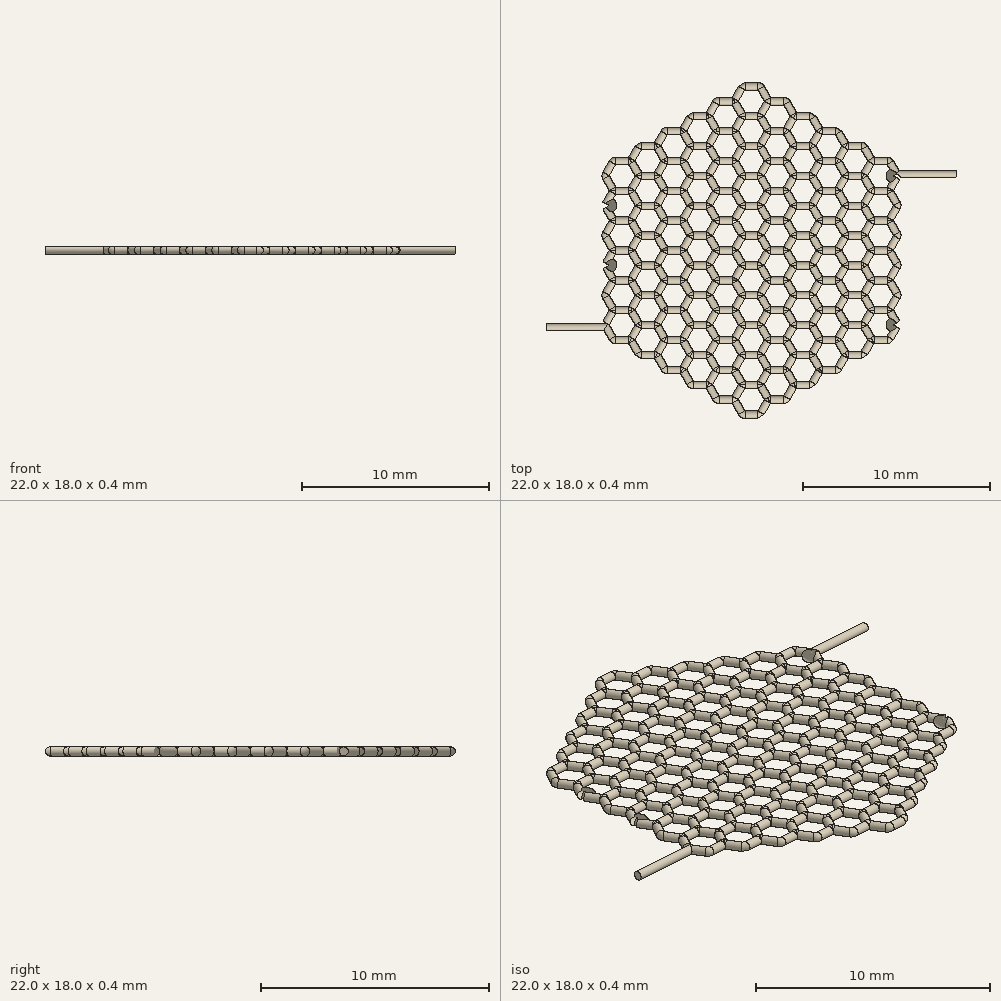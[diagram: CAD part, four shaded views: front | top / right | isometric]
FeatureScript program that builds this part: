
annotation { "Feature Type Name" : "Feature", "Feature Type Description" : "" }
export const myFeature = defineFeature(function(context is Context, id is Id, definition is map)
    precondition{}
    {
        {
            var Q0;
            Q0=qCreatedBy(makeId("Top.planeOp"),FACE);
            cPlane(context, id + "F0", {"entities" : qUnion([Q0]), "cplaneType" : CPlaneType.OFFSET, "offset" : 0.2 * mm, "width" : 150 * mm, "height" : 150 * mm});
        }
        {
            var Q0;
            Q0=qCreatedBy(id+"F0.planeOp",FACE);
            var sketch = newSketch(context, id + "F1", { "sketchPlane" : qUnion([Q0])});
            skLineSegment(sketch, "E0", {"start": v(-0.35, -0.8) * mm, "end": v(0.35, -0.8) * mm});
            skLineSegment(sketch, "E1", {"start": v(0.52, -0.7) * mm, "end": v(0.87, -0.1) * mm});
            skLineSegment(sketch, "E2", {"start": v(0.87, 0.1) * mm, "end": v(0.52, 0.7) * mm});
            skLineSegment(sketch, "E3", {"start": v(0.35, 0.8) * mm, "end": v(-0.35, 0.8) * mm});
            skLineSegment(sketch, "E4", {"start": v(-0.52, 0.7) * mm, "end": v(-0.87, 0.1) * mm});
            skLineSegment(sketch, "E5", {"start": v(-0.87, -0.1) * mm, "end": v(-0.52, -0.7) * mm});
            skArc(sketch, "E6.filletArc", {"start": v(-0.35, 0.8) * mm, "mid": v(-0.45, 0.77) * mm, "end": v(-0.52, 0.7) * mm});
            skArc(sketch, "E7.filletArc", {"start": v(-0.87, 0.1) * mm, "mid": v(-0.9, 0) * mm, "end": v(-0.87, -0.1) * mm});
            skArc(sketch, "E8.filletArc", {"start": v(-0.52, -0.7) * mm, "mid": v(-0.45, -0.77) * mm, "end": v(-0.35, -0.8) * mm});
            skArc(sketch, "E9.filletArc", {"start": v(0.35, -0.8) * mm, "mid": v(0.45, -0.77) * mm, "end": v(0.52, -0.7) * mm});
            skArc(sketch, "E10.filletArc", {"start": v(0.87, -0.1) * mm, "mid": v(0.9, 0) * mm, "end": v(0.87, 0.1) * mm});
            skArc(sketch, "E11.filletArc", {"start": v(0.52, 0.7) * mm, "mid": v(0.45, 0.77) * mm, "end": v(0.35, 0.8) * mm});
            skLineSegment(sketch, "E12", {"start": v(-1.73, 0) * mm, "end": v(-1.04, 0) * mm});
            skLineSegment(sketch, "E13", {"start": v(-0.87, 0.1) * mm, "end": v(-0.52, 0.7) * mm});
            skLineSegment(sketch, "E14", {"start": v(-0.52, 0.9) * mm, "end": v(-0.87, 1.5) * mm});
            skLineSegment(sketch, "E15", {"start": v(-1.04, 1.6) * mm, "end": v(-1.73, 1.6) * mm});
            skLineSegment(sketch, "E16", {"start": v(-1.9, 1.5) * mm, "end": v(-2.25, 0.9) * mm});
            skLineSegment(sketch, "E17", {"start": v(-2.25, 0.7) * mm, "end": v(-1.9, 0.1) * mm});
            skArc(sketch, "E18.filletArc", {"start": v(-1.73, 1.6) * mm, "mid": v(-1.83, 1.57) * mm, "end": v(-1.9, 1.5) * mm});
            skArc(sketch, "E19.filletArc", {"start": v(-2.25, 0.9) * mm, "mid": v(-2.28, 0.8) * mm, "end": v(-2.25, 0.7) * mm});
            skArc(sketch, "E20.filletArc", {"start": v(-1.9, 0.1) * mm, "mid": v(-1.83, 0.03) * mm, "end": v(-1.73, 0) * mm});
            skArc(sketch, "E21.filletArc", {"start": v(-1.04, 0) * mm, "mid": v(-0.94, 0.03) * mm, "end": v(-0.87, 0.1) * mm});
            skArc(sketch, "E22.filletArc", {"start": v(-0.52, 0.7) * mm, "mid": v(-0.5, 0.8) * mm, "end": v(-0.52, 0.9) * mm});
            skArc(sketch, "E23.filletArc", {"start": v(-0.87, 1.5) * mm, "mid": v(-0.94, 1.57) * mm, "end": v(-1.04, 1.6) * mm});
            skLineSegment(sketch, "E24", {"start": v(-1.73, -1.6) * mm, "end": v(-1.04, -1.6) * mm});
            skLineSegment(sketch, "E25", {"start": v(-0.87, -1.5) * mm, "end": v(-0.52, -0.9) * mm});
            skLineSegment(sketch, "E26", {"start": v(-0.52, -0.7) * mm, "end": v(-0.87, -0.1) * mm});
            skLineSegment(sketch, "E27", {"start": v(-1.04, 0) * mm, "end": v(-1.73, 0) * mm});
            skLineSegment(sketch, "E28", {"start": v(-1.9, -0.1) * mm, "end": v(-2.25, -0.7) * mm});
            skLineSegment(sketch, "E29", {"start": v(-2.25, -0.9) * mm, "end": v(-1.9, -1.5) * mm});
            skArc(sketch, "E30.filletArc", {"start": v(-1.73, 0) * mm, "mid": v(-1.83, -0.03) * mm, "end": v(-1.9, -0.1) * mm});
            skArc(sketch, "E31.filletArc", {"start": v(-2.25, -0.7) * mm, "mid": v(-2.28, -0.8) * mm, "end": v(-2.25, -0.9) * mm});
            skArc(sketch, "E32.filletArc", {"start": v(-1.9, -1.5) * mm, "mid": v(-1.83, -1.57) * mm, "end": v(-1.73, -1.6) * mm});
            skArc(sketch, "E33.filletArc", {"start": v(-1.04, -1.6) * mm, "mid": v(-0.94, -1.57) * mm, "end": v(-0.87, -1.5) * mm});
            skArc(sketch, "E34.filletArc", {"start": v(-0.52, -0.9) * mm, "mid": v(-0.5, -0.8) * mm, "end": v(-0.52, -0.7) * mm});
            skArc(sketch, "E35.filletArc", {"start": v(-0.87, -0.1) * mm, "mid": v(-0.94, -0.03) * mm, "end": v(-1.04, 0) * mm});
            skLineSegment(sketch, "E36", {"start": v(-0.35, -2.4) * mm, "end": v(0.35, -2.4) * mm});
            skLineSegment(sketch, "E37", {"start": v(0.52, -2.3) * mm, "end": v(0.87, -1.7) * mm});
            skLineSegment(sketch, "E38", {"start": v(0.87, -1.5) * mm, "end": v(0.52, -0.9) * mm});
            skLineSegment(sketch, "E39", {"start": v(0.35, -0.8) * mm, "end": v(-0.35, -0.8) * mm});
            skLineSegment(sketch, "E40", {"start": v(-0.52, -0.9) * mm, "end": v(-0.87, -1.5) * mm});
            skLineSegment(sketch, "E41", {"start": v(-0.87, -1.7) * mm, "end": v(-0.52, -2.3) * mm});
            skArc(sketch, "E42.filletArc", {"start": v(-0.35, -0.8) * mm, "mid": v(-0.45, -0.83) * mm, "end": v(-0.52, -0.9) * mm});
            skArc(sketch, "E43.filletArc", {"start": v(-0.87, -1.5) * mm, "mid": v(-0.9, -1.6) * mm, "end": v(-0.87, -1.7) * mm});
            skArc(sketch, "E44.filletArc", {"start": v(-0.52, -2.3) * mm, "mid": v(-0.45, -2.37) * mm, "end": v(-0.35, -2.4) * mm});
            skArc(sketch, "E45.filletArc", {"start": v(0.35, -2.4) * mm, "mid": v(0.45, -2.37) * mm, "end": v(0.52, -2.3) * mm});
            skArc(sketch, "E46.filletArc", {"start": v(0.87, -1.7) * mm, "mid": v(0.9, -1.6) * mm, "end": v(0.87, -1.5) * mm});
            skArc(sketch, "E47.filletArc", {"start": v(0.52, -0.9) * mm, "mid": v(0.45, -0.83) * mm, "end": v(0.35, -0.8) * mm});
            skLineSegment(sketch, "E48", {"start": v(1.04, -1.6) * mm, "end": v(1.73, -1.6) * mm});
            skLineSegment(sketch, "E49", {"start": v(1.9, -1.5) * mm, "end": v(2.25, -0.9) * mm});
            skLineSegment(sketch, "E50", {"start": v(2.25, -0.7) * mm, "end": v(1.9, -0.1) * mm});
            skLineSegment(sketch, "E51", {"start": v(1.73, 0) * mm, "end": v(1.04, 0) * mm});
            skLineSegment(sketch, "E52", {"start": v(0.87, -0.1) * mm, "end": v(0.52, -0.7) * mm});
            skLineSegment(sketch, "E53", {"start": v(0.52, -0.9) * mm, "end": v(0.87, -1.5) * mm});
            skArc(sketch, "E54.filletArc", {"start": v(1.04, 0) * mm, "mid": v(0.94, -0.03) * mm, "end": v(0.87, -0.1) * mm});
            skArc(sketch, "E55.filletArc", {"start": v(0.52, -0.7) * mm, "mid": v(0.5, -0.8) * mm, "end": v(0.52, -0.9) * mm});
            skArc(sketch, "E56.filletArc", {"start": v(0.87, -1.5) * mm, "mid": v(0.94, -1.57) * mm, "end": v(1.04, -1.6) * mm});
            skArc(sketch, "E57.filletArc", {"start": v(1.73, -1.6) * mm, "mid": v(1.83, -1.57) * mm, "end": v(1.9, -1.5) * mm});
            skArc(sketch, "E58.filletArc", {"start": v(2.25, -0.9) * mm, "mid": v(2.28, -0.8) * mm, "end": v(2.25, -0.7) * mm});
            skArc(sketch, "E59.filletArc", {"start": v(1.9, -0.1) * mm, "mid": v(1.83, -0.03) * mm, "end": v(1.73, 0) * mm});
            skLineSegment(sketch, "E60", {"start": v(1.04, 0) * mm, "end": v(1.73, 0) * mm});
            skLineSegment(sketch, "E61", {"start": v(1.9, 0.1) * mm, "end": v(2.25, 0.7) * mm});
            skLineSegment(sketch, "E62", {"start": v(2.25, 0.9) * mm, "end": v(1.9, 1.5) * mm});
            skLineSegment(sketch, "E63", {"start": v(1.73, 1.6) * mm, "end": v(1.04, 1.6) * mm});
            skLineSegment(sketch, "E64", {"start": v(0.87, 1.5) * mm, "end": v(0.52, 0.9) * mm});
            skLineSegment(sketch, "E65", {"start": v(0.52, 0.7) * mm, "end": v(0.87, 0.1) * mm});
            skArc(sketch, "E66.filletArc", {"start": v(1.04, 1.6) * mm, "mid": v(0.94, 1.57) * mm, "end": v(0.87, 1.5) * mm});
            skArc(sketch, "E67.filletArc", {"start": v(0.52, 0.9) * mm, "mid": v(0.5, 0.8) * mm, "end": v(0.52, 0.7) * mm});
            skArc(sketch, "E68.filletArc", {"start": v(0.87, 0.1) * mm, "mid": v(0.94, 0.03) * mm, "end": v(1.04, 0) * mm});
            skArc(sketch, "E69.filletArc", {"start": v(1.73, 0) * mm, "mid": v(1.83, 0.03) * mm, "end": v(1.9, 0.1) * mm});
            skArc(sketch, "E70.filletArc", {"start": v(2.25, 0.7) * mm, "mid": v(2.28, 0.8) * mm, "end": v(2.25, 0.9) * mm});
            skArc(sketch, "E71.filletArc", {"start": v(1.9, 1.5) * mm, "mid": v(1.83, 1.57) * mm, "end": v(1.73, 1.6) * mm});
            skLineSegment(sketch, "E72", {"start": v(-0.35, 0.8) * mm, "end": v(0.35, 0.8) * mm});
            skLineSegment(sketch, "E73", {"start": v(0.52, 0.9) * mm, "end": v(0.87, 1.5) * mm});
            skLineSegment(sketch, "E74", {"start": v(0.87, 1.7) * mm, "end": v(0.52, 2.3) * mm});
            skLineSegment(sketch, "E75", {"start": v(0.35, 2.4) * mm, "end": v(-0.35, 2.4) * mm});
            skLineSegment(sketch, "E76", {"start": v(-0.52, 2.3) * mm, "end": v(-0.87, 1.7) * mm});
            skLineSegment(sketch, "E77", {"start": v(-0.87, 1.5) * mm, "end": v(-0.52, 0.9) * mm});
            skArc(sketch, "E78.filletArc", {"start": v(-0.35, 2.4) * mm, "mid": v(-0.45, 2.37) * mm, "end": v(-0.52, 2.3) * mm});
            skArc(sketch, "E79.filletArc", {"start": v(-0.87, 1.7) * mm, "mid": v(-0.9, 1.6) * mm, "end": v(-0.87, 1.5) * mm});
            skArc(sketch, "E80.filletArc", {"start": v(-0.52, 0.9) * mm, "mid": v(-0.45, 0.83) * mm, "end": v(-0.35, 0.8) * mm});
            skArc(sketch, "E81.filletArc", {"start": v(0.35, 0.8) * mm, "mid": v(0.45, 0.83) * mm, "end": v(0.52, 0.9) * mm});
            skArc(sketch, "E82.filletArc", {"start": v(0.87, 1.5) * mm, "mid": v(0.9, 1.6) * mm, "end": v(0.87, 1.7) * mm});
            skArc(sketch, "E83.filletArc", {"start": v(0.52, 2.3) * mm, "mid": v(0.45, 2.37) * mm, "end": v(0.35, 2.4) * mm});
            skLineSegment(sketch, "E84", {"start": v(-3.12, -0.8) * mm, "end": v(-2.42, -0.8) * mm});
            skLineSegment(sketch, "E85", {"start": v(-2.25, -0.7) * mm, "end": v(-1.9, -0.1) * mm});
            skLineSegment(sketch, "E86", {"start": v(-1.9, 0.1) * mm, "end": v(-2.25, 0.7) * mm});
            skLineSegment(sketch, "E87", {"start": v(-2.42, 0.8) * mm, "end": v(-3.12, 0.8) * mm});
            skLineSegment(sketch, "E88", {"start": v(-3.3, 0.7) * mm, "end": v(-3.64, 0.1) * mm});
            skLineSegment(sketch, "E89", {"start": v(-3.64, -0.1) * mm, "end": v(-3.3, -0.7) * mm});
            skArc(sketch, "E90.filletArc", {"start": v(-3.12, 0.8) * mm, "mid": v(-3.22, 0.77) * mm, "end": v(-3.3, 0.7) * mm});
            skArc(sketch, "E91.filletArc", {"start": v(-3.64, 0.1) * mm, "mid": v(-3.66, 0) * mm, "end": v(-3.64, -0.1) * mm});
            skArc(sketch, "E92.filletArc", {"start": v(-3.3, -0.7) * mm, "mid": v(-3.22, -0.77) * mm, "end": v(-3.12, -0.8) * mm});
            skArc(sketch, "E93.filletArc", {"start": v(-2.42, -0.8) * mm, "mid": v(-2.32, -0.77) * mm, "end": v(-2.25, -0.7) * mm});
            skArc(sketch, "E94.filletArc", {"start": v(-1.9, -0.1) * mm, "mid": v(-1.88, 0) * mm, "end": v(-1.9, 0.1) * mm});
            skArc(sketch, "E95.filletArc", {"start": v(-2.25, 0.7) * mm, "mid": v(-2.32, 0.77) * mm, "end": v(-2.42, 0.8) * mm});
            skLineSegment(sketch, "E96", {"start": v(-3.12, -2.4) * mm, "end": v(-2.42, -2.4) * mm});
            skLineSegment(sketch, "E97", {"start": v(-2.25, -2.3) * mm, "end": v(-1.9, -1.7) * mm});
            skLineSegment(sketch, "E98", {"start": v(-1.9, -1.5) * mm, "end": v(-2.25, -0.9) * mm});
            skLineSegment(sketch, "E99", {"start": v(-2.42, -0.8) * mm, "end": v(-3.12, -0.8) * mm});
            skLineSegment(sketch, "E100", {"start": v(-3.3, -0.9) * mm, "end": v(-3.64, -1.5) * mm});
            skLineSegment(sketch, "E101", {"start": v(-3.64, -1.7) * mm, "end": v(-3.3, -2.3) * mm});
            skArc(sketch, "E102.filletArc", {"start": v(-3.12, -0.8) * mm, "mid": v(-3.22, -0.83) * mm, "end": v(-3.3, -0.9) * mm});
            skArc(sketch, "E103.filletArc", {"start": v(-3.64, -1.5) * mm, "mid": v(-3.66, -1.6) * mm, "end": v(-3.64, -1.7) * mm});
            skArc(sketch, "E104.filletArc", {"start": v(-3.3, -2.3) * mm, "mid": v(-3.22, -2.37) * mm, "end": v(-3.12, -2.4) * mm});
            skArc(sketch, "E105.filletArc", {"start": v(-2.42, -2.4) * mm, "mid": v(-2.32, -2.37) * mm, "end": v(-2.25, -2.3) * mm});
            skArc(sketch, "E106.filletArc", {"start": v(-1.9, -1.7) * mm, "mid": v(-1.88, -1.6) * mm, "end": v(-1.9, -1.5) * mm});
            skArc(sketch, "E107.filletArc", {"start": v(-2.25, -0.9) * mm, "mid": v(-2.32, -0.83) * mm, "end": v(-2.42, -0.8) * mm});
            skLineSegment(sketch, "E108", {"start": v(-0.35, -4) * mm, "end": v(0.35, -4) * mm});
            skLineSegment(sketch, "E109", {"start": v(0.52, -3.9) * mm, "end": v(0.87, -3.3) * mm});
            skLineSegment(sketch, "E110", {"start": v(0.87, -3.1) * mm, "end": v(0.52, -2.5) * mm});
            skLineSegment(sketch, "E111", {"start": v(0.35, -2.4) * mm, "end": v(-0.35, -2.4) * mm});
            skLineSegment(sketch, "E112", {"start": v(-0.52, -2.5) * mm, "end": v(-0.87, -3.1) * mm});
            skLineSegment(sketch, "E113", {"start": v(-0.87, -3.3) * mm, "end": v(-0.52, -3.9) * mm});
            skArc(sketch, "E114.filletArc", {"start": v(-0.35, -2.4) * mm, "mid": v(-0.45, -2.43) * mm, "end": v(-0.52, -2.5) * mm});
            skArc(sketch, "E115.filletArc", {"start": v(-0.87, -3.1) * mm, "mid": v(-0.9, -3.2) * mm, "end": v(-0.87, -3.3) * mm});
            skArc(sketch, "E116.filletArc", {"start": v(-0.52, -3.9) * mm, "mid": v(-0.45, -3.97) * mm, "end": v(-0.35, -4) * mm});
            skArc(sketch, "E117.filletArc", {"start": v(0.35, -4) * mm, "mid": v(0.45, -3.97) * mm, "end": v(0.52, -3.9) * mm});
            skArc(sketch, "E118.filletArc", {"start": v(0.87, -3.3) * mm, "mid": v(0.9, -3.2) * mm, "end": v(0.87, -3.1) * mm});
            skArc(sketch, "E119.filletArc", {"start": v(0.52, -2.5) * mm, "mid": v(0.45, -2.43) * mm, "end": v(0.35, -2.4) * mm});
            skLineSegment(sketch, "E120", {"start": v(-1.73, -3.2) * mm, "end": v(-1.04, -3.2) * mm});
            skLineSegment(sketch, "E121", {"start": v(-0.87, -3.1) * mm, "end": v(-0.52, -2.5) * mm});
            skLineSegment(sketch, "E122", {"start": v(-0.52, -2.3) * mm, "end": v(-0.87, -1.7) * mm});
            skLineSegment(sketch, "E123", {"start": v(-1.04, -1.6) * mm, "end": v(-1.73, -1.6) * mm});
            skLineSegment(sketch, "E124", {"start": v(-1.9, -1.7) * mm, "end": v(-2.25, -2.3) * mm});
            skLineSegment(sketch, "E125", {"start": v(-2.25, -2.5) * mm, "end": v(-1.9, -3.1) * mm});
            skArc(sketch, "E126.filletArc", {"start": v(-1.73, -1.6) * mm, "mid": v(-1.83, -1.63) * mm, "end": v(-1.9, -1.7) * mm});
            skArc(sketch, "E127.filletArc", {"start": v(-2.25, -2.3) * mm, "mid": v(-2.28, -2.4) * mm, "end": v(-2.25, -2.5) * mm});
            skArc(sketch, "E128.filletArc", {"start": v(-1.9, -3.1) * mm, "mid": v(-1.83, -3.17) * mm, "end": v(-1.73, -3.2) * mm});
            skArc(sketch, "E129.filletArc", {"start": v(-1.04, -3.2) * mm, "mid": v(-0.94, -3.17) * mm, "end": v(-0.87, -3.1) * mm});
            skArc(sketch, "E130.filletArc", {"start": v(-0.52, -2.5) * mm, "mid": v(-0.5, -2.4) * mm, "end": v(-0.52, -2.3) * mm});
            skArc(sketch, "E131.filletArc", {"start": v(-0.87, -1.7) * mm, "mid": v(-0.94, -1.63) * mm, "end": v(-1.04, -1.6) * mm});
            skLineSegment(sketch, "E132", {"start": v(2.42, -0.8) * mm, "end": v(3.12, -0.8) * mm});
            skLineSegment(sketch, "E133", {"start": v(3.3, -0.7) * mm, "end": v(3.64, -0.1) * mm});
            skLineSegment(sketch, "E134", {"start": v(3.64, 0.1) * mm, "end": v(3.3, 0.7) * mm});
            skLineSegment(sketch, "E135", {"start": v(3.12, 0.8) * mm, "end": v(2.42, 0.8) * mm});
            skLineSegment(sketch, "E136", {"start": v(2.25, 0.7) * mm, "end": v(1.9, 0.1) * mm});
            skLineSegment(sketch, "E137", {"start": v(1.9, -0.1) * mm, "end": v(2.25, -0.7) * mm});
            skArc(sketch, "E138.filletArc", {"start": v(2.42, 0.8) * mm, "mid": v(2.32, 0.77) * mm, "end": v(2.25, 0.7) * mm});
            skArc(sketch, "E139.filletArc", {"start": v(1.9, 0.1) * mm, "mid": v(1.88, 0) * mm, "end": v(1.9, -0.1) * mm});
            skArc(sketch, "E140.filletArc", {"start": v(2.25, -0.7) * mm, "mid": v(2.32, -0.77) * mm, "end": v(2.42, -0.8) * mm});
            skArc(sketch, "E141.filletArc", {"start": v(3.12, -0.8) * mm, "mid": v(3.22, -0.77) * mm, "end": v(3.3, -0.7) * mm});
            skArc(sketch, "E142.filletArc", {"start": v(3.64, -0.1) * mm, "mid": v(3.66, 0) * mm, "end": v(3.64, 0.1) * mm});
            skArc(sketch, "E143.filletArc", {"start": v(3.3, 0.7) * mm, "mid": v(3.22, 0.77) * mm, "end": v(3.12, 0.8) * mm});
            skLineSegment(sketch, "E144", {"start": v(1.04, -3.2) * mm, "end": v(1.73, -3.2) * mm});
            skLineSegment(sketch, "E145", {"start": v(1.9, -3.1) * mm, "end": v(2.25, -2.5) * mm});
            skLineSegment(sketch, "E146", {"start": v(2.25, -2.3) * mm, "end": v(1.9, -1.7) * mm});
            skLineSegment(sketch, "E147", {"start": v(1.73, -1.6) * mm, "end": v(1.04, -1.6) * mm});
            skLineSegment(sketch, "E148", {"start": v(0.87, -1.7) * mm, "end": v(0.52, -2.3) * mm});
            skLineSegment(sketch, "E149", {"start": v(0.52, -2.5) * mm, "end": v(0.87, -3.1) * mm});
            skArc(sketch, "E150.filletArc", {"start": v(1.04, -1.6) * mm, "mid": v(0.94, -1.63) * mm, "end": v(0.87, -1.7) * mm});
            skArc(sketch, "E151.filletArc", {"start": v(0.52, -2.3) * mm, "mid": v(0.5, -2.4) * mm, "end": v(0.52, -2.5) * mm});
            skArc(sketch, "E152.filletArc", {"start": v(0.87, -3.1) * mm, "mid": v(0.94, -3.17) * mm, "end": v(1.04, -3.2) * mm});
            skArc(sketch, "E153.filletArc", {"start": v(1.73, -3.2) * mm, "mid": v(1.83, -3.17) * mm, "end": v(1.9, -3.1) * mm});
            skArc(sketch, "E154.filletArc", {"start": v(2.25, -2.5) * mm, "mid": v(2.28, -2.4) * mm, "end": v(2.25, -2.3) * mm});
            skArc(sketch, "E155.filletArc", {"start": v(1.9, -1.7) * mm, "mid": v(1.83, -1.63) * mm, "end": v(1.73, -1.6) * mm});
            skLineSegment(sketch, "E156", {"start": v(2.42, -2.4) * mm, "end": v(3.12, -2.4) * mm});
            skLineSegment(sketch, "E157", {"start": v(3.3, -2.3) * mm, "end": v(3.64, -1.7) * mm});
            skLineSegment(sketch, "E158", {"start": v(3.64, -1.5) * mm, "end": v(3.3, -0.9) * mm});
            skLineSegment(sketch, "E159", {"start": v(3.12, -0.8) * mm, "end": v(2.42, -0.8) * mm});
            skLineSegment(sketch, "E160", {"start": v(2.25, -0.9) * mm, "end": v(1.9, -1.5) * mm});
            skLineSegment(sketch, "E161", {"start": v(1.9, -1.7) * mm, "end": v(2.25, -2.3) * mm});
            skArc(sketch, "E162.filletArc", {"start": v(2.42, -0.8) * mm, "mid": v(2.32, -0.83) * mm, "end": v(2.25, -0.9) * mm});
            skArc(sketch, "E163.filletArc", {"start": v(1.9, -1.5) * mm, "mid": v(1.88, -1.6) * mm, "end": v(1.9, -1.7) * mm});
            skArc(sketch, "E164.filletArc", {"start": v(2.25, -2.3) * mm, "mid": v(2.32, -2.37) * mm, "end": v(2.42, -2.4) * mm});
            skArc(sketch, "E165.filletArc", {"start": v(3.12, -2.4) * mm, "mid": v(3.22, -2.37) * mm, "end": v(3.3, -2.3) * mm});
            skArc(sketch, "E166.filletArc", {"start": v(3.64, -1.7) * mm, "mid": v(3.66, -1.6) * mm, "end": v(3.64, -1.5) * mm});
            skArc(sketch, "E167.filletArc", {"start": v(3.3, -0.9) * mm, "mid": v(3.22, -0.83) * mm, "end": v(3.12, -0.8) * mm});
            skLineSegment(sketch, "E168", {"start": v(2.42, 0.8) * mm, "end": v(3.12, 0.8) * mm});
            skLineSegment(sketch, "E169", {"start": v(3.3, 0.9) * mm, "end": v(3.64, 1.5) * mm});
            skLineSegment(sketch, "E170", {"start": v(3.64, 1.7) * mm, "end": v(3.3, 2.3) * mm});
            skLineSegment(sketch, "E171", {"start": v(3.12, 2.4) * mm, "end": v(2.42, 2.4) * mm});
            skLineSegment(sketch, "E172", {"start": v(2.25, 2.3) * mm, "end": v(1.9, 1.7) * mm});
            skLineSegment(sketch, "E173", {"start": v(1.9, 1.5) * mm, "end": v(2.25, 0.9) * mm});
            skArc(sketch, "E174.filletArc", {"start": v(2.42, 2.4) * mm, "mid": v(2.32, 2.37) * mm, "end": v(2.25, 2.3) * mm});
            skArc(sketch, "E175.filletArc", {"start": v(1.9, 1.7) * mm, "mid": v(1.88, 1.6) * mm, "end": v(1.9, 1.5) * mm});
            skArc(sketch, "E176.filletArc", {"start": v(2.25, 0.9) * mm, "mid": v(2.32, 0.83) * mm, "end": v(2.42, 0.8) * mm});
            skArc(sketch, "E177.filletArc", {"start": v(3.12, 0.8) * mm, "mid": v(3.22, 0.83) * mm, "end": v(3.3, 0.9) * mm});
            skArc(sketch, "E178.filletArc", {"start": v(3.64, 1.5) * mm, "mid": v(3.66, 1.6) * mm, "end": v(3.64, 1.7) * mm});
            skArc(sketch, "E179.filletArc", {"start": v(3.3, 2.3) * mm, "mid": v(3.22, 2.37) * mm, "end": v(3.12, 2.4) * mm});
            skLineSegment(sketch, "E180", {"start": v(-1.73, 1.6) * mm, "end": v(-1.04, 1.6) * mm});
            skLineSegment(sketch, "E181", {"start": v(-0.87, 1.7) * mm, "end": v(-0.52, 2.3) * mm});
            skLineSegment(sketch, "E182", {"start": v(-0.52, 2.5) * mm, "end": v(-0.87, 3.1) * mm});
            skLineSegment(sketch, "E183", {"start": v(-1.04, 3.2) * mm, "end": v(-1.73, 3.2) * mm});
            skLineSegment(sketch, "E184", {"start": v(-1.9, 3.1) * mm, "end": v(-2.25, 2.5) * mm});
            skLineSegment(sketch, "E185", {"start": v(-2.25, 2.3) * mm, "end": v(-1.9, 1.7) * mm});
            skArc(sketch, "E186.filletArc", {"start": v(-1.73, 3.2) * mm, "mid": v(-1.83, 3.17) * mm, "end": v(-1.9, 3.1) * mm});
            skArc(sketch, "E187.filletArc", {"start": v(-2.25, 2.5) * mm, "mid": v(-2.28, 2.4) * mm, "end": v(-2.25, 2.3) * mm});
            skArc(sketch, "E188.filletArc", {"start": v(-1.9, 1.7) * mm, "mid": v(-1.83, 1.63) * mm, "end": v(-1.73, 1.6) * mm});
            skArc(sketch, "E189.filletArc", {"start": v(-1.04, 1.6) * mm, "mid": v(-0.94, 1.63) * mm, "end": v(-0.87, 1.7) * mm});
            skArc(sketch, "E190.filletArc", {"start": v(-0.52, 2.3) * mm, "mid": v(-0.5, 2.4) * mm, "end": v(-0.52, 2.5) * mm});
            skArc(sketch, "E191.filletArc", {"start": v(-0.87, 3.1) * mm, "mid": v(-0.94, 3.17) * mm, "end": v(-1.04, 3.2) * mm});
            skLineSegment(sketch, "E192", {"start": v(1.04, 1.6) * mm, "end": v(1.73, 1.6) * mm});
            skLineSegment(sketch, "E193", {"start": v(1.9, 1.7) * mm, "end": v(2.25, 2.3) * mm});
            skLineSegment(sketch, "E194", {"start": v(2.25, 2.5) * mm, "end": v(1.9, 3.1) * mm});
            skLineSegment(sketch, "E195", {"start": v(1.73, 3.2) * mm, "end": v(1.04, 3.2) * mm});
            skLineSegment(sketch, "E196", {"start": v(0.87, 3.1) * mm, "end": v(0.52, 2.5) * mm});
            skLineSegment(sketch, "E197", {"start": v(0.52, 2.3) * mm, "end": v(0.87, 1.7) * mm});
            skArc(sketch, "E198.filletArc", {"start": v(1.04, 3.2) * mm, "mid": v(0.94, 3.17) * mm, "end": v(0.87, 3.1) * mm});
            skArc(sketch, "E199.filletArc", {"start": v(0.52, 2.5) * mm, "mid": v(0.5, 2.4) * mm, "end": v(0.52, 2.3) * mm});
            skArc(sketch, "E200.filletArc", {"start": v(0.87, 1.7) * mm, "mid": v(0.94, 1.63) * mm, "end": v(1.04, 1.6) * mm});
            skArc(sketch, "E201.filletArc", {"start": v(1.73, 1.6) * mm, "mid": v(1.83, 1.63) * mm, "end": v(1.9, 1.7) * mm});
            skArc(sketch, "E202.filletArc", {"start": v(2.25, 2.3) * mm, "mid": v(2.28, 2.4) * mm, "end": v(2.25, 2.5) * mm});
            skArc(sketch, "E203.filletArc", {"start": v(1.9, 3.1) * mm, "mid": v(1.83, 3.17) * mm, "end": v(1.73, 3.2) * mm});
            skLineSegment(sketch, "E204", {"start": v(-0.35, 2.4) * mm, "end": v(0.35, 2.4) * mm});
            skLineSegment(sketch, "E205", {"start": v(0.52, 2.5) * mm, "end": v(0.87, 3.1) * mm});
            skLineSegment(sketch, "E206", {"start": v(0.87, 3.3) * mm, "end": v(0.52, 3.9) * mm});
            skLineSegment(sketch, "E207", {"start": v(0.35, 4) * mm, "end": v(-0.35, 4) * mm});
            skLineSegment(sketch, "E208", {"start": v(-0.52, 3.9) * mm, "end": v(-0.87, 3.3) * mm});
            skLineSegment(sketch, "E209", {"start": v(-0.87, 3.1) * mm, "end": v(-0.52, 2.5) * mm});
            skArc(sketch, "E210.filletArc", {"start": v(-0.35, 4) * mm, "mid": v(-0.45, 3.97) * mm, "end": v(-0.52, 3.9) * mm});
            skArc(sketch, "E211.filletArc", {"start": v(-0.87, 3.3) * mm, "mid": v(-0.9, 3.2) * mm, "end": v(-0.87, 3.1) * mm});
            skArc(sketch, "E212.filletArc", {"start": v(-0.52, 2.5) * mm, "mid": v(-0.45, 2.43) * mm, "end": v(-0.35, 2.4) * mm});
            skArc(sketch, "E213.filletArc", {"start": v(0.35, 2.4) * mm, "mid": v(0.45, 2.43) * mm, "end": v(0.52, 2.5) * mm});
            skArc(sketch, "E214.filletArc", {"start": v(0.87, 3.1) * mm, "mid": v(0.9, 3.2) * mm, "end": v(0.87, 3.3) * mm});
            skArc(sketch, "E215.filletArc", {"start": v(0.52, 3.9) * mm, "mid": v(0.45, 3.97) * mm, "end": v(0.35, 4) * mm});
            skLineSegment(sketch, "E216", {"start": v(-3.12, 0.8) * mm, "end": v(-2.42, 0.8) * mm});
            skLineSegment(sketch, "E217", {"start": v(-2.25, 0.9) * mm, "end": v(-1.9, 1.5) * mm});
            skLineSegment(sketch, "E218", {"start": v(-1.9, 1.7) * mm, "end": v(-2.25, 2.3) * mm});
            skLineSegment(sketch, "E219", {"start": v(-2.42, 2.4) * mm, "end": v(-3.12, 2.4) * mm});
            skLineSegment(sketch, "E220", {"start": v(-3.3, 2.3) * mm, "end": v(-3.64, 1.7) * mm});
            skLineSegment(sketch, "E221", {"start": v(-3.64, 1.5) * mm, "end": v(-3.3, 0.9) * mm});
            skArc(sketch, "E222.filletArc", {"start": v(-3.12, 2.4) * mm, "mid": v(-3.22, 2.37) * mm, "end": v(-3.3, 2.3) * mm});
            skArc(sketch, "E223.filletArc", {"start": v(-3.64, 1.7) * mm, "mid": v(-3.66, 1.6) * mm, "end": v(-3.64, 1.5) * mm});
            skArc(sketch, "E224.filletArc", {"start": v(-3.3, 0.9) * mm, "mid": v(-3.22, 0.83) * mm, "end": v(-3.12, 0.8) * mm});
            skArc(sketch, "E225.filletArc", {"start": v(-2.42, 0.8) * mm, "mid": v(-2.32, 0.83) * mm, "end": v(-2.25, 0.9) * mm});
            skArc(sketch, "E226.filletArc", {"start": v(-1.9, 1.5) * mm, "mid": v(-1.88, 1.6) * mm, "end": v(-1.9, 1.7) * mm});
            skArc(sketch, "E227.filletArc", {"start": v(-2.25, 2.3) * mm, "mid": v(-2.32, 2.37) * mm, "end": v(-2.42, 2.4) * mm});
            skLineSegment(sketch, "E228", {"start": v(3.81, -1.6) * mm, "end": v(4.5, -1.6) * mm});
            skLineSegment(sketch, "E229", {"start": v(4.68, -1.5) * mm, "end": v(5.02, -0.9) * mm});
            skLineSegment(sketch, "E230", {"start": v(5.02, -0.7) * mm, "end": v(4.68, -0.1) * mm});
            skLineSegment(sketch, "E231", {"start": v(4.5, 0) * mm, "end": v(3.81, 0) * mm});
            skLineSegment(sketch, "E232", {"start": v(3.64, -0.1) * mm, "end": v(3.3, -0.7) * mm});
            skLineSegment(sketch, "E233", {"start": v(3.3, -0.9) * mm, "end": v(3.64, -1.5) * mm});
            skArc(sketch, "E234.filletArc", {"start": v(3.81, 0) * mm, "mid": v(3.71, -0.03) * mm, "end": v(3.64, -0.1) * mm});
            skArc(sketch, "E235.filletArc", {"start": v(3.3, -0.7) * mm, "mid": v(3.26, -0.8) * mm, "end": v(3.3, -0.9) * mm});
            skArc(sketch, "E236.filletArc", {"start": v(3.64, -1.5) * mm, "mid": v(3.71, -1.57) * mm, "end": v(3.81, -1.6) * mm});
            skArc(sketch, "E237.filletArc", {"start": v(4.5, -1.6) * mm, "mid": v(4.6, -1.57) * mm, "end": v(4.68, -1.5) * mm});
            skArc(sketch, "E238.filletArc", {"start": v(5.02, -0.9) * mm, "mid": v(5.05, -0.8) * mm, "end": v(5.02, -0.7) * mm});
            skArc(sketch, "E239.filletArc", {"start": v(4.68, -0.1) * mm, "mid": v(4.6, -0.03) * mm, "end": v(4.5, 0) * mm});
            skLineSegment(sketch, "E240", {"start": v(3.81, 0) * mm, "end": v(4.5, 0) * mm});
            skLineSegment(sketch, "E241", {"start": v(4.68, 0.1) * mm, "end": v(5.02, 0.7) * mm});
            skLineSegment(sketch, "E242", {"start": v(5.02, 0.9) * mm, "end": v(4.68, 1.5) * mm});
            skLineSegment(sketch, "E243", {"start": v(4.5, 1.6) * mm, "end": v(3.81, 1.6) * mm});
            skLineSegment(sketch, "E244", {"start": v(3.64, 1.5) * mm, "end": v(3.3, 0.9) * mm});
            skLineSegment(sketch, "E245", {"start": v(3.3, 0.7) * mm, "end": v(3.64, 0.1) * mm});
            skArc(sketch, "E246.filletArc", {"start": v(3.81, 1.6) * mm, "mid": v(3.71, 1.57) * mm, "end": v(3.64, 1.5) * mm});
            skArc(sketch, "E247.filletArc", {"start": v(3.3, 0.9) * mm, "mid": v(3.26, 0.8) * mm, "end": v(3.3, 0.7) * mm});
            skArc(sketch, "E248.filletArc", {"start": v(3.64, 0.1) * mm, "mid": v(3.71, 0.03) * mm, "end": v(3.81, 0) * mm});
            skArc(sketch, "E249.filletArc", {"start": v(4.5, 0) * mm, "mid": v(4.6, 0.03) * mm, "end": v(4.68, 0.1) * mm});
            skArc(sketch, "E250.filletArc", {"start": v(5.02, 0.7) * mm, "mid": v(5.05, 0.8) * mm, "end": v(5.02, 0.9) * mm});
            skArc(sketch, "E251.filletArc", {"start": v(4.68, 1.5) * mm, "mid": v(4.6, 1.57) * mm, "end": v(4.5, 1.6) * mm});
            skLineSegment(sketch, "E252", {"start": v(3.81, 1.6) * mm, "end": v(4.5, 1.6) * mm});
            skLineSegment(sketch, "E253", {"start": v(4.68, 1.7) * mm, "end": v(5.02, 2.3) * mm});
            skLineSegment(sketch, "E254", {"start": v(5.02, 2.5) * mm, "end": v(4.68, 3.1) * mm});
            skLineSegment(sketch, "E255", {"start": v(4.5, 3.2) * mm, "end": v(3.81, 3.2) * mm});
            skLineSegment(sketch, "E256", {"start": v(3.64, 3.1) * mm, "end": v(3.3, 2.5) * mm});
            skLineSegment(sketch, "E257", {"start": v(3.3, 2.3) * mm, "end": v(3.64, 1.7) * mm});
            skArc(sketch, "E258.filletArc", {"start": v(3.81, 3.2) * mm, "mid": v(3.71, 3.17) * mm, "end": v(3.64, 3.1) * mm});
            skArc(sketch, "E259.filletArc", {"start": v(3.3, 2.5) * mm, "mid": v(3.26, 2.4) * mm, "end": v(3.3, 2.3) * mm});
            skArc(sketch, "E260.filletArc", {"start": v(3.64, 1.7) * mm, "mid": v(3.71, 1.63) * mm, "end": v(3.81, 1.6) * mm});
            skArc(sketch, "E261.filletArc", {"start": v(4.5, 1.6) * mm, "mid": v(4.6, 1.63) * mm, "end": v(4.68, 1.7) * mm});
            skArc(sketch, "E262.filletArc", {"start": v(5.02, 2.3) * mm, "mid": v(5.05, 2.4) * mm, "end": v(5.02, 2.5) * mm});
            skArc(sketch, "E263.filletArc", {"start": v(4.68, 3.1) * mm, "mid": v(4.6, 3.17) * mm, "end": v(4.5, 3.2) * mm});
            skLineSegment(sketch, "E264", {"start": v(2.42, 2.4) * mm, "end": v(3.12, 2.4) * mm});
            skLineSegment(sketch, "E265", {"start": v(3.3, 2.5) * mm, "end": v(3.64, 3.1) * mm});
            skLineSegment(sketch, "E266", {"start": v(3.64, 3.3) * mm, "end": v(3.3, 3.9) * mm});
            skLineSegment(sketch, "E267", {"start": v(3.12, 4) * mm, "end": v(2.42, 4) * mm});
            skLineSegment(sketch, "E268", {"start": v(2.25, 3.9) * mm, "end": v(1.9, 3.3) * mm});
            skLineSegment(sketch, "E269", {"start": v(1.9, 3.1) * mm, "end": v(2.25, 2.5) * mm});
            skArc(sketch, "E270.filletArc", {"start": v(2.42, 4) * mm, "mid": v(2.32, 3.97) * mm, "end": v(2.25, 3.9) * mm});
            skArc(sketch, "E271.filletArc", {"start": v(1.9, 3.3) * mm, "mid": v(1.88, 3.2) * mm, "end": v(1.9, 3.1) * mm});
            skArc(sketch, "E272.filletArc", {"start": v(2.25, 2.5) * mm, "mid": v(2.32, 2.43) * mm, "end": v(2.42, 2.4) * mm});
            skArc(sketch, "E273.filletArc", {"start": v(3.12, 2.4) * mm, "mid": v(3.22, 2.43) * mm, "end": v(3.3, 2.5) * mm});
            skArc(sketch, "E274.filletArc", {"start": v(3.64, 3.1) * mm, "mid": v(3.66, 3.2) * mm, "end": v(3.64, 3.3) * mm});
            skArc(sketch, "E275.filletArc", {"start": v(3.3, 3.9) * mm, "mid": v(3.22, 3.97) * mm, "end": v(3.12, 4) * mm});
            skLineSegment(sketch, "E276", {"start": v(1.04, 3.2) * mm, "end": v(1.73, 3.2) * mm});
            skLineSegment(sketch, "E277", {"start": v(1.9, 3.3) * mm, "end": v(2.25, 3.9) * mm});
            skLineSegment(sketch, "E278", {"start": v(2.25, 4.1) * mm, "end": v(1.9, 4.7) * mm});
            skLineSegment(sketch, "E279", {"start": v(1.73, 4.8) * mm, "end": v(1.04, 4.8) * mm});
            skLineSegment(sketch, "E280", {"start": v(0.87, 4.7) * mm, "end": v(0.52, 4.1) * mm});
            skLineSegment(sketch, "E281", {"start": v(0.52, 3.9) * mm, "end": v(0.87, 3.3) * mm});
            skArc(sketch, "E282.filletArc", {"start": v(1.04, 4.8) * mm, "mid": v(0.94, 4.77) * mm, "end": v(0.87, 4.7) * mm});
            skArc(sketch, "E283.filletArc", {"start": v(0.52, 4.1) * mm, "mid": v(0.5, 4) * mm, "end": v(0.52, 3.9) * mm});
            skArc(sketch, "E284.filletArc", {"start": v(0.87, 3.3) * mm, "mid": v(0.94, 3.23) * mm, "end": v(1.04, 3.2) * mm});
            skArc(sketch, "E285.filletArc", {"start": v(1.73, 3.2) * mm, "mid": v(1.83, 3.23) * mm, "end": v(1.9, 3.3) * mm});
            skArc(sketch, "E286.filletArc", {"start": v(2.25, 3.9) * mm, "mid": v(2.28, 4) * mm, "end": v(2.25, 4.1) * mm});
            skArc(sketch, "E287.filletArc", {"start": v(1.9, 4.7) * mm, "mid": v(1.83, 4.77) * mm, "end": v(1.73, 4.8) * mm});
            skLineSegment(sketch, "E288", {"start": v(-1.73, 3.2) * mm, "end": v(-1.04, 3.2) * mm});
            skLineSegment(sketch, "E289", {"start": v(-0.87, 3.3) * mm, "end": v(-0.52, 3.9) * mm});
            skLineSegment(sketch, "E290", {"start": v(-0.52, 4.1) * mm, "end": v(-0.87, 4.7) * mm});
            skLineSegment(sketch, "E291", {"start": v(-1.04, 4.8) * mm, "end": v(-1.73, 4.8) * mm});
            skLineSegment(sketch, "E292", {"start": v(-1.9, 4.7) * mm, "end": v(-2.25, 4.1) * mm});
            skLineSegment(sketch, "E293", {"start": v(-2.25, 3.9) * mm, "end": v(-1.9, 3.3) * mm});
            skArc(sketch, "E294.filletArc", {"start": v(-1.73, 4.8) * mm, "mid": v(-1.83, 4.77) * mm, "end": v(-1.9, 4.7) * mm});
            skArc(sketch, "E295.filletArc", {"start": v(-2.25, 4.1) * mm, "mid": v(-2.28, 4) * mm, "end": v(-2.25, 3.9) * mm});
            skArc(sketch, "E296.filletArc", {"start": v(-1.9, 3.3) * mm, "mid": v(-1.83, 3.23) * mm, "end": v(-1.73, 3.2) * mm});
            skArc(sketch, "E297.filletArc", {"start": v(-1.04, 3.2) * mm, "mid": v(-0.94, 3.23) * mm, "end": v(-0.87, 3.3) * mm});
            skArc(sketch, "E298.filletArc", {"start": v(-0.52, 3.9) * mm, "mid": v(-0.5, 4) * mm, "end": v(-0.52, 4.1) * mm});
            skArc(sketch, "E299.filletArc", {"start": v(-0.87, 4.7) * mm, "mid": v(-0.94, 4.77) * mm, "end": v(-1.04, 4.8) * mm});
            skLineSegment(sketch, "E300", {"start": v(-3.12, 2.4) * mm, "end": v(-2.42, 2.4) * mm});
            skLineSegment(sketch, "E301", {"start": v(-2.25, 2.5) * mm, "end": v(-1.9, 3.1) * mm});
            skLineSegment(sketch, "E302", {"start": v(-1.9, 3.3) * mm, "end": v(-2.25, 3.9) * mm});
            skLineSegment(sketch, "E303", {"start": v(-2.42, 4) * mm, "end": v(-3.12, 4) * mm});
            skLineSegment(sketch, "E304", {"start": v(-3.3, 3.9) * mm, "end": v(-3.64, 3.3) * mm});
            skLineSegment(sketch, "E305", {"start": v(-3.64, 3.1) * mm, "end": v(-3.3, 2.5) * mm});
            skArc(sketch, "E306.filletArc", {"start": v(-3.12, 4) * mm, "mid": v(-3.22, 3.97) * mm, "end": v(-3.3, 3.9) * mm});
            skArc(sketch, "E307.filletArc", {"start": v(-3.64, 3.3) * mm, "mid": v(-3.66, 3.2) * mm, "end": v(-3.64, 3.1) * mm});
            skArc(sketch, "E308.filletArc", {"start": v(-3.3, 2.5) * mm, "mid": v(-3.22, 2.43) * mm, "end": v(-3.12, 2.4) * mm});
            skArc(sketch, "E309.filletArc", {"start": v(-2.42, 2.4) * mm, "mid": v(-2.32, 2.43) * mm, "end": v(-2.25, 2.5) * mm});
            skArc(sketch, "E310.filletArc", {"start": v(-1.9, 3.1) * mm, "mid": v(-1.88, 3.2) * mm, "end": v(-1.9, 3.3) * mm});
            skArc(sketch, "E311.filletArc", {"start": v(-2.25, 3.9) * mm, "mid": v(-2.32, 3.97) * mm, "end": v(-2.42, 4) * mm});
            skLineSegment(sketch, "E312", {"start": v(-4.5, 1.6) * mm, "end": v(-3.81, 1.6) * mm});
            skLineSegment(sketch, "E313", {"start": v(-3.64, 1.7) * mm, "end": v(-3.3, 2.3) * mm});
            skLineSegment(sketch, "E314", {"start": v(-3.3, 2.5) * mm, "end": v(-3.64, 3.1) * mm});
            skLineSegment(sketch, "E315", {"start": v(-3.81, 3.2) * mm, "end": v(-4.5, 3.2) * mm});
            skLineSegment(sketch, "E316", {"start": v(-4.68, 3.1) * mm, "end": v(-5.02, 2.5) * mm});
            skLineSegment(sketch, "E317", {"start": v(-5.02, 2.3) * mm, "end": v(-4.68, 1.7) * mm});
            skArc(sketch, "E318.filletArc", {"start": v(-4.5, 3.2) * mm, "mid": v(-4.6, 3.17) * mm, "end": v(-4.68, 3.1) * mm});
            skArc(sketch, "E319.filletArc", {"start": v(-5.02, 2.5) * mm, "mid": v(-5.05, 2.4) * mm, "end": v(-5.02, 2.3) * mm});
            skArc(sketch, "E320.filletArc", {"start": v(-4.68, 1.7) * mm, "mid": v(-4.6, 1.63) * mm, "end": v(-4.5, 1.6) * mm});
            skArc(sketch, "E321.filletArc", {"start": v(-3.81, 1.6) * mm, "mid": v(-3.71, 1.63) * mm, "end": v(-3.64, 1.7) * mm});
            skArc(sketch, "E322.filletArc", {"start": v(-3.3, 2.3) * mm, "mid": v(-3.26, 2.4) * mm, "end": v(-3.3, 2.5) * mm});
            skArc(sketch, "E323.filletArc", {"start": v(-3.64, 3.1) * mm, "mid": v(-3.71, 3.17) * mm, "end": v(-3.81, 3.2) * mm});
            skLineSegment(sketch, "E324", {"start": v(-4.5, 0) * mm, "end": v(-3.81, 0) * mm});
            skLineSegment(sketch, "E325", {"start": v(-3.64, 0.1) * mm, "end": v(-3.3, 0.7) * mm});
            skLineSegment(sketch, "E326", {"start": v(-3.3, 0.9) * mm, "end": v(-3.64, 1.5) * mm});
            skLineSegment(sketch, "E327", {"start": v(-3.81, 1.6) * mm, "end": v(-4.5, 1.6) * mm});
            skLineSegment(sketch, "E328", {"start": v(-4.68, 1.5) * mm, "end": v(-5.02, 0.9) * mm});
            skLineSegment(sketch, "E329", {"start": v(-5.02, 0.7) * mm, "end": v(-4.68, 0.1) * mm});
            skArc(sketch, "E330.filletArc", {"start": v(-4.5, 1.6) * mm, "mid": v(-4.6, 1.57) * mm, "end": v(-4.68, 1.5) * mm});
            skArc(sketch, "E331.filletArc", {"start": v(-5.02, 0.9) * mm, "mid": v(-5.05, 0.8) * mm, "end": v(-5.02, 0.7) * mm});
            skArc(sketch, "E332.filletArc", {"start": v(-4.68, 0.1) * mm, "mid": v(-4.6, 0.03) * mm, "end": v(-4.5, 0) * mm});
            skArc(sketch, "E333.filletArc", {"start": v(-3.81, 0) * mm, "mid": v(-3.71, 0.03) * mm, "end": v(-3.64, 0.1) * mm});
            skArc(sketch, "E334.filletArc", {"start": v(-3.3, 0.7) * mm, "mid": v(-3.26, 0.8) * mm, "end": v(-3.3, 0.9) * mm});
            skArc(sketch, "E335.filletArc", {"start": v(-3.64, 1.5) * mm, "mid": v(-3.71, 1.57) * mm, "end": v(-3.81, 1.6) * mm});
            skLineSegment(sketch, "E336", {"start": v(-4.5, -1.6) * mm, "end": v(-3.81, -1.6) * mm});
            skLineSegment(sketch, "E337", {"start": v(-3.64, -1.5) * mm, "end": v(-3.3, -0.9) * mm});
            skLineSegment(sketch, "E338", {"start": v(-3.3, -0.7) * mm, "end": v(-3.64, -0.1) * mm});
            skLineSegment(sketch, "E339", {"start": v(-3.81, 0) * mm, "end": v(-4.5, 0) * mm});
            skLineSegment(sketch, "E340", {"start": v(-4.68, -0.1) * mm, "end": v(-5.02, -0.7) * mm});
            skLineSegment(sketch, "E341", {"start": v(-5.02, -0.9) * mm, "end": v(-4.68, -1.5) * mm});
            skArc(sketch, "E342.filletArc", {"start": v(-4.5, 0) * mm, "mid": v(-4.6, -0.03) * mm, "end": v(-4.68, -0.1) * mm});
            skArc(sketch, "E343.filletArc", {"start": v(-5.02, -0.7) * mm, "mid": v(-5.05, -0.8) * mm, "end": v(-5.02, -0.9) * mm});
            skArc(sketch, "E344.filletArc", {"start": v(-4.68, -1.5) * mm, "mid": v(-4.6, -1.57) * mm, "end": v(-4.5, -1.6) * mm});
            skArc(sketch, "E345.filletArc", {"start": v(-3.81, -1.6) * mm, "mid": v(-3.71, -1.57) * mm, "end": v(-3.64, -1.5) * mm});
            skArc(sketch, "E346.filletArc", {"start": v(-3.3, -0.9) * mm, "mid": v(-3.26, -0.8) * mm, "end": v(-3.3, -0.7) * mm});
            skArc(sketch, "E347.filletArc", {"start": v(-3.64, -0.1) * mm, "mid": v(-3.71, -0.03) * mm, "end": v(-3.81, 0) * mm});
            skLineSegment(sketch, "E348", {"start": v(-4.5, -3.2) * mm, "end": v(-3.81, -3.2) * mm});
            skLineSegment(sketch, "E349", {"start": v(-3.64, -3.1) * mm, "end": v(-3.3, -2.5) * mm});
            skLineSegment(sketch, "E350", {"start": v(-3.3, -2.3) * mm, "end": v(-3.64, -1.7) * mm});
            skLineSegment(sketch, "E351", {"start": v(-3.81, -1.6) * mm, "end": v(-4.5, -1.6) * mm});
            skLineSegment(sketch, "E352", {"start": v(-4.68, -1.7) * mm, "end": v(-5.02, -2.3) * mm});
            skLineSegment(sketch, "E353", {"start": v(-5.02, -2.5) * mm, "end": v(-4.68, -3.1) * mm});
            skArc(sketch, "E354.filletArc", {"start": v(-4.5, -1.6) * mm, "mid": v(-4.6, -1.63) * mm, "end": v(-4.68, -1.7) * mm});
            skArc(sketch, "E355.filletArc", {"start": v(-5.02, -2.3) * mm, "mid": v(-5.05, -2.4) * mm, "end": v(-5.02, -2.5) * mm});
            skArc(sketch, "E356.filletArc", {"start": v(-4.68, -3.1) * mm, "mid": v(-4.6, -3.17) * mm, "end": v(-4.5, -3.2) * mm});
            skArc(sketch, "E357.filletArc", {"start": v(-3.81, -3.2) * mm, "mid": v(-3.71, -3.17) * mm, "end": v(-3.64, -3.1) * mm});
            skArc(sketch, "E358.filletArc", {"start": v(-3.3, -2.5) * mm, "mid": v(-3.26, -2.4) * mm, "end": v(-3.3, -2.3) * mm});
            skArc(sketch, "E359.filletArc", {"start": v(-3.64, -1.7) * mm, "mid": v(-3.71, -1.63) * mm, "end": v(-3.81, -1.6) * mm});
            skLineSegment(sketch, "E360", {"start": v(-3.12, -4) * mm, "end": v(-2.42, -4) * mm});
            skLineSegment(sketch, "E361", {"start": v(-2.25, -3.9) * mm, "end": v(-1.9, -3.3) * mm});
            skLineSegment(sketch, "E362", {"start": v(-1.9, -3.1) * mm, "end": v(-2.25, -2.5) * mm});
            skLineSegment(sketch, "E363", {"start": v(-2.42, -2.4) * mm, "end": v(-3.12, -2.4) * mm});
            skLineSegment(sketch, "E364", {"start": v(-3.3, -2.5) * mm, "end": v(-3.64, -3.1) * mm});
            skLineSegment(sketch, "E365", {"start": v(-3.64, -3.3) * mm, "end": v(-3.3, -3.9) * mm});
            skArc(sketch, "E366.filletArc", {"start": v(-3.12, -2.4) * mm, "mid": v(-3.22, -2.43) * mm, "end": v(-3.3, -2.5) * mm});
            skArc(sketch, "E367.filletArc", {"start": v(-3.64, -3.1) * mm, "mid": v(-3.66, -3.2) * mm, "end": v(-3.64, -3.3) * mm});
            skArc(sketch, "E368.filletArc", {"start": v(-3.3, -3.9) * mm, "mid": v(-3.22, -3.97) * mm, "end": v(-3.12, -4) * mm});
            skArc(sketch, "E369.filletArc", {"start": v(-2.42, -4) * mm, "mid": v(-2.32, -3.97) * mm, "end": v(-2.25, -3.9) * mm});
            skArc(sketch, "E370.filletArc", {"start": v(-1.9, -3.3) * mm, "mid": v(-1.88, -3.2) * mm, "end": v(-1.9, -3.1) * mm});
            skArc(sketch, "E371.filletArc", {"start": v(-2.25, -2.5) * mm, "mid": v(-2.32, -2.43) * mm, "end": v(-2.42, -2.4) * mm});
            skLineSegment(sketch, "E372", {"start": v(-1.73, -4.8) * mm, "end": v(-1.04, -4.8) * mm});
            skLineSegment(sketch, "E373", {"start": v(-0.87, -4.7) * mm, "end": v(-0.52, -4.1) * mm});
            skLineSegment(sketch, "E374", {"start": v(-0.52, -3.9) * mm, "end": v(-0.87, -3.3) * mm});
            skLineSegment(sketch, "E375", {"start": v(-1.04, -3.2) * mm, "end": v(-1.73, -3.2) * mm});
            skLineSegment(sketch, "E376", {"start": v(-1.9, -3.3) * mm, "end": v(-2.25, -3.9) * mm});
            skLineSegment(sketch, "E377", {"start": v(-2.25, -4.1) * mm, "end": v(-1.9, -4.7) * mm});
            skArc(sketch, "E378.filletArc", {"start": v(-1.73, -3.2) * mm, "mid": v(-1.83, -3.23) * mm, "end": v(-1.9, -3.3) * mm});
            skArc(sketch, "E379.filletArc", {"start": v(-2.25, -3.9) * mm, "mid": v(-2.28, -4) * mm, "end": v(-2.25, -4.1) * mm});
            skArc(sketch, "E380.filletArc", {"start": v(-1.9, -4.7) * mm, "mid": v(-1.83, -4.77) * mm, "end": v(-1.73, -4.8) * mm});
            skArc(sketch, "E381.filletArc", {"start": v(-1.04, -4.8) * mm, "mid": v(-0.94, -4.77) * mm, "end": v(-0.87, -4.7) * mm});
            skArc(sketch, "E382.filletArc", {"start": v(-0.52, -4.1) * mm, "mid": v(-0.5, -4) * mm, "end": v(-0.52, -3.9) * mm});
            skArc(sketch, "E383.filletArc", {"start": v(-0.87, -3.3) * mm, "mid": v(-0.94, -3.23) * mm, "end": v(-1.04, -3.2) * mm});
            skLineSegment(sketch, "E384", {"start": v(-0.35, -5.6) * mm, "end": v(0.35, -5.6) * mm});
            skLineSegment(sketch, "E385", {"start": v(0.52, -5.5) * mm, "end": v(0.87, -4.9) * mm});
            skLineSegment(sketch, "E386", {"start": v(0.87, -4.7) * mm, "end": v(0.52, -4.1) * mm});
            skLineSegment(sketch, "E387", {"start": v(0.35, -4) * mm, "end": v(-0.35, -4) * mm});
            skLineSegment(sketch, "E388", {"start": v(-0.52, -4.1) * mm, "end": v(-0.87, -4.7) * mm});
            skLineSegment(sketch, "E389", {"start": v(-0.87, -4.9) * mm, "end": v(-0.52, -5.5) * mm});
            skArc(sketch, "E390.filletArc", {"start": v(-0.35, -4) * mm, "mid": v(-0.45, -4.03) * mm, "end": v(-0.52, -4.1) * mm});
            skArc(sketch, "E391.filletArc", {"start": v(-0.87, -4.7) * mm, "mid": v(-0.9, -4.8) * mm, "end": v(-0.87, -4.9) * mm});
            skArc(sketch, "E392.filletArc", {"start": v(-0.52, -5.5) * mm, "mid": v(-0.45, -5.57) * mm, "end": v(-0.35, -5.6) * mm});
            skArc(sketch, "E393.filletArc", {"start": v(0.35, -5.6) * mm, "mid": v(0.45, -5.57) * mm, "end": v(0.52, -5.5) * mm});
            skArc(sketch, "E394.filletArc", {"start": v(0.87, -4.9) * mm, "mid": v(0.9, -4.8) * mm, "end": v(0.87, -4.7) * mm});
            skArc(sketch, "E395.filletArc", {"start": v(0.52, -4.1) * mm, "mid": v(0.45, -4.03) * mm, "end": v(0.35, -4) * mm});
            skLineSegment(sketch, "E396", {"start": v(1.04, -4.8) * mm, "end": v(1.73, -4.8) * mm});
            skLineSegment(sketch, "E397", {"start": v(1.9, -4.7) * mm, "end": v(2.25, -4.1) * mm});
            skLineSegment(sketch, "E398", {"start": v(2.25, -3.9) * mm, "end": v(1.9, -3.3) * mm});
            skLineSegment(sketch, "E399", {"start": v(1.73, -3.2) * mm, "end": v(1.04, -3.2) * mm});
            skLineSegment(sketch, "E400", {"start": v(0.87, -3.3) * mm, "end": v(0.52, -3.9) * mm});
            skLineSegment(sketch, "E401", {"start": v(0.52, -4.1) * mm, "end": v(0.87, -4.7) * mm});
            skArc(sketch, "E402.filletArc", {"start": v(1.04, -3.2) * mm, "mid": v(0.94, -3.23) * mm, "end": v(0.87, -3.3) * mm});
            skArc(sketch, "E403.filletArc", {"start": v(0.52, -3.9) * mm, "mid": v(0.5, -4) * mm, "end": v(0.52, -4.1) * mm});
            skArc(sketch, "E404.filletArc", {"start": v(0.87, -4.7) * mm, "mid": v(0.94, -4.77) * mm, "end": v(1.04, -4.8) * mm});
            skArc(sketch, "E405.filletArc", {"start": v(1.73, -4.8) * mm, "mid": v(1.83, -4.77) * mm, "end": v(1.9, -4.7) * mm});
            skArc(sketch, "E406.filletArc", {"start": v(2.25, -4.1) * mm, "mid": v(2.28, -4) * mm, "end": v(2.25, -3.9) * mm});
            skArc(sketch, "E407.filletArc", {"start": v(1.9, -3.3) * mm, "mid": v(1.83, -3.23) * mm, "end": v(1.73, -3.2) * mm});
            skLineSegment(sketch, "E408", {"start": v(2.42, -4) * mm, "end": v(3.12, -4) * mm});
            skLineSegment(sketch, "E409", {"start": v(3.3, -3.9) * mm, "end": v(3.64, -3.3) * mm});
            skLineSegment(sketch, "E410", {"start": v(3.64, -3.1) * mm, "end": v(3.3, -2.5) * mm});
            skLineSegment(sketch, "E411", {"start": v(3.12, -2.4) * mm, "end": v(2.42, -2.4) * mm});
            skLineSegment(sketch, "E412", {"start": v(2.25, -2.5) * mm, "end": v(1.9, -3.1) * mm});
            skLineSegment(sketch, "E413", {"start": v(1.9, -3.3) * mm, "end": v(2.25, -3.9) * mm});
            skArc(sketch, "E414.filletArc", {"start": v(2.42, -2.4) * mm, "mid": v(2.32, -2.43) * mm, "end": v(2.25, -2.5) * mm});
            skArc(sketch, "E415.filletArc", {"start": v(1.9, -3.1) * mm, "mid": v(1.88, -3.2) * mm, "end": v(1.9, -3.3) * mm});
            skArc(sketch, "E416.filletArc", {"start": v(2.25, -3.9) * mm, "mid": v(2.32, -3.97) * mm, "end": v(2.42, -4) * mm});
            skArc(sketch, "E417.filletArc", {"start": v(3.12, -4) * mm, "mid": v(3.22, -3.97) * mm, "end": v(3.3, -3.9) * mm});
            skArc(sketch, "E418.filletArc", {"start": v(3.64, -3.3) * mm, "mid": v(3.66, -3.2) * mm, "end": v(3.64, -3.1) * mm});
            skArc(sketch, "E419.filletArc", {"start": v(3.3, -2.5) * mm, "mid": v(3.22, -2.43) * mm, "end": v(3.12, -2.4) * mm});
            skLineSegment(sketch, "E420", {"start": v(3.81, -3.2) * mm, "end": v(4.5, -3.2) * mm});
            skLineSegment(sketch, "E421", {"start": v(4.68, -3.1) * mm, "end": v(5.02, -2.5) * mm});
            skLineSegment(sketch, "E422", {"start": v(5.02, -2.3) * mm, "end": v(4.68, -1.7) * mm});
            skLineSegment(sketch, "E423", {"start": v(4.5, -1.6) * mm, "end": v(3.81, -1.6) * mm});
            skLineSegment(sketch, "E424", {"start": v(3.64, -1.7) * mm, "end": v(3.3, -2.3) * mm});
            skLineSegment(sketch, "E425", {"start": v(3.3, -2.5) * mm, "end": v(3.64, -3.1) * mm});
            skArc(sketch, "E426.filletArc", {"start": v(3.81, -1.6) * mm, "mid": v(3.71, -1.63) * mm, "end": v(3.64, -1.7) * mm});
            skArc(sketch, "E427.filletArc", {"start": v(3.3, -2.3) * mm, "mid": v(3.26, -2.4) * mm, "end": v(3.3, -2.5) * mm});
            skArc(sketch, "E428.filletArc", {"start": v(3.64, -3.1) * mm, "mid": v(3.71, -3.17) * mm, "end": v(3.81, -3.2) * mm});
            skArc(sketch, "E429.filletArc", {"start": v(4.5, -3.2) * mm, "mid": v(4.6, -3.17) * mm, "end": v(4.68, -3.1) * mm});
            skArc(sketch, "E430.filletArc", {"start": v(5.02, -2.5) * mm, "mid": v(5.05, -2.4) * mm, "end": v(5.02, -2.3) * mm});
            skArc(sketch, "E431.filletArc", {"start": v(4.68, -1.7) * mm, "mid": v(4.6, -1.63) * mm, "end": v(4.5, -1.6) * mm});
            skLineSegment(sketch, "E432", {"start": v(-0.35, 4) * mm, "end": v(0.35, 4) * mm});
            skLineSegment(sketch, "E433", {"start": v(0.52, 4.1) * mm, "end": v(0.87, 4.7) * mm});
            skLineSegment(sketch, "E434", {"start": v(0.87, 4.9) * mm, "end": v(0.52, 5.5) * mm});
            skLineSegment(sketch, "E435", {"start": v(0.35, 5.6) * mm, "end": v(-0.35, 5.6) * mm});
            skLineSegment(sketch, "E436", {"start": v(-0.52, 5.5) * mm, "end": v(-0.87, 4.9) * mm});
            skLineSegment(sketch, "E437", {"start": v(-0.87, 4.7) * mm, "end": v(-0.52, 4.1) * mm});
            skArc(sketch, "E438.filletArc", {"start": v(-0.35, 5.6) * mm, "mid": v(-0.45, 5.57) * mm, "end": v(-0.52, 5.5) * mm});
            skArc(sketch, "E439.filletArc", {"start": v(-0.87, 4.9) * mm, "mid": v(-0.9, 4.8) * mm, "end": v(-0.87, 4.7) * mm});
            skArc(sketch, "E440.filletArc", {"start": v(-0.52, 4.1) * mm, "mid": v(-0.45, 4.03) * mm, "end": v(-0.35, 4) * mm});
            skArc(sketch, "E441.filletArc", {"start": v(0.35, 4) * mm, "mid": v(0.45, 4.03) * mm, "end": v(0.52, 4.1) * mm});
            skArc(sketch, "E442.filletArc", {"start": v(0.87, 4.7) * mm, "mid": v(0.9, 4.8) * mm, "end": v(0.87, 4.9) * mm});
            skArc(sketch, "E443.filletArc", {"start": v(0.52, 5.5) * mm, "mid": v(0.45, 5.57) * mm, "end": v(0.35, 5.6) * mm});
            skLineSegment(sketch, "E444", {"start": v(-5.89, 0.8) * mm, "end": v(-5.2, 0.8) * mm});
            skLineSegment(sketch, "E445", {"start": v(-5.02, 0.9) * mm, "end": v(-4.68, 1.5) * mm});
            skLineSegment(sketch, "E446", {"start": v(-4.68, 1.7) * mm, "end": v(-5.02, 2.3) * mm});
            skLineSegment(sketch, "E447", {"start": v(-5.2, 2.4) * mm, "end": v(-5.89, 2.4) * mm});
            skLineSegment(sketch, "E448", {"start": v(-6.06, 2.3) * mm, "end": v(-6.4, 1.7) * mm});
            skLineSegment(sketch, "E449", {"start": v(-6.4, 1.5) * mm, "end": v(-6.06, 0.9) * mm});
            skArc(sketch, "E450.filletArc", {"start": v(-5.89, 2.4) * mm, "mid": v(-5.99, 2.37) * mm, "end": v(-6.06, 2.3) * mm});
            skArc(sketch, "E451.filletArc", {"start": v(-6.4, 1.7) * mm, "mid": v(-6.44, 1.6) * mm, "end": v(-6.4, 1.5) * mm});
            skArc(sketch, "E452.filletArc", {"start": v(-6.06, 0.9) * mm, "mid": v(-5.99, 0.83) * mm, "end": v(-5.89, 0.8) * mm});
            skArc(sketch, "E453.filletArc", {"start": v(-5.2, 0.8) * mm, "mid": v(-5.1, 0.83) * mm, "end": v(-5.02, 0.9) * mm});
            skArc(sketch, "E454.filletArc", {"start": v(-4.68, 1.5) * mm, "mid": v(-4.65, 1.6) * mm, "end": v(-4.68, 1.7) * mm});
            skArc(sketch, "E455.filletArc", {"start": v(-5.02, 2.3) * mm, "mid": v(-5.1, 2.37) * mm, "end": v(-5.2, 2.4) * mm});
            skLineSegment(sketch, "E456", {"start": v(-5.89, -0.8) * mm, "end": v(-5.2, -0.8) * mm});
            skLineSegment(sketch, "E457", {"start": v(-5.02, -0.7) * mm, "end": v(-4.68, -0.1) * mm});
            skLineSegment(sketch, "E458", {"start": v(-4.68, 0.1) * mm, "end": v(-5.02, 0.7) * mm});
            skLineSegment(sketch, "E459", {"start": v(-5.2, 0.8) * mm, "end": v(-5.89, 0.8) * mm});
            skLineSegment(sketch, "E460", {"start": v(-6.06, 0.7) * mm, "end": v(-6.4, 0.1) * mm});
            skLineSegment(sketch, "E461", {"start": v(-6.4, -0.1) * mm, "end": v(-6.06, -0.7) * mm});
            skArc(sketch, "E462.filletArc", {"start": v(-5.89, 0.8) * mm, "mid": v(-5.99, 0.77) * mm, "end": v(-6.06, 0.7) * mm});
            skArc(sketch, "E463.filletArc", {"start": v(-6.4, 0.1) * mm, "mid": v(-6.44, 0) * mm, "end": v(-6.4, -0.1) * mm});
            skArc(sketch, "E464.filletArc", {"start": v(-6.06, -0.7) * mm, "mid": v(-5.99, -0.77) * mm, "end": v(-5.89, -0.8) * mm});
            skArc(sketch, "E465.filletArc", {"start": v(-5.2, -0.8) * mm, "mid": v(-5.1, -0.77) * mm, "end": v(-5.02, -0.7) * mm});
            skArc(sketch, "E466.filletArc", {"start": v(-4.68, -0.1) * mm, "mid": v(-4.65, 0) * mm, "end": v(-4.68, 0.1) * mm});
            skArc(sketch, "E467.filletArc", {"start": v(-5.02, 0.7) * mm, "mid": v(-5.1, 0.77) * mm, "end": v(-5.2, 0.8) * mm});
            skLineSegment(sketch, "E468", {"start": v(-5.89, -2.4) * mm, "end": v(-5.2, -2.4) * mm});
            skLineSegment(sketch, "E469", {"start": v(-5.02, -2.3) * mm, "end": v(-4.68, -1.7) * mm});
            skLineSegment(sketch, "E470", {"start": v(-4.68, -1.5) * mm, "end": v(-5.02, -0.9) * mm});
            skLineSegment(sketch, "E471", {"start": v(-5.2, -0.8) * mm, "end": v(-5.89, -0.8) * mm});
            skLineSegment(sketch, "E472", {"start": v(-6.06, -0.9) * mm, "end": v(-6.4, -1.5) * mm});
            skLineSegment(sketch, "E473", {"start": v(-6.4, -1.7) * mm, "end": v(-6.06, -2.3) * mm});
            skArc(sketch, "E474.filletArc", {"start": v(-5.89, -0.8) * mm, "mid": v(-5.99, -0.83) * mm, "end": v(-6.06, -0.9) * mm});
            skArc(sketch, "E475.filletArc", {"start": v(-6.4, -1.5) * mm, "mid": v(-6.44, -1.6) * mm, "end": v(-6.4, -1.7) * mm});
            skArc(sketch, "E476.filletArc", {"start": v(-6.06, -2.3) * mm, "mid": v(-5.99, -2.37) * mm, "end": v(-5.89, -2.4) * mm});
            skArc(sketch, "E477.filletArc", {"start": v(-5.2, -2.4) * mm, "mid": v(-5.1, -2.37) * mm, "end": v(-5.02, -2.3) * mm});
            skArc(sketch, "E478.filletArc", {"start": v(-4.68, -1.7) * mm, "mid": v(-4.65, -1.6) * mm, "end": v(-4.68, -1.5) * mm});
            skArc(sketch, "E479.filletArc", {"start": v(-5.02, -0.9) * mm, "mid": v(-5.1, -0.83) * mm, "end": v(-5.2, -0.8) * mm});
            skLineSegment(sketch, "E480", {"start": v(-5.89, -4) * mm, "end": v(-5.2, -4) * mm});
            skLineSegment(sketch, "E481", {"start": v(-5.02, -3.9) * mm, "end": v(-4.68, -3.3) * mm});
            skLineSegment(sketch, "E482", {"start": v(-4.68, -3.1) * mm, "end": v(-5.02, -2.5) * mm});
            skLineSegment(sketch, "E483", {"start": v(-5.2, -2.4) * mm, "end": v(-5.89, -2.4) * mm});
            skLineSegment(sketch, "E484", {"start": v(-6.06, -2.5) * mm, "end": v(-6.4, -3.1) * mm});
            skLineSegment(sketch, "E485", {"start": v(-6.4, -3.3) * mm, "end": v(-6.06, -3.9) * mm});
            skArc(sketch, "E486.filletArc", {"start": v(-5.89, -2.4) * mm, "mid": v(-5.99, -2.43) * mm, "end": v(-6.06, -2.5) * mm});
            skArc(sketch, "E487.filletArc", {"start": v(-6.4, -3.1) * mm, "mid": v(-6.44, -3.2) * mm, "end": v(-6.4, -3.3) * mm});
            skArc(sketch, "E488.filletArc", {"start": v(-6.06, -3.9) * mm, "mid": v(-5.99, -3.97) * mm, "end": v(-5.89, -4) * mm});
            skArc(sketch, "E489.filletArc", {"start": v(-5.2, -4) * mm, "mid": v(-5.1, -3.97) * mm, "end": v(-5.02, -3.9) * mm});
            skArc(sketch, "E490.filletArc", {"start": v(-4.68, -3.3) * mm, "mid": v(-4.65, -3.2) * mm, "end": v(-4.68, -3.1) * mm});
            skArc(sketch, "E491.filletArc", {"start": v(-5.02, -2.5) * mm, "mid": v(-5.1, -2.43) * mm, "end": v(-5.2, -2.4) * mm});
            skLineSegment(sketch, "E492", {"start": v(-4.5, -4.8) * mm, "end": v(-3.81, -4.8) * mm});
            skLineSegment(sketch, "E493", {"start": v(-3.64, -4.7) * mm, "end": v(-3.3, -4.1) * mm});
            skLineSegment(sketch, "E494", {"start": v(-3.3, -3.9) * mm, "end": v(-3.64, -3.3) * mm});
            skLineSegment(sketch, "E495", {"start": v(-3.81, -3.2) * mm, "end": v(-4.5, -3.2) * mm});
            skLineSegment(sketch, "E496", {"start": v(-4.68, -3.3) * mm, "end": v(-5.02, -3.9) * mm});
            skLineSegment(sketch, "E497", {"start": v(-5.02, -4.1) * mm, "end": v(-4.68, -4.7) * mm});
            skArc(sketch, "E498.filletArc", {"start": v(-4.5, -3.2) * mm, "mid": v(-4.6, -3.23) * mm, "end": v(-4.68, -3.3) * mm});
            skArc(sketch, "E499.filletArc", {"start": v(-5.02, -3.9) * mm, "mid": v(-5.05, -4) * mm, "end": v(-5.02, -4.1) * mm});
            skArc(sketch, "E500.filletArc", {"start": v(-4.68, -4.7) * mm, "mid": v(-4.6, -4.77) * mm, "end": v(-4.5, -4.8) * mm});
            skArc(sketch, "E501.filletArc", {"start": v(-3.81, -4.8) * mm, "mid": v(-3.71, -4.77) * mm, "end": v(-3.64, -4.7) * mm});
            skArc(sketch, "E502.filletArc", {"start": v(-3.3, -4.1) * mm, "mid": v(-3.26, -4) * mm, "end": v(-3.3, -3.9) * mm});
            skArc(sketch, "E503.filletArc", {"start": v(-3.64, -3.3) * mm, "mid": v(-3.71, -3.23) * mm, "end": v(-3.81, -3.2) * mm});
            skLineSegment(sketch, "E504", {"start": v(-3.12, -5.6) * mm, "end": v(-2.42, -5.6) * mm});
            skLineSegment(sketch, "E505", {"start": v(-2.25, -5.5) * mm, "end": v(-1.9, -4.9) * mm});
            skLineSegment(sketch, "E506", {"start": v(-1.9, -4.7) * mm, "end": v(-2.25, -4.1) * mm});
            skLineSegment(sketch, "E507", {"start": v(-2.42, -4) * mm, "end": v(-3.12, -4) * mm});
            skLineSegment(sketch, "E508", {"start": v(-3.3, -4.1) * mm, "end": v(-3.64, -4.7) * mm});
            skLineSegment(sketch, "E509", {"start": v(-3.64, -4.9) * mm, "end": v(-3.3, -5.5) * mm});
            skArc(sketch, "E510.filletArc", {"start": v(-3.12, -4) * mm, "mid": v(-3.22, -4.03) * mm, "end": v(-3.3, -4.1) * mm});
            skArc(sketch, "E511.filletArc", {"start": v(-3.64, -4.7) * mm, "mid": v(-3.66, -4.8) * mm, "end": v(-3.64, -4.9) * mm});
            skArc(sketch, "E512.filletArc", {"start": v(-3.3, -5.5) * mm, "mid": v(-3.22, -5.57) * mm, "end": v(-3.12, -5.6) * mm});
            skArc(sketch, "E513.filletArc", {"start": v(-2.42, -5.6) * mm, "mid": v(-2.32, -5.57) * mm, "end": v(-2.25, -5.5) * mm});
            skArc(sketch, "E514.filletArc", {"start": v(-1.9, -4.9) * mm, "mid": v(-1.88, -4.8) * mm, "end": v(-1.9, -4.7) * mm});
            skArc(sketch, "E515.filletArc", {"start": v(-2.25, -4.1) * mm, "mid": v(-2.32, -4.03) * mm, "end": v(-2.42, -4) * mm});
            skLineSegment(sketch, "E516", {"start": v(-1.73, -6.4) * mm, "end": v(-1.04, -6.4) * mm});
            skLineSegment(sketch, "E517", {"start": v(-0.87, -6.3) * mm, "end": v(-0.52, -5.7) * mm});
            skLineSegment(sketch, "E518", {"start": v(-0.52, -5.5) * mm, "end": v(-0.87, -4.9) * mm});
            skLineSegment(sketch, "E519", {"start": v(-1.04, -4.8) * mm, "end": v(-1.73, -4.8) * mm});
            skLineSegment(sketch, "E520", {"start": v(-1.9, -4.9) * mm, "end": v(-2.25, -5.5) * mm});
            skLineSegment(sketch, "E521", {"start": v(-2.25, -5.7) * mm, "end": v(-1.9, -6.3) * mm});
            skArc(sketch, "E522.filletArc", {"start": v(-1.73, -4.8) * mm, "mid": v(-1.83, -4.83) * mm, "end": v(-1.9, -4.9) * mm});
            skArc(sketch, "E523.filletArc", {"start": v(-2.25, -5.5) * mm, "mid": v(-2.28, -5.6) * mm, "end": v(-2.25, -5.7) * mm});
            skArc(sketch, "E524.filletArc", {"start": v(-1.9, -6.3) * mm, "mid": v(-1.83, -6.37) * mm, "end": v(-1.73, -6.4) * mm});
            skArc(sketch, "E525.filletArc", {"start": v(-1.04, -6.4) * mm, "mid": v(-0.94, -6.37) * mm, "end": v(-0.87, -6.3) * mm});
            skArc(sketch, "E526.filletArc", {"start": v(-0.52, -5.7) * mm, "mid": v(-0.5, -5.6) * mm, "end": v(-0.52, -5.5) * mm});
            skArc(sketch, "E527.filletArc", {"start": v(-0.87, -4.9) * mm, "mid": v(-0.94, -4.83) * mm, "end": v(-1.04, -4.8) * mm});
            skLineSegment(sketch, "E528", {"start": v(-0.35, -7.2) * mm, "end": v(0.35, -7.2) * mm});
            skLineSegment(sketch, "E529", {"start": v(0.52, -7.1) * mm, "end": v(0.87, -6.5) * mm});
            skLineSegment(sketch, "E530", {"start": v(0.87, -6.3) * mm, "end": v(0.52, -5.7) * mm});
            skLineSegment(sketch, "E531", {"start": v(0.35, -5.6) * mm, "end": v(-0.35, -5.6) * mm});
            skLineSegment(sketch, "E532", {"start": v(-0.52, -5.7) * mm, "end": v(-0.87, -6.3) * mm});
            skLineSegment(sketch, "E533", {"start": v(-0.87, -6.5) * mm, "end": v(-0.52, -7.1) * mm});
            skArc(sketch, "E534.filletArc", {"start": v(-0.35, -5.6) * mm, "mid": v(-0.45, -5.63) * mm, "end": v(-0.52, -5.7) * mm});
            skArc(sketch, "E535.filletArc", {"start": v(-0.87, -6.3) * mm, "mid": v(-0.9, -6.4) * mm, "end": v(-0.87, -6.5) * mm});
            skArc(sketch, "E536.filletArc", {"start": v(-0.52, -7.1) * mm, "mid": v(-0.45, -7.17) * mm, "end": v(-0.35, -7.2) * mm});
            skArc(sketch, "E537.filletArc", {"start": v(0.35, -7.2) * mm, "mid": v(0.45, -7.17) * mm, "end": v(0.52, -7.1) * mm});
            skArc(sketch, "E538.filletArc", {"start": v(0.87, -6.5) * mm, "mid": v(0.9, -6.4) * mm, "end": v(0.87, -6.3) * mm});
            skArc(sketch, "E539.filletArc", {"start": v(0.52, -5.7) * mm, "mid": v(0.45, -5.63) * mm, "end": v(0.35, -5.6) * mm});
            skLineSegment(sketch, "E540", {"start": v(1.04, -6.4) * mm, "end": v(1.73, -6.4) * mm});
            skLineSegment(sketch, "E541", {"start": v(1.9, -6.3) * mm, "end": v(2.25, -5.7) * mm});
            skLineSegment(sketch, "E542", {"start": v(2.25, -5.5) * mm, "end": v(1.9, -4.9) * mm});
            skLineSegment(sketch, "E543", {"start": v(1.73, -4.8) * mm, "end": v(1.04, -4.8) * mm});
            skLineSegment(sketch, "E544", {"start": v(0.87, -4.9) * mm, "end": v(0.52, -5.5) * mm});
            skLineSegment(sketch, "E545", {"start": v(0.52, -5.7) * mm, "end": v(0.87, -6.3) * mm});
            skArc(sketch, "E546.filletArc", {"start": v(1.04, -4.8) * mm, "mid": v(0.94, -4.83) * mm, "end": v(0.87, -4.9) * mm});
            skArc(sketch, "E547.filletArc", {"start": v(0.52, -5.5) * mm, "mid": v(0.5, -5.6) * mm, "end": v(0.52, -5.7) * mm});
            skArc(sketch, "E548.filletArc", {"start": v(0.87, -6.3) * mm, "mid": v(0.94, -6.37) * mm, "end": v(1.04, -6.4) * mm});
            skArc(sketch, "E549.filletArc", {"start": v(1.73, -6.4) * mm, "mid": v(1.83, -6.37) * mm, "end": v(1.9, -6.3) * mm});
            skArc(sketch, "E550.filletArc", {"start": v(2.25, -5.7) * mm, "mid": v(2.28, -5.6) * mm, "end": v(2.25, -5.5) * mm});
            skArc(sketch, "E551.filletArc", {"start": v(1.9, -4.9) * mm, "mid": v(1.83, -4.83) * mm, "end": v(1.73, -4.8) * mm});
            skLineSegment(sketch, "E552", {"start": v(3.81, -4.8) * mm, "end": v(4.5, -4.8) * mm});
            skLineSegment(sketch, "E553", {"start": v(4.68, -4.7) * mm, "end": v(5.02, -4.1) * mm});
            skLineSegment(sketch, "E554", {"start": v(5.02, -3.9) * mm, "end": v(4.68, -3.3) * mm});
            skLineSegment(sketch, "E555", {"start": v(4.5, -3.2) * mm, "end": v(3.81, -3.2) * mm});
            skLineSegment(sketch, "E556", {"start": v(3.64, -3.3) * mm, "end": v(3.3, -3.9) * mm});
            skLineSegment(sketch, "E557", {"start": v(3.3, -4.1) * mm, "end": v(3.64, -4.7) * mm});
            skArc(sketch, "E558.filletArc", {"start": v(3.81, -3.2) * mm, "mid": v(3.71, -3.23) * mm, "end": v(3.64, -3.3) * mm});
            skArc(sketch, "E559.filletArc", {"start": v(3.3, -3.9) * mm, "mid": v(3.26, -4) * mm, "end": v(3.3, -4.1) * mm});
            skArc(sketch, "E560.filletArc", {"start": v(3.64, -4.7) * mm, "mid": v(3.71, -4.77) * mm, "end": v(3.81, -4.8) * mm});
            skArc(sketch, "E561.filletArc", {"start": v(4.5, -4.8) * mm, "mid": v(4.6, -4.77) * mm, "end": v(4.68, -4.7) * mm});
            skArc(sketch, "E562.filletArc", {"start": v(5.02, -4.1) * mm, "mid": v(5.05, -4) * mm, "end": v(5.02, -3.9) * mm});
            skArc(sketch, "E563.filletArc", {"start": v(4.68, -3.3) * mm, "mid": v(4.6, -3.23) * mm, "end": v(4.5, -3.2) * mm});
            skLineSegment(sketch, "E564", {"start": v(2.42, -5.6) * mm, "end": v(3.12, -5.6) * mm});
            skLineSegment(sketch, "E565", {"start": v(3.3, -5.5) * mm, "end": v(3.64, -4.9) * mm});
            skLineSegment(sketch, "E566", {"start": v(3.64, -4.7) * mm, "end": v(3.3, -4.1) * mm});
            skLineSegment(sketch, "E567", {"start": v(3.12, -4) * mm, "end": v(2.42, -4) * mm});
            skLineSegment(sketch, "E568", {"start": v(2.25, -4.1) * mm, "end": v(1.9, -4.7) * mm});
            skLineSegment(sketch, "E569", {"start": v(1.9, -4.9) * mm, "end": v(2.25, -5.5) * mm});
            skArc(sketch, "E570.filletArc", {"start": v(2.42, -4) * mm, "mid": v(2.32, -4.03) * mm, "end": v(2.25, -4.1) * mm});
            skArc(sketch, "E571.filletArc", {"start": v(1.9, -4.7) * mm, "mid": v(1.88, -4.8) * mm, "end": v(1.9, -4.9) * mm});
            skArc(sketch, "E572.filletArc", {"start": v(2.25, -5.5) * mm, "mid": v(2.32, -5.57) * mm, "end": v(2.42, -5.6) * mm});
            skArc(sketch, "E573.filletArc", {"start": v(3.12, -5.6) * mm, "mid": v(3.22, -5.57) * mm, "end": v(3.3, -5.5) * mm});
            skArc(sketch, "E574.filletArc", {"start": v(3.64, -4.9) * mm, "mid": v(3.66, -4.8) * mm, "end": v(3.64, -4.7) * mm});
            skArc(sketch, "E575.filletArc", {"start": v(3.3, -4.1) * mm, "mid": v(3.22, -4.03) * mm, "end": v(3.12, -4) * mm});
            skLineSegment(sketch, "E576", {"start": v(5.2, -4) * mm, "end": v(5.89, -4) * mm});
            skLineSegment(sketch, "E577", {"start": v(6.06, -3.9) * mm, "end": v(6.4, -3.3) * mm});
            skLineSegment(sketch, "E578", {"start": v(6.4, -3.1) * mm, "end": v(6.06, -2.5) * mm});
            skLineSegment(sketch, "E579", {"start": v(5.89, -2.4) * mm, "end": v(5.2, -2.4) * mm});
            skLineSegment(sketch, "E580", {"start": v(5.02, -2.5) * mm, "end": v(4.68, -3.1) * mm});
            skLineSegment(sketch, "E581", {"start": v(4.68, -3.3) * mm, "end": v(5.02, -3.9) * mm});
            skArc(sketch, "E582.filletArc", {"start": v(5.2, -2.4) * mm, "mid": v(5.1, -2.43) * mm, "end": v(5.02, -2.5) * mm});
            skArc(sketch, "E583.filletArc", {"start": v(4.68, -3.1) * mm, "mid": v(4.65, -3.2) * mm, "end": v(4.68, -3.3) * mm});
            skArc(sketch, "E584.filletArc", {"start": v(5.02, -3.9) * mm, "mid": v(5.1, -3.97) * mm, "end": v(5.2, -4) * mm});
            skArc(sketch, "E585.filletArc", {"start": v(5.89, -4) * mm, "mid": v(5.99, -3.97) * mm, "end": v(6.06, -3.9) * mm});
            skArc(sketch, "E586.filletArc", {"start": v(6.4, -3.3) * mm, "mid": v(6.44, -3.2) * mm, "end": v(6.4, -3.1) * mm});
            skArc(sketch, "E587.filletArc", {"start": v(6.06, -2.5) * mm, "mid": v(5.99, -2.43) * mm, "end": v(5.89, -2.4) * mm});
            skLineSegment(sketch, "E588", {"start": v(5.2, -2.4) * mm, "end": v(5.89, -2.4) * mm});
            skLineSegment(sketch, "E589", {"start": v(6.06, -2.3) * mm, "end": v(6.4, -1.7) * mm});
            skLineSegment(sketch, "E590", {"start": v(6.4, -1.5) * mm, "end": v(6.06, -0.9) * mm});
            skLineSegment(sketch, "E591", {"start": v(5.89, -0.8) * mm, "end": v(5.2, -0.8) * mm});
            skLineSegment(sketch, "E592", {"start": v(5.02, -0.9) * mm, "end": v(4.68, -1.5) * mm});
            skLineSegment(sketch, "E593", {"start": v(4.68, -1.7) * mm, "end": v(5.02, -2.3) * mm});
            skArc(sketch, "E594.filletArc", {"start": v(5.2, -0.8) * mm, "mid": v(5.1, -0.83) * mm, "end": v(5.02, -0.9) * mm});
            skArc(sketch, "E595.filletArc", {"start": v(4.68, -1.5) * mm, "mid": v(4.65, -1.6) * mm, "end": v(4.68, -1.7) * mm});
            skArc(sketch, "E596.filletArc", {"start": v(5.02, -2.3) * mm, "mid": v(5.1, -2.37) * mm, "end": v(5.2, -2.4) * mm});
            skArc(sketch, "E597.filletArc", {"start": v(5.89, -2.4) * mm, "mid": v(5.99, -2.37) * mm, "end": v(6.06, -2.3) * mm});
            skArc(sketch, "E598.filletArc", {"start": v(6.4, -1.7) * mm, "mid": v(6.44, -1.6) * mm, "end": v(6.4, -1.5) * mm});
            skArc(sketch, "E599.filletArc", {"start": v(6.06, -0.9) * mm, "mid": v(5.99, -0.83) * mm, "end": v(5.89, -0.8) * mm});
            skLineSegment(sketch, "E600", {"start": v(5.2, -0.8) * mm, "end": v(5.89, -0.8) * mm});
            skLineSegment(sketch, "E601", {"start": v(6.06, -0.7) * mm, "end": v(6.4, -0.1) * mm});
            skLineSegment(sketch, "E602", {"start": v(6.4, 0.1) * mm, "end": v(6.06, 0.7) * mm});
            skLineSegment(sketch, "E603", {"start": v(5.89, 0.8) * mm, "end": v(5.2, 0.8) * mm});
            skLineSegment(sketch, "E604", {"start": v(5.02, 0.7) * mm, "end": v(4.68, 0.1) * mm});
            skLineSegment(sketch, "E605", {"start": v(4.68, -0.1) * mm, "end": v(5.02, -0.7) * mm});
            skArc(sketch, "E606.filletArc", {"start": v(5.2, 0.8) * mm, "mid": v(5.1, 0.77) * mm, "end": v(5.02, 0.7) * mm});
            skArc(sketch, "E607.filletArc", {"start": v(4.68, 0.1) * mm, "mid": v(4.65, 0) * mm, "end": v(4.68, -0.1) * mm});
            skArc(sketch, "E608.filletArc", {"start": v(5.02, -0.7) * mm, "mid": v(5.1, -0.77) * mm, "end": v(5.2, -0.8) * mm});
            skArc(sketch, "E609.filletArc", {"start": v(5.89, -0.8) * mm, "mid": v(5.99, -0.77) * mm, "end": v(6.06, -0.7) * mm});
            skArc(sketch, "E610.filletArc", {"start": v(6.4, -0.1) * mm, "mid": v(6.44, 0) * mm, "end": v(6.4, 0.1) * mm});
            skArc(sketch, "E611.filletArc", {"start": v(6.06, 0.7) * mm, "mid": v(5.99, 0.77) * mm, "end": v(5.89, 0.8) * mm});
            skLineSegment(sketch, "E612", {"start": v(2.42, 4) * mm, "end": v(3.12, 4) * mm});
            skLineSegment(sketch, "E613", {"start": v(3.3, 4.1) * mm, "end": v(3.64, 4.7) * mm});
            skLineSegment(sketch, "E614", {"start": v(3.64, 4.9) * mm, "end": v(3.3, 5.5) * mm});
            skLineSegment(sketch, "E615", {"start": v(3.12, 5.6) * mm, "end": v(2.42, 5.6) * mm});
            skLineSegment(sketch, "E616", {"start": v(2.25, 5.5) * mm, "end": v(1.9, 4.9) * mm});
            skLineSegment(sketch, "E617", {"start": v(1.9, 4.7) * mm, "end": v(2.25, 4.1) * mm});
            skArc(sketch, "E618.filletArc", {"start": v(2.42, 5.6) * mm, "mid": v(2.32, 5.57) * mm, "end": v(2.25, 5.5) * mm});
            skArc(sketch, "E619.filletArc", {"start": v(1.9, 4.9) * mm, "mid": v(1.88, 4.8) * mm, "end": v(1.9, 4.7) * mm});
            skArc(sketch, "E620.filletArc", {"start": v(2.25, 4.1) * mm, "mid": v(2.32, 4.03) * mm, "end": v(2.42, 4) * mm});
            skArc(sketch, "E621.filletArc", {"start": v(3.12, 4) * mm, "mid": v(3.22, 4.03) * mm, "end": v(3.3, 4.1) * mm});
            skArc(sketch, "E622.filletArc", {"start": v(3.64, 4.7) * mm, "mid": v(3.66, 4.8) * mm, "end": v(3.64, 4.9) * mm});
            skArc(sketch, "E623.filletArc", {"start": v(3.3, 5.5) * mm, "mid": v(3.22, 5.57) * mm, "end": v(3.12, 5.6) * mm});
            skLineSegment(sketch, "E624", {"start": v(3.81, 3.2) * mm, "end": v(4.5, 3.2) * mm});
            skLineSegment(sketch, "E625", {"start": v(4.68, 3.3) * mm, "end": v(5.02, 3.9) * mm});
            skLineSegment(sketch, "E626", {"start": v(5.02, 4.1) * mm, "end": v(4.68, 4.7) * mm});
            skLineSegment(sketch, "E627", {"start": v(4.5, 4.8) * mm, "end": v(3.81, 4.8) * mm});
            skLineSegment(sketch, "E628", {"start": v(3.64, 4.7) * mm, "end": v(3.3, 4.1) * mm});
            skLineSegment(sketch, "E629", {"start": v(3.3, 3.9) * mm, "end": v(3.64, 3.3) * mm});
            skArc(sketch, "E630.filletArc", {"start": v(3.81, 4.8) * mm, "mid": v(3.71, 4.77) * mm, "end": v(3.64, 4.7) * mm});
            skArc(sketch, "E631.filletArc", {"start": v(3.3, 4.1) * mm, "mid": v(3.26, 4) * mm, "end": v(3.3, 3.9) * mm});
            skArc(sketch, "E632.filletArc", {"start": v(3.64, 3.3) * mm, "mid": v(3.71, 3.23) * mm, "end": v(3.81, 3.2) * mm});
            skArc(sketch, "E633.filletArc", {"start": v(4.5, 3.2) * mm, "mid": v(4.6, 3.23) * mm, "end": v(4.68, 3.3) * mm});
            skArc(sketch, "E634.filletArc", {"start": v(5.02, 3.9) * mm, "mid": v(5.05, 4) * mm, "end": v(5.02, 4.1) * mm});
            skArc(sketch, "E635.filletArc", {"start": v(4.68, 4.7) * mm, "mid": v(4.6, 4.77) * mm, "end": v(4.5, 4.8) * mm});
            skLineSegment(sketch, "E636", {"start": v(1.04, 4.8) * mm, "end": v(1.73, 4.8) * mm});
            skLineSegment(sketch, "E637", {"start": v(1.9, 4.9) * mm, "end": v(2.25, 5.5) * mm});
            skLineSegment(sketch, "E638", {"start": v(2.25, 5.7) * mm, "end": v(1.9, 6.3) * mm});
            skLineSegment(sketch, "E639", {"start": v(1.73, 6.4) * mm, "end": v(1.04, 6.4) * mm});
            skLineSegment(sketch, "E640", {"start": v(0.87, 6.3) * mm, "end": v(0.52, 5.7) * mm});
            skLineSegment(sketch, "E641", {"start": v(0.52, 5.5) * mm, "end": v(0.87, 4.9) * mm});
            skArc(sketch, "E642.filletArc", {"start": v(1.04, 6.4) * mm, "mid": v(0.94, 6.37) * mm, "end": v(0.87, 6.3) * mm});
            skArc(sketch, "E643.filletArc", {"start": v(0.52, 5.7) * mm, "mid": v(0.5, 5.6) * mm, "end": v(0.52, 5.5) * mm});
            skArc(sketch, "E644.filletArc", {"start": v(0.87, 4.9) * mm, "mid": v(0.94, 4.83) * mm, "end": v(1.04, 4.8) * mm});
            skArc(sketch, "E645.filletArc", {"start": v(1.73, 4.8) * mm, "mid": v(1.83, 4.83) * mm, "end": v(1.9, 4.9) * mm});
            skArc(sketch, "E646.filletArc", {"start": v(2.25, 5.5) * mm, "mid": v(2.28, 5.6) * mm, "end": v(2.25, 5.7) * mm});
            skArc(sketch, "E647.filletArc", {"start": v(1.9, 6.3) * mm, "mid": v(1.83, 6.37) * mm, "end": v(1.73, 6.4) * mm});
            skLineSegment(sketch, "E648", {"start": v(-0.35, 5.6) * mm, "end": v(0.35, 5.6) * mm});
            skLineSegment(sketch, "E649", {"start": v(0.52, 5.7) * mm, "end": v(0.87, 6.3) * mm});
            skLineSegment(sketch, "E650", {"start": v(0.87, 6.5) * mm, "end": v(0.52, 7.1) * mm});
            skLineSegment(sketch, "E651", {"start": v(0.35, 7.2) * mm, "end": v(-0.35, 7.2) * mm});
            skLineSegment(sketch, "E652", {"start": v(-0.52, 7.1) * mm, "end": v(-0.87, 6.5) * mm});
            skLineSegment(sketch, "E653", {"start": v(-0.87, 6.3) * mm, "end": v(-0.52, 5.7) * mm});
            skArc(sketch, "E654.filletArc", {"start": v(-0.35, 7.2) * mm, "mid": v(-0.45, 7.17) * mm, "end": v(-0.52, 7.1) * mm});
            skArc(sketch, "E655.filletArc", {"start": v(-0.87, 6.5) * mm, "mid": v(-0.9, 6.4) * mm, "end": v(-0.87, 6.3) * mm});
            skArc(sketch, "E656.filletArc", {"start": v(-0.52, 5.7) * mm, "mid": v(-0.45, 5.63) * mm, "end": v(-0.35, 5.6) * mm});
            skArc(sketch, "E657.filletArc", {"start": v(0.35, 5.6) * mm, "mid": v(0.45, 5.63) * mm, "end": v(0.52, 5.7) * mm});
            skArc(sketch, "E658.filletArc", {"start": v(0.87, 6.3) * mm, "mid": v(0.9, 6.4) * mm, "end": v(0.87, 6.5) * mm});
            skArc(sketch, "E659.filletArc", {"start": v(0.52, 7.1) * mm, "mid": v(0.45, 7.17) * mm, "end": v(0.35, 7.2) * mm});
            skLineSegment(sketch, "E660", {"start": v(-1.73, 4.8) * mm, "end": v(-1.04, 4.8) * mm});
            skLineSegment(sketch, "E661", {"start": v(-0.87, 4.9) * mm, "end": v(-0.52, 5.5) * mm});
            skLineSegment(sketch, "E662", {"start": v(-0.52, 5.7) * mm, "end": v(-0.87, 6.3) * mm});
            skLineSegment(sketch, "E663", {"start": v(-1.04, 6.4) * mm, "end": v(-1.73, 6.4) * mm});
            skLineSegment(sketch, "E664", {"start": v(-1.9, 6.3) * mm, "end": v(-2.25, 5.7) * mm});
            skLineSegment(sketch, "E665", {"start": v(-2.25, 5.5) * mm, "end": v(-1.9, 4.9) * mm});
            skArc(sketch, "E666.filletArc", {"start": v(-1.73, 6.4) * mm, "mid": v(-1.83, 6.37) * mm, "end": v(-1.9, 6.3) * mm});
            skArc(sketch, "E667.filletArc", {"start": v(-2.25, 5.7) * mm, "mid": v(-2.28, 5.6) * mm, "end": v(-2.25, 5.5) * mm});
            skArc(sketch, "E668.filletArc", {"start": v(-1.9, 4.9) * mm, "mid": v(-1.83, 4.83) * mm, "end": v(-1.73, 4.8) * mm});
            skArc(sketch, "E669.filletArc", {"start": v(-1.04, 4.8) * mm, "mid": v(-0.94, 4.83) * mm, "end": v(-0.87, 4.9) * mm});
            skArc(sketch, "E670.filletArc", {"start": v(-0.52, 5.5) * mm, "mid": v(-0.5, 5.6) * mm, "end": v(-0.52, 5.7) * mm});
            skArc(sketch, "E671.filletArc", {"start": v(-0.87, 6.3) * mm, "mid": v(-0.94, 6.37) * mm, "end": v(-1.04, 6.4) * mm});
            skLineSegment(sketch, "E672", {"start": v(-3.12, 4) * mm, "end": v(-2.42, 4) * mm});
            skLineSegment(sketch, "E673", {"start": v(-2.25, 4.1) * mm, "end": v(-1.9, 4.7) * mm});
            skLineSegment(sketch, "E674", {"start": v(-1.9, 4.9) * mm, "end": v(-2.25, 5.5) * mm});
            skLineSegment(sketch, "E675", {"start": v(-2.42, 5.6) * mm, "end": v(-3.12, 5.6) * mm});
            skLineSegment(sketch, "E676", {"start": v(-3.3, 5.5) * mm, "end": v(-3.64, 4.9) * mm});
            skLineSegment(sketch, "E677", {"start": v(-3.64, 4.7) * mm, "end": v(-3.3, 4.1) * mm});
            skArc(sketch, "E678.filletArc", {"start": v(-3.12, 5.6) * mm, "mid": v(-3.22, 5.57) * mm, "end": v(-3.3, 5.5) * mm});
            skArc(sketch, "E679.filletArc", {"start": v(-3.64, 4.9) * mm, "mid": v(-3.66, 4.8) * mm, "end": v(-3.64, 4.7) * mm});
            skArc(sketch, "E680.filletArc", {"start": v(-3.3, 4.1) * mm, "mid": v(-3.22, 4.03) * mm, "end": v(-3.12, 4) * mm});
            skArc(sketch, "E681.filletArc", {"start": v(-2.42, 4) * mm, "mid": v(-2.32, 4.03) * mm, "end": v(-2.25, 4.1) * mm});
            skArc(sketch, "E682.filletArc", {"start": v(-1.9, 4.7) * mm, "mid": v(-1.88, 4.8) * mm, "end": v(-1.9, 4.9) * mm});
            skArc(sketch, "E683.filletArc", {"start": v(-2.25, 5.5) * mm, "mid": v(-2.32, 5.57) * mm, "end": v(-2.42, 5.6) * mm});
            skLineSegment(sketch, "E684", {"start": v(-4.5, 3.2) * mm, "end": v(-3.81, 3.2) * mm});
            skLineSegment(sketch, "E685", {"start": v(-3.64, 3.3) * mm, "end": v(-3.3, 3.9) * mm});
            skLineSegment(sketch, "E686", {"start": v(-3.3, 4.1) * mm, "end": v(-3.64, 4.7) * mm});
            skLineSegment(sketch, "E687", {"start": v(-3.81, 4.8) * mm, "end": v(-4.5, 4.8) * mm});
            skLineSegment(sketch, "E688", {"start": v(-4.68, 4.7) * mm, "end": v(-5.02, 4.1) * mm});
            skLineSegment(sketch, "E689", {"start": v(-5.02, 3.9) * mm, "end": v(-4.68, 3.3) * mm});
            skArc(sketch, "E690.filletArc", {"start": v(-4.5, 4.8) * mm, "mid": v(-4.6, 4.77) * mm, "end": v(-4.68, 4.7) * mm});
            skArc(sketch, "E691.filletArc", {"start": v(-5.02, 4.1) * mm, "mid": v(-5.05, 4) * mm, "end": v(-5.02, 3.9) * mm});
            skArc(sketch, "E692.filletArc", {"start": v(-4.68, 3.3) * mm, "mid": v(-4.6, 3.23) * mm, "end": v(-4.5, 3.2) * mm});
            skArc(sketch, "E693.filletArc", {"start": v(-3.81, 3.2) * mm, "mid": v(-3.71, 3.23) * mm, "end": v(-3.64, 3.3) * mm});
            skArc(sketch, "E694.filletArc", {"start": v(-3.3, 3.9) * mm, "mid": v(-3.26, 4) * mm, "end": v(-3.3, 4.1) * mm});
            skArc(sketch, "E695.filletArc", {"start": v(-3.64, 4.7) * mm, "mid": v(-3.71, 4.77) * mm, "end": v(-3.81, 4.8) * mm});
            skLineSegment(sketch, "E696", {"start": v(-5.89, 2.4) * mm, "end": v(-5.2, 2.4) * mm});
            skLineSegment(sketch, "E697", {"start": v(-5.02, 2.5) * mm, "end": v(-4.68, 3.1) * mm});
            skLineSegment(sketch, "E698", {"start": v(-4.68, 3.3) * mm, "end": v(-5.02, 3.9) * mm});
            skLineSegment(sketch, "E699", {"start": v(-5.2, 4) * mm, "end": v(-5.89, 4) * mm});
            skLineSegment(sketch, "E700", {"start": v(-6.06, 3.9) * mm, "end": v(-6.4, 3.3) * mm});
            skLineSegment(sketch, "E701", {"start": v(-6.4, 3.1) * mm, "end": v(-6.06, 2.5) * mm});
            skArc(sketch, "E702.filletArc", {"start": v(-5.89, 4) * mm, "mid": v(-5.99, 3.97) * mm, "end": v(-6.06, 3.9) * mm});
            skArc(sketch, "E703.filletArc", {"start": v(-6.4, 3.3) * mm, "mid": v(-6.44, 3.2) * mm, "end": v(-6.4, 3.1) * mm});
            skArc(sketch, "E704.filletArc", {"start": v(-6.06, 2.5) * mm, "mid": v(-5.99, 2.43) * mm, "end": v(-5.89, 2.4) * mm});
            skArc(sketch, "E705.filletArc", {"start": v(-5.2, 2.4) * mm, "mid": v(-5.1, 2.43) * mm, "end": v(-5.02, 2.5) * mm});
            skArc(sketch, "E706.filletArc", {"start": v(-4.68, 3.1) * mm, "mid": v(-4.65, 3.2) * mm, "end": v(-4.68, 3.3) * mm});
            skArc(sketch, "E707.filletArc", {"start": v(-5.02, 3.9) * mm, "mid": v(-5.1, 3.97) * mm, "end": v(-5.2, 4) * mm});
            skLineSegment(sketch, "E708", {"start": v(5.2, 0.8) * mm, "end": v(5.89, 0.8) * mm});
            skLineSegment(sketch, "E709", {"start": v(6.06, 0.9) * mm, "end": v(6.4, 1.5) * mm});
            skLineSegment(sketch, "E710", {"start": v(6.4, 1.7) * mm, "end": v(6.06, 2.3) * mm});
            skLineSegment(sketch, "E711", {"start": v(5.89, 2.4) * mm, "end": v(5.2, 2.4) * mm});
            skLineSegment(sketch, "E712", {"start": v(5.02, 2.3) * mm, "end": v(4.68, 1.7) * mm});
            skLineSegment(sketch, "E713", {"start": v(4.68, 1.5) * mm, "end": v(5.02, 0.9) * mm});
            skArc(sketch, "E714.filletArc", {"start": v(5.2, 2.4) * mm, "mid": v(5.1, 2.37) * mm, "end": v(5.02, 2.3) * mm});
            skArc(sketch, "E715.filletArc", {"start": v(4.68, 1.7) * mm, "mid": v(4.65, 1.6) * mm, "end": v(4.68, 1.5) * mm});
            skArc(sketch, "E716.filletArc", {"start": v(5.02, 0.9) * mm, "mid": v(5.1, 0.83) * mm, "end": v(5.2, 0.8) * mm});
            skArc(sketch, "E717.filletArc", {"start": v(5.89, 0.8) * mm, "mid": v(5.99, 0.83) * mm, "end": v(6.06, 0.9) * mm});
            skArc(sketch, "E718.filletArc", {"start": v(6.4, 1.5) * mm, "mid": v(6.44, 1.6) * mm, "end": v(6.4, 1.7) * mm});
            skArc(sketch, "E719.filletArc", {"start": v(6.06, 2.3) * mm, "mid": v(5.99, 2.37) * mm, "end": v(5.89, 2.4) * mm});
            skLineSegment(sketch, "E720", {"start": v(5.2, 2.4) * mm, "end": v(5.89, 2.4) * mm});
            skLineSegment(sketch, "E721", {"start": v(6.06, 2.5) * mm, "end": v(6.4, 3.1) * mm});
            skLineSegment(sketch, "E722", {"start": v(6.4, 3.3) * mm, "end": v(6.06, 3.9) * mm});
            skLineSegment(sketch, "E723", {"start": v(5.89, 4) * mm, "end": v(5.2, 4) * mm});
            skLineSegment(sketch, "E724", {"start": v(5.02, 3.9) * mm, "end": v(4.68, 3.3) * mm});
            skLineSegment(sketch, "E725", {"start": v(4.68, 3.1) * mm, "end": v(5.02, 2.5) * mm});
            skArc(sketch, "E726.filletArc", {"start": v(5.2, 4) * mm, "mid": v(5.1, 3.97) * mm, "end": v(5.02, 3.9) * mm});
            skArc(sketch, "E727.filletArc", {"start": v(4.68, 3.3) * mm, "mid": v(4.65, 3.2) * mm, "end": v(4.68, 3.1) * mm});
            skArc(sketch, "E728.filletArc", {"start": v(5.02, 2.5) * mm, "mid": v(5.1, 2.43) * mm, "end": v(5.2, 2.4) * mm});
            skArc(sketch, "E729.filletArc", {"start": v(5.89, 2.4) * mm, "mid": v(5.99, 2.43) * mm, "end": v(6.06, 2.5) * mm});
            skArc(sketch, "E730.filletArc", {"start": v(6.4, 3.1) * mm, "mid": v(6.44, 3.2) * mm, "end": v(6.4, 3.3) * mm});
            skArc(sketch, "E731.filletArc", {"start": v(6.06, 3.9) * mm, "mid": v(5.99, 3.97) * mm, "end": v(5.89, 4) * mm});
            skLineSegment(sketch, "E732", {"start": v(-7.27, -3.2) * mm, "end": v(-6.58, -3.2) * mm});
            skLineSegment(sketch, "E733", {"start": v(-6.4, -3.1) * mm, "end": v(-6.06, -2.5) * mm});
            skLineSegment(sketch, "E734", {"start": v(-6.06, -2.3) * mm, "end": v(-6.4, -1.7) * mm});
            skLineSegment(sketch, "E735", {"start": v(-6.58, -1.6) * mm, "end": v(-7.27, -1.6) * mm});
            skLineSegment(sketch, "E736", {"start": v(-7.45, -1.7) * mm, "end": v(-7.8, -2.3) * mm});
            skLineSegment(sketch, "E737", {"start": v(-7.8, -2.5) * mm, "end": v(-7.45, -3.1) * mm});
            skArc(sketch, "E738.filletArc", {"start": v(-7.27, -1.6) * mm, "mid": v(-7.37, -1.63) * mm, "end": v(-7.45, -1.7) * mm});
            skArc(sketch, "E739.filletArc", {"start": v(-7.8, -2.3) * mm, "mid": v(-7.82, -2.4) * mm, "end": v(-7.8, -2.5) * mm});
            skArc(sketch, "E740.filletArc", {"start": v(-7.45, -3.1) * mm, "mid": v(-7.37, -3.17) * mm, "end": v(-7.27, -3.2) * mm});
            skArc(sketch, "E741.filletArc", {"start": v(-6.58, -3.2) * mm, "mid": v(-6.48, -3.17) * mm, "end": v(-6.4, -3.1) * mm});
            skArc(sketch, "E742.filletArc", {"start": v(-6.06, -2.5) * mm, "mid": v(-6.04, -2.4) * mm, "end": v(-6.06, -2.3) * mm});
            skArc(sketch, "E743.filletArc", {"start": v(-6.4, -1.7) * mm, "mid": v(-6.48, -1.63) * mm, "end": v(-6.58, -1.6) * mm});
            skLineSegment(sketch, "E744", {"start": v(-7.27, -1.6) * mm, "end": v(-6.58, -1.6) * mm});
            skLineSegment(sketch, "E745", {"start": v(-6.4, -1.5) * mm, "end": v(-6.06, -0.9) * mm});
            skLineSegment(sketch, "E746", {"start": v(-6.06, -0.7) * mm, "end": v(-6.4, -0.1) * mm});
            skLineSegment(sketch, "E747", {"start": v(-6.58, 0) * mm, "end": v(-7.27, 0) * mm});
            skLineSegment(sketch, "E748", {"start": v(-7.45, -0.1) * mm, "end": v(-7.8, -0.7) * mm});
            skLineSegment(sketch, "E749", {"start": v(-7.8, -0.9) * mm, "end": v(-7.45, -1.5) * mm});
            skArc(sketch, "E750.filletArc", {"start": v(-7.27, 0) * mm, "mid": v(-7.37, -0.03) * mm, "end": v(-7.45, -0.1) * mm});
            skArc(sketch, "E751.filletArc", {"start": v(-7.8, -0.7) * mm, "mid": v(-7.82, -0.8) * mm, "end": v(-7.8, -0.9) * mm});
            skArc(sketch, "E752.filletArc", {"start": v(-7.45, -1.5) * mm, "mid": v(-7.37, -1.57) * mm, "end": v(-7.27, -1.6) * mm});
            skArc(sketch, "E753.filletArc", {"start": v(-6.58, -1.6) * mm, "mid": v(-6.48, -1.57) * mm, "end": v(-6.4, -1.5) * mm});
            skArc(sketch, "E754.filletArc", {"start": v(-6.06, -0.9) * mm, "mid": v(-6.04, -0.8) * mm, "end": v(-6.06, -0.7) * mm});
            skArc(sketch, "E755.filletArc", {"start": v(-6.4, -0.1) * mm, "mid": v(-6.48, -0.03) * mm, "end": v(-6.58, 0) * mm});
            skLineSegment(sketch, "E756", {"start": v(-7.27, 0) * mm, "end": v(-6.58, 0) * mm});
            skLineSegment(sketch, "E757", {"start": v(-6.4, 0.1) * mm, "end": v(-6.06, 0.7) * mm});
            skLineSegment(sketch, "E758", {"start": v(-6.06, 0.9) * mm, "end": v(-6.4, 1.5) * mm});
            skLineSegment(sketch, "E759", {"start": v(-6.58, 1.6) * mm, "end": v(-7.27, 1.6) * mm});
            skLineSegment(sketch, "E760", {"start": v(-7.45, 1.5) * mm, "end": v(-7.8, 0.9) * mm});
            skLineSegment(sketch, "E761", {"start": v(-7.8, 0.7) * mm, "end": v(-7.45, 0.1) * mm});
            skArc(sketch, "E762.filletArc", {"start": v(-7.27, 1.6) * mm, "mid": v(-7.37, 1.57) * mm, "end": v(-7.45, 1.5) * mm});
            skArc(sketch, "E763.filletArc", {"start": v(-7.8, 0.9) * mm, "mid": v(-7.82, 0.8) * mm, "end": v(-7.8, 0.7) * mm});
            skArc(sketch, "E764.filletArc", {"start": v(-7.45, 0.1) * mm, "mid": v(-7.37, 0.03) * mm, "end": v(-7.27, 0) * mm});
            skArc(sketch, "E765.filletArc", {"start": v(-6.58, 0) * mm, "mid": v(-6.48, 0.03) * mm, "end": v(-6.4, 0.1) * mm});
            skArc(sketch, "E766.filletArc", {"start": v(-6.06, 0.7) * mm, "mid": v(-6.04, 0.8) * mm, "end": v(-6.06, 0.9) * mm});
            skArc(sketch, "E767.filletArc", {"start": v(-6.4, 1.5) * mm, "mid": v(-6.48, 1.57) * mm, "end": v(-6.58, 1.6) * mm});
            skLineSegment(sketch, "E768", {"start": v(-7.27, 1.6) * mm, "end": v(-6.58, 1.6) * mm});
            skLineSegment(sketch, "E769", {"start": v(-6.4, 1.7) * mm, "end": v(-6.06, 2.3) * mm});
            skLineSegment(sketch, "E770", {"start": v(-6.06, 2.5) * mm, "end": v(-6.4, 3.1) * mm});
            skLineSegment(sketch, "E771", {"start": v(-6.58, 3.2) * mm, "end": v(-7.27, 3.2) * mm});
            skLineSegment(sketch, "E772", {"start": v(-7.45, 3.1) * mm, "end": v(-7.8, 2.5) * mm});
            skLineSegment(sketch, "E773", {"start": v(-7.8, 2.3) * mm, "end": v(-7.45, 1.7) * mm});
            skArc(sketch, "E774.filletArc", {"start": v(-7.27, 3.2) * mm, "mid": v(-7.37, 3.17) * mm, "end": v(-7.45, 3.1) * mm});
            skArc(sketch, "E775.filletArc", {"start": v(-7.8, 2.5) * mm, "mid": v(-7.82, 2.4) * mm, "end": v(-7.8, 2.3) * mm});
            skArc(sketch, "E776.filletArc", {"start": v(-7.45, 1.7) * mm, "mid": v(-7.37, 1.63) * mm, "end": v(-7.27, 1.6) * mm});
            skArc(sketch, "E777.filletArc", {"start": v(-6.58, 1.6) * mm, "mid": v(-6.48, 1.63) * mm, "end": v(-6.4, 1.7) * mm});
            skArc(sketch, "E778.filletArc", {"start": v(-6.06, 2.3) * mm, "mid": v(-6.04, 2.4) * mm, "end": v(-6.06, 2.5) * mm});
            skArc(sketch, "E779.filletArc", {"start": v(-6.4, 3.1) * mm, "mid": v(-6.48, 3.17) * mm, "end": v(-6.58, 3.2) * mm});
            skLineSegment(sketch, "E780", {"start": v(6.58, 0) * mm, "end": v(7.27, 0) * mm});
            skLineSegment(sketch, "E781", {"start": v(7.45, 0.1) * mm, "end": v(7.8, 0.7) * mm});
            skLineSegment(sketch, "E782", {"start": v(7.8, 0.9) * mm, "end": v(7.45, 1.5) * mm});
            skLineSegment(sketch, "E783", {"start": v(7.27, 1.6) * mm, "end": v(6.58, 1.6) * mm});
            skLineSegment(sketch, "E784", {"start": v(6.4, 1.5) * mm, "end": v(6.06, 0.9) * mm});
            skLineSegment(sketch, "E785", {"start": v(6.06, 0.7) * mm, "end": v(6.4, 0.1) * mm});
            skArc(sketch, "E786.filletArc", {"start": v(6.58, 1.6) * mm, "mid": v(6.48, 1.57) * mm, "end": v(6.4, 1.5) * mm});
            skArc(sketch, "E787.filletArc", {"start": v(6.06, 0.9) * mm, "mid": v(6.04, 0.8) * mm, "end": v(6.06, 0.7) * mm});
            skArc(sketch, "E788.filletArc", {"start": v(6.4, 0.1) * mm, "mid": v(6.48, 0.03) * mm, "end": v(6.58, 0) * mm});
            skArc(sketch, "E789.filletArc", {"start": v(7.27, 0) * mm, "mid": v(7.37, 0.03) * mm, "end": v(7.45, 0.1) * mm});
            skArc(sketch, "E790.filletArc", {"start": v(7.8, 0.7) * mm, "mid": v(7.82, 0.8) * mm, "end": v(7.8, 0.9) * mm});
            skArc(sketch, "E791.filletArc", {"start": v(7.45, 1.5) * mm, "mid": v(7.37, 1.57) * mm, "end": v(7.27, 1.6) * mm});
            skLineSegment(sketch, "E792", {"start": v(6.58, 1.6) * mm, "end": v(7.27, 1.6) * mm});
            skLineSegment(sketch, "E793", {"start": v(7.45, 1.7) * mm, "end": v(7.8, 2.3) * mm});
            skLineSegment(sketch, "E794", {"start": v(7.8, 2.5) * mm, "end": v(7.45, 3.1) * mm});
            skLineSegment(sketch, "E795", {"start": v(7.27, 3.2) * mm, "end": v(6.58, 3.2) * mm});
            skLineSegment(sketch, "E796", {"start": v(6.4, 3.1) * mm, "end": v(6.06, 2.5) * mm});
            skLineSegment(sketch, "E797", {"start": v(6.06, 2.3) * mm, "end": v(6.4, 1.7) * mm});
            skArc(sketch, "E798.filletArc", {"start": v(6.58, 3.2) * mm, "mid": v(6.48, 3.17) * mm, "end": v(6.4, 3.1) * mm});
            skArc(sketch, "E799.filletArc", {"start": v(6.06, 2.5) * mm, "mid": v(6.04, 2.4) * mm, "end": v(6.06, 2.3) * mm});
            skArc(sketch, "E800.filletArc", {"start": v(6.4, 1.7) * mm, "mid": v(6.48, 1.63) * mm, "end": v(6.58, 1.6) * mm});
            skArc(sketch, "E801.filletArc", {"start": v(7.27, 1.6) * mm, "mid": v(7.37, 1.63) * mm, "end": v(7.45, 1.7) * mm});
            skArc(sketch, "E802.filletArc", {"start": v(7.8, 2.3) * mm, "mid": v(7.82, 2.4) * mm, "end": v(7.8, 2.5) * mm});
            skArc(sketch, "E803.filletArc", {"start": v(7.45, 3.1) * mm, "mid": v(7.37, 3.17) * mm, "end": v(7.27, 3.2) * mm});
            skLineSegment(sketch, "E804", {"start": v(6.58, -1.6) * mm, "end": v(7.27, -1.6) * mm});
            skLineSegment(sketch, "E805", {"start": v(7.45, -1.5) * mm, "end": v(7.8, -0.9) * mm});
            skLineSegment(sketch, "E806", {"start": v(7.8, -0.7) * mm, "end": v(7.45, -0.1) * mm});
            skLineSegment(sketch, "E807", {"start": v(7.27, 0) * mm, "end": v(6.58, 0) * mm});
            skLineSegment(sketch, "E808", {"start": v(6.4, -0.1) * mm, "end": v(6.06, -0.7) * mm});
            skLineSegment(sketch, "E809", {"start": v(6.06, -0.9) * mm, "end": v(6.4, -1.5) * mm});
            skArc(sketch, "E810.filletArc", {"start": v(6.58, 0) * mm, "mid": v(6.48, -0.03) * mm, "end": v(6.4, -0.1) * mm});
            skArc(sketch, "E811.filletArc", {"start": v(6.06, -0.7) * mm, "mid": v(6.04, -0.8) * mm, "end": v(6.06, -0.9) * mm});
            skArc(sketch, "E812.filletArc", {"start": v(6.4, -1.5) * mm, "mid": v(6.48, -1.57) * mm, "end": v(6.58, -1.6) * mm});
            skArc(sketch, "E813.filletArc", {"start": v(7.27, -1.6) * mm, "mid": v(7.37, -1.57) * mm, "end": v(7.45, -1.5) * mm});
            skArc(sketch, "E814.filletArc", {"start": v(7.8, -0.9) * mm, "mid": v(7.82, -0.8) * mm, "end": v(7.8, -0.7) * mm});
            skArc(sketch, "E815.filletArc", {"start": v(7.45, -0.1) * mm, "mid": v(7.37, -0.03) * mm, "end": v(7.27, 0) * mm});
            skLineSegment(sketch, "E816", {"start": v(6.58, -3.2) * mm, "end": v(7.27, -3.2) * mm});
            skLineSegment(sketch, "E817", {"start": v(7.45, -3.1) * mm, "end": v(7.8, -2.5) * mm});
            skLineSegment(sketch, "E818", {"start": v(7.8, -2.3) * mm, "end": v(7.45, -1.7) * mm});
            skLineSegment(sketch, "E819", {"start": v(7.27, -1.6) * mm, "end": v(6.58, -1.6) * mm});
            skLineSegment(sketch, "E820", {"start": v(6.4, -1.7) * mm, "end": v(6.06, -2.3) * mm});
            skLineSegment(sketch, "E821", {"start": v(6.06, -2.5) * mm, "end": v(6.4, -3.1) * mm});
            skArc(sketch, "E822.filletArc", {"start": v(6.58, -1.6) * mm, "mid": v(6.48, -1.63) * mm, "end": v(6.4, -1.7) * mm});
            skArc(sketch, "E823.filletArc", {"start": v(6.06, -2.3) * mm, "mid": v(6.04, -2.4) * mm, "end": v(6.06, -2.5) * mm});
            skArc(sketch, "E824.filletArc", {"start": v(6.4, -3.1) * mm, "mid": v(6.48, -3.17) * mm, "end": v(6.58, -3.2) * mm});
            skArc(sketch, "E825.filletArc", {"start": v(7.27, -3.2) * mm, "mid": v(7.37, -3.17) * mm, "end": v(7.45, -3.1) * mm});
            skArc(sketch, "E826.filletArc", {"start": v(7.8, -2.5) * mm, "mid": v(7.82, -2.4) * mm, "end": v(7.8, -2.3) * mm});
            skArc(sketch, "E827.filletArc", {"start": v(7.45, -1.7) * mm, "mid": v(7.37, -1.63) * mm, "end": v(7.27, -1.6) * mm});
            skLineSegment(sketch, "E828", {"start": v(6.58, 3.2) * mm, "end": v(7.27, 3.2) * mm});
            skLineSegment(sketch, "E829", {"start": v(7.45, 3.3) * mm, "end": v(7.8, 3.9) * mm});
            skLineSegment(sketch, "E830", {"start": v(7.8, 4.1) * mm, "end": v(7.45, 4.7) * mm});
            skLineSegment(sketch, "E831", {"start": v(7.27, 4.8) * mm, "end": v(6.58, 4.8) * mm});
            skLineSegment(sketch, "E832", {"start": v(6.4, 4.7) * mm, "end": v(6.06, 4.1) * mm});
            skLineSegment(sketch, "E833", {"start": v(6.06, 3.9) * mm, "end": v(6.4, 3.3) * mm});
            skArc(sketch, "E834.filletArc", {"start": v(6.58, 4.8) * mm, "mid": v(6.48, 4.77) * mm, "end": v(6.4, 4.7) * mm});
            skArc(sketch, "E835.filletArc", {"start": v(6.06, 4.1) * mm, "mid": v(6.04, 4) * mm, "end": v(6.06, 3.9) * mm});
            skArc(sketch, "E836.filletArc", {"start": v(6.4, 3.3) * mm, "mid": v(6.48, 3.23) * mm, "end": v(6.58, 3.2) * mm});
            skArc(sketch, "E837.filletArc", {"start": v(7.27, 3.2) * mm, "mid": v(7.37, 3.23) * mm, "end": v(7.45, 3.3) * mm});
            skArc(sketch, "E838.filletArc", {"start": v(7.8, 3.9) * mm, "mid": v(7.82, 4) * mm, "end": v(7.8, 4.1) * mm});
            skArc(sketch, "E839.filletArc", {"start": v(7.45, 4.7) * mm, "mid": v(7.37, 4.77) * mm, "end": v(7.27, 4.8) * mm});
            skLineSegment(sketch, "E840", {"start": v(5.2, 4) * mm, "end": v(5.89, 4) * mm});
            skLineSegment(sketch, "E841", {"start": v(6.06, 4.1) * mm, "end": v(6.4, 4.7) * mm});
            skLineSegment(sketch, "E842", {"start": v(6.4, 4.9) * mm, "end": v(6.06, 5.5) * mm});
            skLineSegment(sketch, "E843", {"start": v(5.89, 5.6) * mm, "end": v(5.2, 5.6) * mm});
            skLineSegment(sketch, "E844", {"start": v(5.02, 5.5) * mm, "end": v(4.68, 4.9) * mm});
            skLineSegment(sketch, "E845", {"start": v(4.68, 4.7) * mm, "end": v(5.02, 4.1) * mm});
            skArc(sketch, "E846.filletArc", {"start": v(5.2, 5.6) * mm, "mid": v(5.1, 5.57) * mm, "end": v(5.02, 5.5) * mm});
            skArc(sketch, "E847.filletArc", {"start": v(4.68, 4.9) * mm, "mid": v(4.65, 4.8) * mm, "end": v(4.68, 4.7) * mm});
            skArc(sketch, "E848.filletArc", {"start": v(5.02, 4.1) * mm, "mid": v(5.1, 4.03) * mm, "end": v(5.2, 4) * mm});
            skArc(sketch, "E849.filletArc", {"start": v(5.89, 4) * mm, "mid": v(5.99, 4.03) * mm, "end": v(6.06, 4.1) * mm});
            skArc(sketch, "E850.filletArc", {"start": v(6.4, 4.7) * mm, "mid": v(6.44, 4.8) * mm, "end": v(6.4, 4.9) * mm});
            skArc(sketch, "E851.filletArc", {"start": v(6.06, 5.5) * mm, "mid": v(5.99, 5.57) * mm, "end": v(5.89, 5.6) * mm});
            skLineSegment(sketch, "E852", {"start": v(3.81, 4.8) * mm, "end": v(4.5, 4.8) * mm});
            skLineSegment(sketch, "E853", {"start": v(4.68, 4.9) * mm, "end": v(5.02, 5.5) * mm});
            skLineSegment(sketch, "E854", {"start": v(5.02, 5.7) * mm, "end": v(4.68, 6.3) * mm});
            skLineSegment(sketch, "E855", {"start": v(4.5, 6.4) * mm, "end": v(3.81, 6.4) * mm});
            skLineSegment(sketch, "E856", {"start": v(3.64, 6.3) * mm, "end": v(3.3, 5.7) * mm});
            skLineSegment(sketch, "E857", {"start": v(3.3, 5.5) * mm, "end": v(3.64, 4.9) * mm});
            skArc(sketch, "E858.filletArc", {"start": v(3.81, 6.4) * mm, "mid": v(3.71, 6.37) * mm, "end": v(3.64, 6.3) * mm});
            skArc(sketch, "E859.filletArc", {"start": v(3.3, 5.7) * mm, "mid": v(3.26, 5.6) * mm, "end": v(3.3, 5.5) * mm});
            skArc(sketch, "E860.filletArc", {"start": v(3.64, 4.9) * mm, "mid": v(3.71, 4.83) * mm, "end": v(3.81, 4.8) * mm});
            skArc(sketch, "E861.filletArc", {"start": v(4.5, 4.8) * mm, "mid": v(4.6, 4.83) * mm, "end": v(4.68, 4.9) * mm});
            skArc(sketch, "E862.filletArc", {"start": v(5.02, 5.5) * mm, "mid": v(5.05, 5.6) * mm, "end": v(5.02, 5.7) * mm});
            skArc(sketch, "E863.filletArc", {"start": v(4.68, 6.3) * mm, "mid": v(4.6, 6.37) * mm, "end": v(4.5, 6.4) * mm});
            skLineSegment(sketch, "E864", {"start": v(2.42, 5.6) * mm, "end": v(3.12, 5.6) * mm});
            skLineSegment(sketch, "E865", {"start": v(3.3, 5.7) * mm, "end": v(3.64, 6.3) * mm});
            skLineSegment(sketch, "E866", {"start": v(3.64, 6.5) * mm, "end": v(3.3, 7.1) * mm});
            skLineSegment(sketch, "E867", {"start": v(3.12, 7.2) * mm, "end": v(2.42, 7.2) * mm});
            skLineSegment(sketch, "E868", {"start": v(2.25, 7.1) * mm, "end": v(1.9, 6.5) * mm});
            skLineSegment(sketch, "E869", {"start": v(1.9, 6.3) * mm, "end": v(2.25, 5.7) * mm});
            skArc(sketch, "E870.filletArc", {"start": v(2.42, 7.2) * mm, "mid": v(2.32, 7.17) * mm, "end": v(2.25, 7.1) * mm});
            skArc(sketch, "E871.filletArc", {"start": v(1.9, 6.5) * mm, "mid": v(1.88, 6.4) * mm, "end": v(1.9, 6.3) * mm});
            skArc(sketch, "E872.filletArc", {"start": v(2.25, 5.7) * mm, "mid": v(2.32, 5.63) * mm, "end": v(2.42, 5.6) * mm});
            skArc(sketch, "E873.filletArc", {"start": v(3.12, 5.6) * mm, "mid": v(3.22, 5.63) * mm, "end": v(3.3, 5.7) * mm});
            skArc(sketch, "E874.filletArc", {"start": v(3.64, 6.3) * mm, "mid": v(3.66, 6.4) * mm, "end": v(3.64, 6.5) * mm});
            skArc(sketch, "E875.filletArc", {"start": v(3.3, 7.1) * mm, "mid": v(3.22, 7.17) * mm, "end": v(3.12, 7.2) * mm});
            skLineSegment(sketch, "E876", {"start": v(1.04, 6.4) * mm, "end": v(1.73, 6.4) * mm});
            skLineSegment(sketch, "E877", {"start": v(1.9, 6.5) * mm, "end": v(2.25, 7.1) * mm});
            skLineSegment(sketch, "E878", {"start": v(2.25, 7.3) * mm, "end": v(1.9, 7.9) * mm});
            skLineSegment(sketch, "E879", {"start": v(1.73, 8) * mm, "end": v(1.04, 8) * mm});
            skLineSegment(sketch, "E880", {"start": v(0.87, 7.9) * mm, "end": v(0.52, 7.3) * mm});
            skLineSegment(sketch, "E881", {"start": v(0.52, 7.1) * mm, "end": v(0.87, 6.5) * mm});
            skArc(sketch, "E882.filletArc", {"start": v(1.04, 8) * mm, "mid": v(0.94, 7.97) * mm, "end": v(0.87, 7.9) * mm});
            skArc(sketch, "E883.filletArc", {"start": v(0.52, 7.3) * mm, "mid": v(0.5, 7.2) * mm, "end": v(0.52, 7.1) * mm});
            skArc(sketch, "E884.filletArc", {"start": v(0.87, 6.5) * mm, "mid": v(0.94, 6.43) * mm, "end": v(1.04, 6.4) * mm});
            skArc(sketch, "E885.filletArc", {"start": v(1.73, 6.4) * mm, "mid": v(1.83, 6.43) * mm, "end": v(1.9, 6.5) * mm});
            skArc(sketch, "E886.filletArc", {"start": v(2.25, 7.1) * mm, "mid": v(2.28, 7.2) * mm, "end": v(2.25, 7.3) * mm});
            skArc(sketch, "E887.filletArc", {"start": v(1.9, 7.9) * mm, "mid": v(1.83, 7.97) * mm, "end": v(1.73, 8) * mm});
            skLineSegment(sketch, "E888", {"start": v(-1.73, 6.4) * mm, "end": v(-1.04, 6.4) * mm});
            skLineSegment(sketch, "E889", {"start": v(-0.87, 6.5) * mm, "end": v(-0.52, 7.1) * mm});
            skLineSegment(sketch, "E890", {"start": v(-0.52, 7.3) * mm, "end": v(-0.87, 7.9) * mm});
            skLineSegment(sketch, "E891", {"start": v(-1.04, 8) * mm, "end": v(-1.73, 8) * mm});
            skLineSegment(sketch, "E892", {"start": v(-1.9, 7.9) * mm, "end": v(-2.25, 7.3) * mm});
            skLineSegment(sketch, "E893", {"start": v(-2.25, 7.1) * mm, "end": v(-1.9, 6.5) * mm});
            skArc(sketch, "E894.filletArc", {"start": v(-1.73, 8) * mm, "mid": v(-1.83, 7.97) * mm, "end": v(-1.9, 7.9) * mm});
            skArc(sketch, "E895.filletArc", {"start": v(-2.25, 7.3) * mm, "mid": v(-2.28, 7.2) * mm, "end": v(-2.25, 7.1) * mm});
            skArc(sketch, "E896.filletArc", {"start": v(-1.9, 6.5) * mm, "mid": v(-1.83, 6.43) * mm, "end": v(-1.73, 6.4) * mm});
            skArc(sketch, "E897.filletArc", {"start": v(-1.04, 6.4) * mm, "mid": v(-0.94, 6.43) * mm, "end": v(-0.87, 6.5) * mm});
            skArc(sketch, "E898.filletArc", {"start": v(-0.52, 7.1) * mm, "mid": v(-0.5, 7.2) * mm, "end": v(-0.52, 7.3) * mm});
            skArc(sketch, "E899.filletArc", {"start": v(-0.87, 7.9) * mm, "mid": v(-0.94, 7.97) * mm, "end": v(-1.04, 8) * mm});
            skLineSegment(sketch, "E900", {"start": v(-0.35, 7.2) * mm, "end": v(0.35, 7.2) * mm});
            skLineSegment(sketch, "E901", {"start": v(0.52, 7.3) * mm, "end": v(0.87, 7.9) * mm});
            skLineSegment(sketch, "E902", {"start": v(0.87, 8.1) * mm, "end": v(0.52, 8.7) * mm});
            skLineSegment(sketch, "E903", {"start": v(0.35, 8.8) * mm, "end": v(-0.35, 8.8) * mm});
            skLineSegment(sketch, "E904", {"start": v(-0.52, 8.7) * mm, "end": v(-0.87, 8.1) * mm});
            skLineSegment(sketch, "E905", {"start": v(-0.87, 7.9) * mm, "end": v(-0.52, 7.3) * mm});
            skArc(sketch, "E906.filletArc", {"start": v(-0.35, 8.8) * mm, "mid": v(-0.45, 8.77) * mm, "end": v(-0.52, 8.7) * mm});
            skArc(sketch, "E907.filletArc", {"start": v(-0.87, 8.1) * mm, "mid": v(-0.9, 8) * mm, "end": v(-0.87, 7.9) * mm});
            skArc(sketch, "E908.filletArc", {"start": v(-0.52, 7.3) * mm, "mid": v(-0.45, 7.23) * mm, "end": v(-0.35, 7.2) * mm});
            skArc(sketch, "E909.filletArc", {"start": v(0.35, 7.2) * mm, "mid": v(0.45, 7.23) * mm, "end": v(0.52, 7.3) * mm});
            skArc(sketch, "E910.filletArc", {"start": v(0.87, 7.9) * mm, "mid": v(0.9, 8) * mm, "end": v(0.87, 8.1) * mm});
            skArc(sketch, "E911.filletArc", {"start": v(0.52, 8.7) * mm, "mid": v(0.45, 8.77) * mm, "end": v(0.35, 8.8) * mm});
            skLineSegment(sketch, "E912", {"start": v(-4.5, 4.8) * mm, "end": v(-3.81, 4.8) * mm});
            skLineSegment(sketch, "E913", {"start": v(-3.64, 4.9) * mm, "end": v(-3.3, 5.5) * mm});
            skLineSegment(sketch, "E914", {"start": v(-3.3, 5.7) * mm, "end": v(-3.64, 6.3) * mm});
            skLineSegment(sketch, "E915", {"start": v(-3.81, 6.4) * mm, "end": v(-4.5, 6.4) * mm});
            skLineSegment(sketch, "E916", {"start": v(-4.68, 6.3) * mm, "end": v(-5.02, 5.7) * mm});
            skLineSegment(sketch, "E917", {"start": v(-5.02, 5.5) * mm, "end": v(-4.68, 4.9) * mm});
            skArc(sketch, "E918.filletArc", {"start": v(-4.5, 6.4) * mm, "mid": v(-4.6, 6.37) * mm, "end": v(-4.68, 6.3) * mm});
            skArc(sketch, "E919.filletArc", {"start": v(-5.02, 5.7) * mm, "mid": v(-5.05, 5.6) * mm, "end": v(-5.02, 5.5) * mm});
            skArc(sketch, "E920.filletArc", {"start": v(-4.68, 4.9) * mm, "mid": v(-4.6, 4.83) * mm, "end": v(-4.5, 4.8) * mm});
            skArc(sketch, "E921.filletArc", {"start": v(-3.81, 4.8) * mm, "mid": v(-3.71, 4.83) * mm, "end": v(-3.64, 4.9) * mm});
            skArc(sketch, "E922.filletArc", {"start": v(-3.3, 5.5) * mm, "mid": v(-3.26, 5.6) * mm, "end": v(-3.3, 5.7) * mm});
            skArc(sketch, "E923.filletArc", {"start": v(-3.64, 6.3) * mm, "mid": v(-3.71, 6.37) * mm, "end": v(-3.81, 6.4) * mm});
            skLineSegment(sketch, "E924", {"start": v(-5.89, -5.6) * mm, "end": v(-5.2, -5.6) * mm});
            skLineSegment(sketch, "E925", {"start": v(-5.02, -5.5) * mm, "end": v(-4.68, -4.9) * mm});
            skLineSegment(sketch, "E926", {"start": v(-4.68, -4.7) * mm, "end": v(-5.02, -4.1) * mm});
            skLineSegment(sketch, "E927", {"start": v(-5.2, -4) * mm, "end": v(-5.89, -4) * mm});
            skLineSegment(sketch, "E928", {"start": v(-6.06, -4.1) * mm, "end": v(-6.4, -4.7) * mm});
            skLineSegment(sketch, "E929", {"start": v(-6.4, -4.9) * mm, "end": v(-6.06, -5.5) * mm});
            skArc(sketch, "E930.filletArc", {"start": v(-5.89, -4) * mm, "mid": v(-5.99, -4.03) * mm, "end": v(-6.06, -4.1) * mm});
            skArc(sketch, "E931.filletArc", {"start": v(-6.4, -4.7) * mm, "mid": v(-6.44, -4.8) * mm, "end": v(-6.4, -4.9) * mm});
            skArc(sketch, "E932.filletArc", {"start": v(-6.06, -5.5) * mm, "mid": v(-5.99, -5.57) * mm, "end": v(-5.89, -5.6) * mm});
            skArc(sketch, "E933.filletArc", {"start": v(-5.2, -5.6) * mm, "mid": v(-5.1, -5.57) * mm, "end": v(-5.02, -5.5) * mm});
            skArc(sketch, "E934.filletArc", {"start": v(-4.68, -4.9) * mm, "mid": v(-4.65, -4.8) * mm, "end": v(-4.68, -4.7) * mm});
            skArc(sketch, "E935.filletArc", {"start": v(-5.02, -4.1) * mm, "mid": v(-5.1, -4.03) * mm, "end": v(-5.2, -4) * mm});
            skLineSegment(sketch, "E936", {"start": v(-7.27, 3.2) * mm, "end": v(-6.58, 3.2) * mm});
            skLineSegment(sketch, "E937", {"start": v(-6.4, 3.3) * mm, "end": v(-6.06, 3.9) * mm});
            skLineSegment(sketch, "E938", {"start": v(-6.06, 4.1) * mm, "end": v(-6.4, 4.7) * mm});
            skLineSegment(sketch, "E939", {"start": v(-6.58, 4.8) * mm, "end": v(-7.27, 4.8) * mm});
            skLineSegment(sketch, "E940", {"start": v(-7.45, 4.7) * mm, "end": v(-7.8, 4.1) * mm});
            skLineSegment(sketch, "E941", {"start": v(-7.8, 3.9) * mm, "end": v(-7.45, 3.3) * mm});
            skArc(sketch, "E942.filletArc", {"start": v(-7.27, 4.8) * mm, "mid": v(-7.37, 4.77) * mm, "end": v(-7.45, 4.7) * mm});
            skArc(sketch, "E943.filletArc", {"start": v(-7.8, 4.1) * mm, "mid": v(-7.82, 4) * mm, "end": v(-7.8, 3.9) * mm});
            skArc(sketch, "E944.filletArc", {"start": v(-7.45, 3.3) * mm, "mid": v(-7.37, 3.23) * mm, "end": v(-7.27, 3.2) * mm});
            skArc(sketch, "E945.filletArc", {"start": v(-6.58, 3.2) * mm, "mid": v(-6.48, 3.23) * mm, "end": v(-6.4, 3.3) * mm});
            skArc(sketch, "E946.filletArc", {"start": v(-6.06, 3.9) * mm, "mid": v(-6.04, 4) * mm, "end": v(-6.06, 4.1) * mm});
            skArc(sketch, "E947.filletArc", {"start": v(-6.4, 4.7) * mm, "mid": v(-6.48, 4.77) * mm, "end": v(-6.58, 4.8) * mm});
            skLineSegment(sketch, "E948", {"start": v(-5.89, 4) * mm, "end": v(-5.2, 4) * mm});
            skLineSegment(sketch, "E949", {"start": v(-5.02, 4.1) * mm, "end": v(-4.68, 4.7) * mm});
            skLineSegment(sketch, "E950", {"start": v(-4.68, 4.9) * mm, "end": v(-5.02, 5.5) * mm});
            skLineSegment(sketch, "E951", {"start": v(-5.2, 5.6) * mm, "end": v(-5.89, 5.6) * mm});
            skLineSegment(sketch, "E952", {"start": v(-6.06, 5.5) * mm, "end": v(-6.4, 4.9) * mm});
            skLineSegment(sketch, "E953", {"start": v(-6.4, 4.7) * mm, "end": v(-6.06, 4.1) * mm});
            skArc(sketch, "E954.filletArc", {"start": v(-5.89, 5.6) * mm, "mid": v(-5.99, 5.57) * mm, "end": v(-6.06, 5.5) * mm});
            skArc(sketch, "E955.filletArc", {"start": v(-6.4, 4.9) * mm, "mid": v(-6.44, 4.8) * mm, "end": v(-6.4, 4.7) * mm});
            skArc(sketch, "E956.filletArc", {"start": v(-6.06, 4.1) * mm, "mid": v(-5.99, 4.03) * mm, "end": v(-5.89, 4) * mm});
            skArc(sketch, "E957.filletArc", {"start": v(-5.2, 4) * mm, "mid": v(-5.1, 4.03) * mm, "end": v(-5.02, 4.1) * mm});
            skArc(sketch, "E958.filletArc", {"start": v(-4.68, 4.7) * mm, "mid": v(-4.65, 4.8) * mm, "end": v(-4.68, 4.9) * mm});
            skArc(sketch, "E959.filletArc", {"start": v(-5.02, 5.5) * mm, "mid": v(-5.1, 5.57) * mm, "end": v(-5.2, 5.6) * mm});
            skLineSegment(sketch, "E960", {"start": v(-3.12, 5.6) * mm, "end": v(-2.42, 5.6) * mm});
            skLineSegment(sketch, "E961", {"start": v(-2.25, 5.7) * mm, "end": v(-1.9, 6.3) * mm});
            skLineSegment(sketch, "E962", {"start": v(-1.9, 6.5) * mm, "end": v(-2.25, 7.1) * mm});
            skLineSegment(sketch, "E963", {"start": v(-2.42, 7.2) * mm, "end": v(-3.12, 7.2) * mm});
            skLineSegment(sketch, "E964", {"start": v(-3.3, 7.1) * mm, "end": v(-3.64, 6.5) * mm});
            skLineSegment(sketch, "E965", {"start": v(-3.64, 6.3) * mm, "end": v(-3.3, 5.7) * mm});
            skArc(sketch, "E966.filletArc", {"start": v(-3.12, 7.2) * mm, "mid": v(-3.22, 7.17) * mm, "end": v(-3.3, 7.1) * mm});
            skArc(sketch, "E967.filletArc", {"start": v(-3.64, 6.5) * mm, "mid": v(-3.66, 6.4) * mm, "end": v(-3.64, 6.3) * mm});
            skArc(sketch, "E968.filletArc", {"start": v(-3.3, 5.7) * mm, "mid": v(-3.22, 5.63) * mm, "end": v(-3.12, 5.6) * mm});
            skArc(sketch, "E969.filletArc", {"start": v(-2.42, 5.6) * mm, "mid": v(-2.32, 5.63) * mm, "end": v(-2.25, 5.7) * mm});
            skArc(sketch, "E970.filletArc", {"start": v(-1.9, 6.3) * mm, "mid": v(-1.88, 6.4) * mm, "end": v(-1.9, 6.5) * mm});
            skArc(sketch, "E971.filletArc", {"start": v(-2.25, 7.1) * mm, "mid": v(-2.32, 7.17) * mm, "end": v(-2.42, 7.2) * mm});
            skLineSegment(sketch, "E972", {"start": v(-7.27, -4.8) * mm, "end": v(-6.58, -4.8) * mm});
            skLineSegment(sketch, "E973", {"start": v(-6.4, -4.7) * mm, "end": v(-6.06, -4.1) * mm});
            skLineSegment(sketch, "E974", {"start": v(-6.06, -3.9) * mm, "end": v(-6.4, -3.3) * mm});
            skLineSegment(sketch, "E975", {"start": v(-6.58, -3.2) * mm, "end": v(-7.27, -3.2) * mm});
            skLineSegment(sketch, "E976", {"start": v(-7.45, -3.3) * mm, "end": v(-7.8, -3.9) * mm});
            skLineSegment(sketch, "E977", {"start": v(-7.8, -4.1) * mm, "end": v(-7.45, -4.7) * mm});
            skArc(sketch, "E978.filletArc", {"start": v(-7.27, -3.2) * mm, "mid": v(-7.37, -3.23) * mm, "end": v(-7.45, -3.3) * mm});
            skArc(sketch, "E979.filletArc", {"start": v(-7.8, -3.9) * mm, "mid": v(-7.82, -4) * mm, "end": v(-7.8, -4.1) * mm});
            skArc(sketch, "E980.filletArc", {"start": v(-7.45, -4.7) * mm, "mid": v(-7.37, -4.77) * mm, "end": v(-7.27, -4.8) * mm});
            skArc(sketch, "E981.filletArc", {"start": v(-6.58, -4.8) * mm, "mid": v(-6.48, -4.77) * mm, "end": v(-6.4, -4.7) * mm});
            skArc(sketch, "E982.filletArc", {"start": v(-6.06, -4.1) * mm, "mid": v(-6.04, -4) * mm, "end": v(-6.06, -3.9) * mm});
            skArc(sketch, "E983.filletArc", {"start": v(-6.4, -3.3) * mm, "mid": v(-6.48, -3.23) * mm, "end": v(-6.58, -3.2) * mm});
            skLineSegment(sketch, "E984", {"start": v(-4.5, -6.4) * mm, "end": v(-3.81, -6.4) * mm});
            skLineSegment(sketch, "E985", {"start": v(-3.64, -6.3) * mm, "end": v(-3.3, -5.7) * mm});
            skLineSegment(sketch, "E986", {"start": v(-3.3, -5.5) * mm, "end": v(-3.64, -4.9) * mm});
            skLineSegment(sketch, "E987", {"start": v(-3.81, -4.8) * mm, "end": v(-4.5, -4.8) * mm});
            skLineSegment(sketch, "E988", {"start": v(-4.68, -4.9) * mm, "end": v(-5.02, -5.5) * mm});
            skLineSegment(sketch, "E989", {"start": v(-5.02, -5.7) * mm, "end": v(-4.68, -6.3) * mm});
            skArc(sketch, "E990.filletArc", {"start": v(-4.5, -4.8) * mm, "mid": v(-4.6, -4.83) * mm, "end": v(-4.68, -4.9) * mm});
            skArc(sketch, "E991.filletArc", {"start": v(-5.02, -5.5) * mm, "mid": v(-5.05, -5.6) * mm, "end": v(-5.02, -5.7) * mm});
            skArc(sketch, "E992.filletArc", {"start": v(-4.68, -6.3) * mm, "mid": v(-4.6, -6.37) * mm, "end": v(-4.5, -6.4) * mm});
            skArc(sketch, "E993.filletArc", {"start": v(-3.81, -6.4) * mm, "mid": v(-3.71, -6.37) * mm, "end": v(-3.64, -6.3) * mm});
            skArc(sketch, "E994.filletArc", {"start": v(-3.3, -5.7) * mm, "mid": v(-3.26, -5.6) * mm, "end": v(-3.3, -5.5) * mm});
            skArc(sketch, "E995.filletArc", {"start": v(-3.64, -4.9) * mm, "mid": v(-3.71, -4.83) * mm, "end": v(-3.81, -4.8) * mm});
            skLineSegment(sketch, "E996", {"start": v(2.42, -7.2) * mm, "end": v(3.12, -7.2) * mm});
            skLineSegment(sketch, "E997", {"start": v(3.3, -7.1) * mm, "end": v(3.64, -6.5) * mm});
            skLineSegment(sketch, "E998", {"start": v(3.64, -6.3) * mm, "end": v(3.3, -5.7) * mm});
            skLineSegment(sketch, "E999", {"start": v(3.12, -5.6) * mm, "end": v(2.42, -5.6) * mm});
            skLineSegment(sketch, "E1000", {"start": v(2.25, -5.7) * mm, "end": v(1.9, -6.3) * mm});
            skLineSegment(sketch, "E1001", {"start": v(1.9, -6.5) * mm, "end": v(2.25, -7.1) * mm});
            skArc(sketch, "E1002.filletArc", {"start": v(2.42, -5.6) * mm, "mid": v(2.32, -5.63) * mm, "end": v(2.25, -5.7) * mm});
            skArc(sketch, "E1003.filletArc", {"start": v(1.9, -6.3) * mm, "mid": v(1.88, -6.4) * mm, "end": v(1.9, -6.5) * mm});
            skArc(sketch, "E1004.filletArc", {"start": v(2.25, -7.1) * mm, "mid": v(2.32, -7.17) * mm, "end": v(2.42, -7.2) * mm});
            skArc(sketch, "E1005.filletArc", {"start": v(3.12, -7.2) * mm, "mid": v(3.22, -7.17) * mm, "end": v(3.3, -7.1) * mm});
            skArc(sketch, "E1006.filletArc", {"start": v(3.64, -6.5) * mm, "mid": v(3.66, -6.4) * mm, "end": v(3.64, -6.3) * mm});
            skArc(sketch, "E1007.filletArc", {"start": v(3.3, -5.7) * mm, "mid": v(3.22, -5.63) * mm, "end": v(3.12, -5.6) * mm});
            skLineSegment(sketch, "E1008", {"start": v(3.81, -6.4) * mm, "end": v(4.5, -6.4) * mm});
            skLineSegment(sketch, "E1009", {"start": v(4.68, -6.3) * mm, "end": v(5.02, -5.7) * mm});
            skLineSegment(sketch, "E1010", {"start": v(5.02, -5.5) * mm, "end": v(4.68, -4.9) * mm});
            skLineSegment(sketch, "E1011", {"start": v(4.5, -4.8) * mm, "end": v(3.81, -4.8) * mm});
            skLineSegment(sketch, "E1012", {"start": v(3.64, -4.9) * mm, "end": v(3.3, -5.5) * mm});
            skLineSegment(sketch, "E1013", {"start": v(3.3, -5.7) * mm, "end": v(3.64, -6.3) * mm});
            skArc(sketch, "E1014.filletArc", {"start": v(3.81, -4.8) * mm, "mid": v(3.71, -4.83) * mm, "end": v(3.64, -4.9) * mm});
            skArc(sketch, "E1015.filletArc", {"start": v(3.3, -5.5) * mm, "mid": v(3.26, -5.6) * mm, "end": v(3.3, -5.7) * mm});
            skArc(sketch, "E1016.filletArc", {"start": v(3.64, -6.3) * mm, "mid": v(3.71, -6.37) * mm, "end": v(3.81, -6.4) * mm});
            skArc(sketch, "E1017.filletArc", {"start": v(4.5, -6.4) * mm, "mid": v(4.6, -6.37) * mm, "end": v(4.68, -6.3) * mm});
            skArc(sketch, "E1018.filletArc", {"start": v(5.02, -5.7) * mm, "mid": v(5.05, -5.6) * mm, "end": v(5.02, -5.5) * mm});
            skArc(sketch, "E1019.filletArc", {"start": v(4.68, -4.9) * mm, "mid": v(4.6, -4.83) * mm, "end": v(4.5, -4.8) * mm});
            skLineSegment(sketch, "E1020", {"start": v(5.2, -5.6) * mm, "end": v(5.89, -5.6) * mm});
            skLineSegment(sketch, "E1021", {"start": v(6.06, -5.5) * mm, "end": v(6.4, -4.9) * mm});
            skLineSegment(sketch, "E1022", {"start": v(6.4, -4.7) * mm, "end": v(6.06, -4.1) * mm});
            skLineSegment(sketch, "E1023", {"start": v(5.89, -4) * mm, "end": v(5.2, -4) * mm});
            skLineSegment(sketch, "E1024", {"start": v(5.02, -4.1) * mm, "end": v(4.68, -4.7) * mm});
            skLineSegment(sketch, "E1025", {"start": v(4.68, -4.9) * mm, "end": v(5.02, -5.5) * mm});
            skArc(sketch, "E1026.filletArc", {"start": v(5.2, -4) * mm, "mid": v(5.1, -4.03) * mm, "end": v(5.02, -4.1) * mm});
            skArc(sketch, "E1027.filletArc", {"start": v(4.68, -4.7) * mm, "mid": v(4.65, -4.8) * mm, "end": v(4.68, -4.9) * mm});
            skArc(sketch, "E1028.filletArc", {"start": v(5.02, -5.5) * mm, "mid": v(5.1, -5.57) * mm, "end": v(5.2, -5.6) * mm});
            skArc(sketch, "E1029.filletArc", {"start": v(5.89, -5.6) * mm, "mid": v(5.99, -5.57) * mm, "end": v(6.06, -5.5) * mm});
            skArc(sketch, "E1030.filletArc", {"start": v(6.4, -4.9) * mm, "mid": v(6.44, -4.8) * mm, "end": v(6.4, -4.7) * mm});
            skArc(sketch, "E1031.filletArc", {"start": v(6.06, -4.1) * mm, "mid": v(5.99, -4.03) * mm, "end": v(5.89, -4) * mm});
            skLineSegment(sketch, "E1032", {"start": v(6.58, -4.8) * mm, "end": v(7.27, -4.8) * mm});
            skLineSegment(sketch, "E1033", {"start": v(7.45, -4.7) * mm, "end": v(7.8, -4.1) * mm});
            skLineSegment(sketch, "E1034", {"start": v(7.8, -3.9) * mm, "end": v(7.45, -3.3) * mm});
            skLineSegment(sketch, "E1035", {"start": v(7.27, -3.2) * mm, "end": v(6.58, -3.2) * mm});
            skLineSegment(sketch, "E1036", {"start": v(6.4, -3.3) * mm, "end": v(6.06, -3.9) * mm});
            skLineSegment(sketch, "E1037", {"start": v(6.06, -4.1) * mm, "end": v(6.4, -4.7) * mm});
            skArc(sketch, "E1038.filletArc", {"start": v(6.58, -3.2) * mm, "mid": v(6.48, -3.23) * mm, "end": v(6.4, -3.3) * mm});
            skArc(sketch, "E1039.filletArc", {"start": v(6.06, -3.9) * mm, "mid": v(6.04, -4) * mm, "end": v(6.06, -4.1) * mm});
            skArc(sketch, "E1040.filletArc", {"start": v(6.4, -4.7) * mm, "mid": v(6.48, -4.77) * mm, "end": v(6.58, -4.8) * mm});
            skArc(sketch, "E1041.filletArc", {"start": v(7.27, -4.8) * mm, "mid": v(7.37, -4.77) * mm, "end": v(7.45, -4.7) * mm});
            skArc(sketch, "E1042.filletArc", {"start": v(7.8, -4.1) * mm, "mid": v(7.82, -4) * mm, "end": v(7.8, -3.9) * mm});
            skArc(sketch, "E1043.filletArc", {"start": v(7.45, -3.3) * mm, "mid": v(7.37, -3.23) * mm, "end": v(7.27, -3.2) * mm});
            skLineSegment(sketch, "E1044", {"start": v(-3.12, -7.2) * mm, "end": v(-2.42, -7.2) * mm});
            skLineSegment(sketch, "E1045", {"start": v(-2.25, -7.1) * mm, "end": v(-1.9, -6.5) * mm});
            skLineSegment(sketch, "E1046", {"start": v(-1.9, -6.3) * mm, "end": v(-2.25, -5.7) * mm});
            skLineSegment(sketch, "E1047", {"start": v(-2.42, -5.6) * mm, "end": v(-3.12, -5.6) * mm});
            skLineSegment(sketch, "E1048", {"start": v(-3.3, -5.7) * mm, "end": v(-3.64, -6.3) * mm});
            skLineSegment(sketch, "E1049", {"start": v(-3.64, -6.5) * mm, "end": v(-3.3, -7.1) * mm});
            skArc(sketch, "E1050.filletArc", {"start": v(-3.12, -5.6) * mm, "mid": v(-3.22, -5.63) * mm, "end": v(-3.3, -5.7) * mm});
            skArc(sketch, "E1051.filletArc", {"start": v(-3.64, -6.3) * mm, "mid": v(-3.66, -6.4) * mm, "end": v(-3.64, -6.5) * mm});
            skArc(sketch, "E1052.filletArc", {"start": v(-3.3, -7.1) * mm, "mid": v(-3.22, -7.17) * mm, "end": v(-3.12, -7.2) * mm});
            skArc(sketch, "E1053.filletArc", {"start": v(-2.42, -7.2) * mm, "mid": v(-2.32, -7.17) * mm, "end": v(-2.25, -7.1) * mm});
            skArc(sketch, "E1054.filletArc", {"start": v(-1.9, -6.5) * mm, "mid": v(-1.88, -6.4) * mm, "end": v(-1.9, -6.3) * mm});
            skArc(sketch, "E1055.filletArc", {"start": v(-2.25, -5.7) * mm, "mid": v(-2.32, -5.63) * mm, "end": v(-2.42, -5.6) * mm});
            skLineSegment(sketch, "E1056", {"start": v(-1.73, -8) * mm, "end": v(-1.04, -8) * mm});
            skLineSegment(sketch, "E1057", {"start": v(-0.87, -7.9) * mm, "end": v(-0.52, -7.3) * mm});
            skLineSegment(sketch, "E1058", {"start": v(-0.52, -7.1) * mm, "end": v(-0.87, -6.5) * mm});
            skLineSegment(sketch, "E1059", {"start": v(-1.04, -6.4) * mm, "end": v(-1.73, -6.4) * mm});
            skLineSegment(sketch, "E1060", {"start": v(-1.9, -6.5) * mm, "end": v(-2.25, -7.1) * mm});
            skLineSegment(sketch, "E1061", {"start": v(-2.25, -7.3) * mm, "end": v(-1.9, -7.9) * mm});
            skArc(sketch, "E1062.filletArc", {"start": v(-1.73, -6.4) * mm, "mid": v(-1.83, -6.43) * mm, "end": v(-1.9, -6.5) * mm});
            skArc(sketch, "E1063.filletArc", {"start": v(-2.25, -7.1) * mm, "mid": v(-2.28, -7.2) * mm, "end": v(-2.25, -7.3) * mm});
            skArc(sketch, "E1064.filletArc", {"start": v(-1.9, -7.9) * mm, "mid": v(-1.83, -7.97) * mm, "end": v(-1.73, -8) * mm});
            skArc(sketch, "E1065.filletArc", {"start": v(-1.04, -8) * mm, "mid": v(-0.94, -7.97) * mm, "end": v(-0.87, -7.9) * mm});
            skArc(sketch, "E1066.filletArc", {"start": v(-0.52, -7.3) * mm, "mid": v(-0.5, -7.2) * mm, "end": v(-0.52, -7.1) * mm});
            skArc(sketch, "E1067.filletArc", {"start": v(-0.87, -6.5) * mm, "mid": v(-0.94, -6.43) * mm, "end": v(-1.04, -6.4) * mm});
            skLineSegment(sketch, "E1068", {"start": v(1.04, -8) * mm, "end": v(1.73, -8) * mm});
            skLineSegment(sketch, "E1069", {"start": v(1.9, -7.9) * mm, "end": v(2.25, -7.3) * mm});
            skLineSegment(sketch, "E1070", {"start": v(2.25, -7.1) * mm, "end": v(1.9, -6.5) * mm});
            skLineSegment(sketch, "E1071", {"start": v(1.73, -6.4) * mm, "end": v(1.04, -6.4) * mm});
            skLineSegment(sketch, "E1072", {"start": v(0.87, -6.5) * mm, "end": v(0.52, -7.1) * mm});
            skLineSegment(sketch, "E1073", {"start": v(0.52, -7.3) * mm, "end": v(0.87, -7.9) * mm});
            skArc(sketch, "E1074.filletArc", {"start": v(1.04, -6.4) * mm, "mid": v(0.94, -6.43) * mm, "end": v(0.87, -6.5) * mm});
            skArc(sketch, "E1075.filletArc", {"start": v(0.52, -7.1) * mm, "mid": v(0.5, -7.2) * mm, "end": v(0.52, -7.3) * mm});
            skArc(sketch, "E1076.filletArc", {"start": v(0.87, -7.9) * mm, "mid": v(0.94, -7.97) * mm, "end": v(1.04, -8) * mm});
            skArc(sketch, "E1077.filletArc", {"start": v(1.73, -8) * mm, "mid": v(1.83, -7.97) * mm, "end": v(1.9, -7.9) * mm});
            skArc(sketch, "E1078.filletArc", {"start": v(2.25, -7.3) * mm, "mid": v(2.28, -7.2) * mm, "end": v(2.25, -7.1) * mm});
            skArc(sketch, "E1079.filletArc", {"start": v(1.9, -6.5) * mm, "mid": v(1.83, -6.43) * mm, "end": v(1.73, -6.4) * mm});
            skLineSegment(sketch, "E1080", {"start": v(-0.35, -8.8) * mm, "end": v(0.35, -8.8) * mm});
            skLineSegment(sketch, "E1081", {"start": v(0.52, -8.7) * mm, "end": v(0.87, -8.1) * mm});
            skLineSegment(sketch, "E1082", {"start": v(0.87, -7.9) * mm, "end": v(0.52, -7.3) * mm});
            skLineSegment(sketch, "E1083", {"start": v(0.35, -7.2) * mm, "end": v(-0.35, -7.2) * mm});
            skLineSegment(sketch, "E1084", {"start": v(-0.52, -7.3) * mm, "end": v(-0.87, -7.9) * mm});
            skLineSegment(sketch, "E1085", {"start": v(-0.87, -8.1) * mm, "end": v(-0.52, -8.7) * mm});
            skArc(sketch, "E1086.filletArc", {"start": v(-0.35, -7.2) * mm, "mid": v(-0.45, -7.23) * mm, "end": v(-0.52, -7.3) * mm});
            skArc(sketch, "E1087.filletArc", {"start": v(-0.87, -7.9) * mm, "mid": v(-0.9, -8) * mm, "end": v(-0.87, -8.1) * mm});
            skArc(sketch, "E1088.filletArc", {"start": v(-0.52, -8.7) * mm, "mid": v(-0.45, -8.77) * mm, "end": v(-0.35, -8.8) * mm});
            skArc(sketch, "E1089.filletArc", {"start": v(0.35, -8.8) * mm, "mid": v(0.45, -8.77) * mm, "end": v(0.52, -8.7) * mm});
            skArc(sketch, "E1090.filletArc", {"start": v(0.87, -8.1) * mm, "mid": v(0.9, -8) * mm, "end": v(0.87, -7.9) * mm});
            skArc(sketch, "E1091.filletArc", {"start": v(0.52, -7.3) * mm, "mid": v(0.45, -7.23) * mm, "end": v(0.35, -7.2) * mm});
            skLineSegment(sketch, "E1092", {"start": v(7.8, 4.1) * mm, "end": v(11, 4.1) * mm});
            skLineSegment(sketch, "E1093", {"start": v(-7.8, -4.1) * mm, "end": v(-11, -4.1) * mm});
            skSolve(sketch);
        }
        {
            var Q0;
            Q0=sQuery(id+"F1.wireOp",EDGE,"E1092");
            var Q1;
            Q1=sQuery(id+"F1.wireOp",VERTEX,"E1092.end");
            cPlane(context, id + "F2", {"entities" : qUnion([Q0, Q1]), "cplaneType" : CPlaneType.LINE_POINT, "offset" : 25 * mm, "width" : 150 * mm, "height" : 150 * mm});
        }
        {
            var Q0;
            Q0=qCreatedBy(id+"F2.planeOp",FACE);
            var sketch = newSketch(context, id + "F3", { "sketchPlane" : qUnion([Q0])});
            skCircle(sketch, "E1094", {"center": v(4.1, 0.21) * mm, "radius": 0.2 * mm});
            skSolve(sketch);
        }
        {
            var Q0;
            Q0=makeQuery(id+"F3.imprint","IMPRINT",FACE,{"disambiguationData":[TD([[makeQuery(id+"F3.imprint","IMPRINT",EDGE,{"derivedFrom":sQuery(id+"F3.wireOp",EDGE,"E1094")}),1.0]])]});
            var Q1;
            Q1=sQuery(id+"F1.wireOp",EDGE,"E1092");
            var Q2;
            Q2=sQuery(id+"F1.wireOp",EDGE,"E830");
            var Q3;
            Q3=sQuery(id+"F1.wireOp",EDGE,"E839.filletArc");
            var Q4;
            Q4=sQuery(id+"F1.wireOp",EDGE,"E831");
            var Q5;
            Q5=sQuery(id+"F1.wireOp",EDGE,"E834.filletArc");
            var Q6;
            Q6=sQuery(id+"F1.wireOp",EDGE,"E832");
            var Q7;
            Q7=sQuery(id+"F1.wireOp",EDGE,"E849.filletArc");
            var Q8;
            Q8=sQuery(id+"F1.wireOp",EDGE,"E840");
            var Q9;
            Q9=sQuery(id+"F1.wireOp",EDGE,"E848.filletArc");
            var Q10;
            Q10=sQuery(id+"F1.wireOp",EDGE,"E845");
            var Q11;
            Q11=sQuery(id+"F1.wireOp",EDGE,"E847.filletArc");
            var Q12;
            Q12=sQuery(id+"F1.wireOp",EDGE,"E844");
            var Q13;
            Q13=sQuery(id+"F1.wireOp",EDGE,"E862.filletArc");
            var Q14;
            Q14=sQuery(id+"F1.wireOp",EDGE,"E854");
            var Q15;
            Q15=sQuery(id+"F1.wireOp",EDGE,"E863.filletArc");
            var Q16;
            Q16=sQuery(id+"F1.wireOp",EDGE,"E855");
            var Q17;
            Q17=sQuery(id+"F1.wireOp",EDGE,"E858.filletArc");
            var Q18;
            Q18=sQuery(id+"F1.wireOp",EDGE,"E856");
            var Q19;
            Q19=sQuery(id+"F1.wireOp",EDGE,"E873.filletArc");
            var Q20;
            Q20=sQuery(id+"F1.wireOp",EDGE,"E864");
            var Q21;
            Q21=sQuery(id+"F1.wireOp",EDGE,"E872.filletArc");
            var Q22;
            Q22=sQuery(id+"F1.wireOp",EDGE,"E638");
            var Q23;
            Q23=sQuery(id+"F1.wireOp",EDGE,"E871.filletArc");
            var Q24;
            Q24=sQuery(id+"F1.wireOp",EDGE,"E877");
            var Q25;
            Q25=sQuery(id+"F1.wireOp",EDGE,"E886.filletArc");
            var Q26;
            Q26=sQuery(id+"F1.wireOp",EDGE,"E878");
            var Q27;
            Q27=sQuery(id+"F1.wireOp",EDGE,"E887.filletArc");
            var Q28;
            Q28=sQuery(id+"F1.wireOp",EDGE,"E879");
            var Q29;
            Q29=sQuery(id+"F1.wireOp",EDGE,"E882.filletArc");
            var Q30;
            Q30=sQuery(id+"F1.wireOp",EDGE,"E880");
            var Q31;
            Q31=sQuery(id+"F1.wireOp",EDGE,"E909.filletArc");
            var Q32;
            Q32=sQuery(id+"F1.wireOp",EDGE,"E651");
            var Q33;
            Q33=sQuery(id+"F1.wireOp",EDGE,"E908.filletArc");
            var Q34;
            Q34=sQuery(id+"F1.wireOp",EDGE,"E890");
            var Q35;
            Q35=sQuery(id+"F1.wireOp",EDGE,"E899.filletArc");
            var Q36;
            Q36=sQuery(id+"F1.wireOp",EDGE,"E891");
            var Q37;
            Q37=sQuery(id+"F1.wireOp",EDGE,"E894.filletArc");
            var Q38;
            Q38=sQuery(id+"F1.wireOp",EDGE,"E892");
            var Q39;
            Q39=sQuery(id+"F1.wireOp",EDGE,"E895.filletArc");
            var Q40;
            Q40=sQuery(id+"F1.wireOp",EDGE,"E893");
            var Q41;
            Q41=sQuery(id+"F1.wireOp",EDGE,"E970.filletArc");
            var Q42;
            Q42=sQuery(id+"F1.wireOp",EDGE,"E664");
            var Q43;
            Q43=sQuery(id+"F1.wireOp",EDGE,"E969.filletArc");
            var Q44;
            Q44=sQuery(id+"F1.wireOp",EDGE,"E960");
            var Q45;
            Q45=sQuery(id+"F1.wireOp",EDGE,"E968.filletArc");
            var Q46;
            Q46=sQuery(id+"F1.wireOp",EDGE,"E965");
            var Q47;
            Q47=sQuery(id+"F1.wireOp",EDGE,"E923.filletArc");
            var Q48;
            Q48=sQuery(id+"F1.wireOp",EDGE,"E915");
            var Q49;
            Q49=sQuery(id+"F1.wireOp",EDGE,"E918.filletArc");
            var Q50;
            Q50=sQuery(id+"F1.wireOp",EDGE,"E916");
            var Q51;
            Q51=sQuery(id+"F1.wireOp",EDGE,"E919.filletArc");
            var Q52;
            Q52=sQuery(id+"F1.wireOp",EDGE,"E950");
            var Q53;
            Q53=sQuery(id+"F1.wireOp",EDGE,"E958.filletArc");
            var Q54;
            Q54=sQuery(id+"F1.wireOp",EDGE,"E688");
            var Q55;
            Q55=sQuery(id+"F1.wireOp",EDGE,"E957.filletArc");
            var Q56;
            Q56=sQuery(id+"F1.wireOp",EDGE,"E699");
            var Q57;
            Q57=sQuery(id+"F1.wireOp",EDGE,"E956.filletArc");
            var Q58;
            Q58=sQuery(id+"F1.wireOp",EDGE,"E938");
            var Q59;
            Q59=sQuery(id+"F1.wireOp",EDGE,"E947.filletArc");
            var Q60;
            Q60=sQuery(id+"F1.wireOp",EDGE,"E939");
            var Q61;
            Q61=sQuery(id+"F1.wireOp",EDGE,"E942.filletArc");
            var Q62;
            Q62=sQuery(id+"F1.wireOp",EDGE,"E940");
            var Q63;
            Q63=sQuery(id+"F1.wireOp",EDGE,"E943.filletArc");
            var Q64;
            Q64=sQuery(id+"F1.wireOp",EDGE,"E941");
            var Q65;
            Q65=sQuery(id+"F1.wireOp",EDGE,"E944.filletArc");
            var Q66;
            Q66=sQuery(id+"F1.wireOp",EDGE,"E936");
            var Q67;
            Q67=sQuery(id+"F1.wireOp",EDGE,"E779.filletArc");
            var Q68;
            Q68=sQuery(id+"F1.wireOp",EDGE,"E701");
            var Q69;
            Q69=sQuery(id+"F1.wireOp",EDGE,"E704.filletArc");
            var Q70;
            Q70=sQuery(id+"F1.wireOp",EDGE,"E696");
            var Q71;
            Q71=sQuery(id+"F1.wireOp",EDGE,"E705.filletArc");
            var Q72;
            Q72=sQuery(id+"F1.wireOp",EDGE,"E316");
            var Q73;
            Q73=sQuery(id+"F1.wireOp",EDGE,"E318.filletArc");
            var Q74;
            Q74=sQuery(id+"F1.wireOp",EDGE,"E315");
            var Q75;
            Q75=sQuery(id+"F1.wireOp",EDGE,"E693.filletArc");
            var Q76;
            Q76=sQuery(id+"F1.wireOp",EDGE,"E685");
            var Q77;
            Q77=sQuery(id+"F1.wireOp",EDGE,"E306.filletArc");
            var Q78;
            Q78=sQuery(id+"F1.wireOp",EDGE,"E672");
            var Q79;
            Q79=sQuery(id+"F1.wireOp",EDGE,"E681.filletArc");
            var Q80;
            Q80=sQuery(id+"F1.wireOp",EDGE,"E294.filletArc");
            var Q81;
            Q81=sQuery(id+"F1.wireOp",EDGE,"E291");
            var Q82;
            Q82=sQuery(id+"F1.wireOp",EDGE,"E292");
            var Q83;
            Q83=sQuery(id+"F1.wireOp",EDGE,"E669.filletArc");
            var Q84;
            Q84=sQuery(id+"F1.wireOp",EDGE,"E436");
            var Q85;
            Q85=sQuery(id+"F1.wireOp",EDGE,"E438.filletArc");
            var Q86;
            Q86=sQuery(id+"F1.wireOp",EDGE,"E648");
            var Q87;
            Q87=sQuery(id+"F1.wireOp",EDGE,"E443.filletArc");
            var Q88;
            Q88=sQuery(id+"F1.wireOp",EDGE,"E434");
            var Q89;
            Q89=sQuery(id+"F1.wireOp",EDGE,"E644.filletArc");
            var Q90;
            Q90=sQuery(id+"F1.wireOp",EDGE,"E636");
            var Q91;
            Q91=sQuery(id+"F1.wireOp",EDGE,"E287.filletArc");
            var Q92;
            Q92=sQuery(id+"F1.wireOp",EDGE,"E278");
            var Q93;
            Q93=sQuery(id+"F1.wireOp",EDGE,"E620.filletArc");
            var Q94;
            Q94=sQuery(id+"F1.wireOp",EDGE,"E267");
            var Q95;
            Q95=sQuery(id+"F1.wireOp",EDGE,"E275.filletArc");
            var Q96;
            Q96=sQuery(id+"F1.wireOp",EDGE,"E266");
            var Q97;
            Q97=sQuery(id+"F1.wireOp",EDGE,"E632.filletArc");
            var Q98;
            Q98=sQuery(id+"F1.wireOp",EDGE,"E624");
            var Q99;
            Q99=sQuery(id+"F1.wireOp",EDGE,"E263.filletArc");
            var Q100;
            Q100=sQuery(id+"F1.wireOp",EDGE,"E725");
            var Q101;
            Q101=sQuery(id+"F1.wireOp",EDGE,"E728.filletArc");
            var Q102;
            Q102=sQuery(id+"F1.wireOp",EDGE,"E720");
            var Q103;
            Q103=sQuery(id+"F1.wireOp",EDGE,"E729.filletArc");
            var Q104;
            Q104=sQuery(id+"F1.wireOp",EDGE,"E796");
            var Q105;
            Q105=sQuery(id+"F1.wireOp",EDGE,"E798.filletArc");
            var Q106;
            Q106=sQuery(id+"F1.wireOp",EDGE,"E828");
            var Q107;
            Q107=sQuery(id+"F1.wireOp",EDGE,"E803.filletArc");
            var Q108;
            Q108=sQuery(id+"F1.wireOp",EDGE,"E794");
            var Q109;
            Q109=sQuery(id+"F1.wireOp",EDGE,"E802.filletArc");
            var Q110;
            Q110=sQuery(id+"F1.wireOp",EDGE,"E793");
            var Q111;
            Q111=sQuery(id+"F1.wireOp",EDGE,"E801.filletArc");
            var Q112;
            Q112=sQuery(id+"F1.wireOp",EDGE,"E783");
            var Q113;
            Q113=sQuery(id+"F1.wireOp",EDGE,"E786.filletArc");
            var Q114;
            Q114=sQuery(id+"F1.wireOp",EDGE,"E784");
            var Q115;
            Q115=sQuery(id+"F1.wireOp",EDGE,"E717.filletArc");
            var Q116;
            Q116=sQuery(id+"F1.wireOp",EDGE,"E603");
            var Q117;
            Q117=sQuery(id+"F1.wireOp",EDGE,"E716.filletArc");
            var Q118;
            Q118=sQuery(id+"F1.wireOp",EDGE,"E251.filletArc");
            var Q119;
            Q119=sQuery(id+"F1.wireOp",EDGE,"E252");
            var Q120;
            Q120=sQuery(id+"F1.wireOp",EDGE,"E260.filletArc");
            var Q121;
            Q121=sQuery(id+"F1.wireOp",EDGE,"E170");
            var Q122;
            Q122=sQuery(id+"F1.wireOp",EDGE,"E713");
            var Q123;
            Q123=sQuery(id+"F1.wireOp",EDGE,"E179.filletArc");
            var Q124;
            Q124=sQuery(id+"F1.wireOp",EDGE,"E171");
            var Q125;
            Q125=sQuery(id+"F1.wireOp",EDGE,"E272.filletArc");
            var Q126;
            Q126=sQuery(id+"F1.wireOp",EDGE,"E194");
            var Q127;
            Q127=sQuery(id+"F1.wireOp",EDGE,"E203.filletArc");
            var Q128;
            Q128=sQuery(id+"F1.wireOp",EDGE,"E276");
            var Q129;
            Q129=sQuery(id+"F1.wireOp",EDGE,"E284.filletArc");
            var Q130;
            Q130=sQuery(id+"F1.wireOp",EDGE,"E281");
            var Q131;
            Q131=sQuery(id+"F1.wireOp",EDGE,"E215.filletArc");
            var Q132;
            Q132=sQuery(id+"F1.wireOp",EDGE,"E432");
            var Q133;
            Q133=sQuery(id+"F1.wireOp",EDGE,"E210.filletArc");
            var Q134;
            Q134=sQuery(id+"F1.wireOp",EDGE,"E289");
            var Q135;
            Q135=sQuery(id+"F1.wireOp",EDGE,"E297.filletArc");
            var Q136;
            Q136=sQuery(id+"F1.wireOp",EDGE,"E183");
            var Q137;
            Q137=sQuery(id+"F1.wireOp",EDGE,"E186.filletArc");
            var Q138;
            Q138=sQuery(id+"F1.wireOp",EDGE,"E184");
            var Q139;
            Q139=sQuery(id+"F1.wireOp",EDGE,"E309.filletArc");
            var Q140;
            Q140=sQuery(id+"F1.wireOp",EDGE,"E300");
            var Q141;
            Q141=sQuery(id+"F1.wireOp",EDGE,"E222.filletArc");
            var Q142;
            Q142=sQuery(id+"F1.wireOp",EDGE,"E220");
            var Q143;
            Q143=sQuery(id+"F1.wireOp",EDGE,"E321.filletArc");
            var Q144;
            Q144=sQuery(id+"F1.wireOp",EDGE,"E312");
            var Q145;
            Q145=sQuery(id+"F1.wireOp",EDGE,"E330.filletArc");
            var Q146;
            Q146=sQuery(id+"F1.wireOp",EDGE,"E328");
            var Q147;
            Q147=sQuery(id+"F1.wireOp",EDGE,"E453.filletArc");
            var Q148;
            Q148=sQuery(id+"F1.wireOp",EDGE,"E444");
            var Q149;
            Q149=sQuery(id+"F1.wireOp",EDGE,"E452.filletArc");
            var Q150;
            Q150=sQuery(id+"F1.wireOp",EDGE,"E758");
            var Q151;
            Q151=sQuery(id+"F1.wireOp",EDGE,"E767.filletArc");
            var Q152;
            Q152=sQuery(id+"F1.wireOp",EDGE,"E768");
            var Q153;
            Q153=sQuery(id+"F1.wireOp",EDGE,"E762.filletArc");
            var Q154;
            Q154=sQuery(id+"F1.wireOp",EDGE,"E760");
            var Q155;
            Q155=sQuery(id+"F1.wireOp",EDGE,"E763.filletArc");
            var Q156;
            Q156=sQuery(id+"F1.wireOp",EDGE,"E761");
            var Q157;
            Q157=sQuery(id+"F1.wireOp",EDGE,"E764.filletArc");
            var Q158;
            Q158=sQuery(id+"F1.wireOp",EDGE,"E747");
            var Q159;
            Q159=sQuery(id+"F1.wireOp",EDGE,"E755.filletArc");
            var Q160;
            Q160=sQuery(id+"F1.wireOp",EDGE,"E746");
            var Q161;
            Q161=sQuery(id+"F1.wireOp",EDGE,"E464.filletArc");
            var Q162;
            Q162=sQuery(id+"F1.wireOp",EDGE,"E456");
            var Q163;
            Q163=sQuery(id+"F1.wireOp",EDGE,"E465.filletArc");
            var Q164;
            Q164=sQuery(id+"F1.wireOp",EDGE,"E457");
            var Q165;
            Q165=sQuery(id+"F1.wireOp",EDGE,"E342.filletArc");
            var Q166;
            Q166=sQuery(id+"F1.wireOp",EDGE,"E324");
            var Q167;
            Q167=sQuery(id+"F1.wireOp",EDGE,"E333.filletArc");
            var Q168;
            Q168=sQuery(id+"F1.wireOp",EDGE,"E88");
            var Q169;
            Q169=sQuery(id+"F1.wireOp",EDGE,"E90.filletArc");
            var Q170;
            Q170=sQuery(id+"F1.wireOp",EDGE,"E225.filletArc");
            var Q171;
            Q171=sQuery(id+"F1.wireOp",EDGE,"E216");
            var Q172;
            Q172=sQuery(id+"F1.wireOp",EDGE,"E217");
            var Q173;
            Q173=sQuery(id+"F1.wireOp",EDGE,"E18.filletArc");
            var Q174;
            Q174=sQuery(id+"F1.wireOp",EDGE,"E180");
            var Q175;
            Q175=sQuery(id+"F1.wireOp",EDGE,"E189.filletArc");
            var Q176;
            Q176=sQuery(id+"F1.wireOp",EDGE,"E76");
            var Q177;
            Q177=sQuery(id+"F1.wireOp",EDGE,"E78.filletArc");
            var Q178;
            Q178=sQuery(id+"F1.wireOp",EDGE,"E204");
            var Q179;
            Q179=sQuery(id+"F1.wireOp",EDGE,"E83.filletArc");
            var Q180;
            Q180=sQuery(id+"F1.wireOp",EDGE,"E74");
            var Q181;
            Q181=sQuery(id+"F1.wireOp",EDGE,"E200.filletArc");
            var Q182;
            Q182=sQuery(id+"F1.wireOp",EDGE,"E192");
            var Q183;
            Q183=sQuery(id+"F1.wireOp",EDGE,"E71.filletArc");
            var Q184;
            Q184=sQuery(id+"F1.wireOp",EDGE,"E62");
            var Q185;
            Q185=sQuery(id+"F1.wireOp",EDGE,"E176.filletArc");
            var Q186;
            Q186=sQuery(id+"F1.wireOp",EDGE,"E168");
            var Q187;
            Q187=sQuery(id+"F1.wireOp",EDGE,"E143.filletArc");
            var Q188;
            Q188=sQuery(id+"F1.wireOp",EDGE,"E134");
            var Q189;
            Q189=sQuery(id+"F1.wireOp",EDGE,"E248.filletArc");
            var Q190;
            Q190=sQuery(id+"F1.wireOp",EDGE,"E231");
            var Q191;
            Q191=sQuery(id+"F1.wireOp",EDGE,"E239.filletArc");
            var Q192;
            Q192=sQuery(id+"F1.wireOp",EDGE,"E605");
            var Q193;
            Q193=sQuery(id+"F1.wireOp",EDGE,"E608.filletArc");
            var Q194;
            Q194=sQuery(id+"F1.wireOp",EDGE,"E600");
            var Q195;
            Q195=sQuery(id+"F1.wireOp",EDGE,"E609.filletArc");
            var Q196;
            Q196=sQuery(id+"F1.wireOp",EDGE,"E601");
            var Q197;
            Q197=sQuery(id+"F1.wireOp",EDGE,"E810.filletArc");
            var Q198;
            Q198=sQuery(id+"F1.wireOp",EDGE,"E780");
            var Q199;
            Q199=sQuery(id+"F1.wireOp",EDGE,"E815.filletArc");
            var Q200;
            Q200=sQuery(id+"F1.wireOp",EDGE,"E806");
            var Q201;
            Q201=sQuery(id+"F1.wireOp",EDGE,"E814.filletArc");
            var Q202;
            Q202=sQuery(id+"F1.wireOp",EDGE,"E805");
            var Q203;
            Q203=sQuery(id+"F1.wireOp",EDGE,"E813.filletArc");
            var Q204;
            Q204=sQuery(id+"F1.wireOp",EDGE,"E804");
            var Q205;
            Q205=sQuery(id+"F1.wireOp",EDGE,"E822.filletArc");
            var Q206;
            Q206=sQuery(id+"F1.wireOp",EDGE,"E820");
            var Q207;
            Q207=sQuery(id+"F1.wireOp",EDGE,"E597.filletArc");
            var Q208;
            Q208=sQuery(id+"F1.wireOp",EDGE,"E596.filletArc");
            var Q209;
            Q209=sQuery(id+"F1.wireOp",EDGE,"E422");
            var Q210;
            Q210=sQuery(id+"F1.wireOp",EDGE,"E431.filletArc");
            var Q211;
            Q211=sQuery(id+"F1.wireOp",EDGE,"E423");
            var Q212;
            Q212=sQuery(id+"F1.wireOp",EDGE,"E236.filletArc");
            var Q213;
            Q213=sQuery(id+"F1.wireOp",EDGE,"E233");
            var Q214;
            Q214=sQuery(id+"F1.wireOp",EDGE,"E588");
            var Q215;
            Q215=sQuery(id+"F1.wireOp",EDGE,"E167.filletArc");
            var Q216;
            Q216=sQuery(id+"F1.wireOp",EDGE,"E132");
            var Q217;
            Q217=sQuery(id+"F1.wireOp",EDGE,"E140.filletArc");
            var Q218;
            Q218=sQuery(id+"F1.wireOp",EDGE,"E137");
            var Q219;
            Q219=sQuery(id+"F1.wireOp",EDGE,"E59.filletArc");
            var Q220;
            Q220=sQuery(id+"F1.wireOp",EDGE,"E60");
            var Q221;
            Q221=sQuery(id+"F1.wireOp",EDGE,"E68.filletArc");
            var Q222;
            Q222=sQuery(id+"F1.wireOp",EDGE,"E65");
            var Q223;
            Q223=sQuery(id+"F1.wireOp",EDGE,"E11.filletArc");
            var Q224;
            Q224=sQuery(id+"F1.wireOp",EDGE,"E72");
            var Q225;
            Q225=sQuery(id+"F1.wireOp",EDGE,"E6.filletArc");
            var Q226;
            Q226=sQuery(id+"F1.wireOp",EDGE,"E4");
            var Q227;
            Q227=sQuery(id+"F1.wireOp",EDGE,"E21.filletArc");
            var Q228;
            Q228=sQuery(id+"F1.wireOp",EDGE,"E27");
            var Q229;
            Q229=sQuery(id+"F1.wireOp",EDGE,"E30.filletArc");
            var Q230;
            Q230=sQuery(id+"F1.wireOp",EDGE,"E28");
            var Q231;
            Q231=sQuery(id+"F1.wireOp",EDGE,"E93.filletArc");
            var Q232;
            Q232=sQuery(id+"F1.wireOp",EDGE,"E84");
            var Q233;
            Q233=sQuery(id+"F1.wireOp",EDGE,"E102.filletArc");
            var Q234;
            Q234=sQuery(id+"F1.wireOp",EDGE,"E100");
            var Q235;
            Q235=sQuery(id+"F1.wireOp",EDGE,"E345.filletArc");
            var Q236;
            Q236=sQuery(id+"F1.wireOp",EDGE,"E336");
            var Q237;
            Q237=sQuery(id+"F1.wireOp",EDGE,"E354.filletArc");
            var Q238;
            Q238=sQuery(id+"F1.wireOp",EDGE,"E469");
            var Q239;
            Q239=sQuery(id+"F1.wireOp",EDGE,"E477.filletArc");
            var Q240;
            Q240=sQuery(id+"F1.wireOp",EDGE,"E468");
            var Q241;
            Q241=sQuery(id+"F1.wireOp",EDGE,"E476.filletArc");
            var Q242;
            Q242=sQuery(id+"F1.wireOp",EDGE,"E734");
            var Q243;
            Q243=sQuery(id+"F1.wireOp",EDGE,"E743.filletArc");
            var Q244;
            Q244=sQuery(id+"F1.wireOp",EDGE,"E735");
            var Q245;
            Q245=sQuery(id+"F1.wireOp",EDGE,"E738.filletArc");
            var Q246;
            Q246=sQuery(id+"F1.wireOp",EDGE,"E736");
            var Q247;
            Q247=sQuery(id+"F1.wireOp",EDGE,"E739.filletArc");
            var Q248;
            Q248=sQuery(id+"F1.wireOp",EDGE,"E737");
            var Q249;
            Q249=sQuery(id+"F1.wireOp",EDGE,"E740.filletArc");
            var Q250;
            Q250=sQuery(id+"F1.wireOp",EDGE,"E975");
            var Q251;
            Q251=sQuery(id+"F1.wireOp",EDGE,"E983.filletArc");
            var Q252;
            Q252=sQuery(id+"F1.wireOp",EDGE,"E974");
            var Q253;
            Q253=sQuery(id+"F1.wireOp",EDGE,"E488.filletArc");
            var Q254;
            Q254=sQuery(id+"F1.wireOp",EDGE,"E927");
            var Q255;
            Q255=sQuery(id+"F1.wireOp",EDGE,"E489.filletArc");
            var Q256;
            Q256=sQuery(id+"F1.wireOp",EDGE,"E481");
            var Q257;
            Q257=sQuery(id+"F1.wireOp",EDGE,"E498.filletArc");
            var Q258;
            Q258=sQuery(id+"F1.wireOp",EDGE,"E348");
            var Q259;
            Q259=sQuery(id+"F1.wireOp",EDGE,"E357.filletArc");
            var Q260;
            Q260=sQuery(id+"F1.wireOp",EDGE,"E364");
            var Q261;
            Q261=sQuery(id+"F1.wireOp",EDGE,"E366.filletArc");
            var Q262;
            Q262=sQuery(id+"F1.wireOp",EDGE,"E363");
            var Q263;
            Q263=sQuery(id+"F1.wireOp",EDGE,"E105.filletArc");
            var Q264;
            Q264=sQuery(id+"F1.wireOp",EDGE,"E124");
            var Q265;
            Q265=sQuery(id+"F1.wireOp",EDGE,"E126.filletArc");
            var Q266;
            Q266=sQuery(id+"F1.wireOp",EDGE,"E123");
            var Q267;
            Q267=sQuery(id+"F1.wireOp",EDGE,"E33.filletArc");
            var Q268;
            Q268=sQuery(id+"F1.wireOp",EDGE,"E25");
            var Q269;
            Q269=sQuery(id+"F1.wireOp",EDGE,"E42.filletArc");
            var Q270;
            Q270=sQuery(id+"F1.wireOp",EDGE,"E39");
            var Q271;
            Q271=sQuery(id+"F1.wireOp",EDGE,"E47.filletArc");
            var Q272;
            Q272=sQuery(id+"F1.wireOp",EDGE,"E38");
            var Q273;
            Q273=sQuery(id+"F1.wireOp",EDGE,"E56.filletArc");
            var Q274;
            Q274=sQuery(id+"F1.wireOp",EDGE,"E147");
            var Q275;
            Q275=sQuery(id+"F1.wireOp",EDGE,"E155.filletArc");
            var Q276;
            Q276=sQuery(id+"F1.wireOp",EDGE,"E146");
            var Q277;
            Q277=sQuery(id+"F1.wireOp",EDGE,"E164.filletArc");
            var Q278;
            Q278=sQuery(id+"F1.wireOp",EDGE,"E156");
            var Q279;
            Q279=sQuery(id+"F1.wireOp",EDGE,"E419.filletArc");
            var Q280;
            Q280=sQuery(id+"F1.wireOp",EDGE,"E410");
            var Q281;
            Q281=sQuery(id+"F1.wireOp",EDGE,"E428.filletArc");
            var Q282;
            Q282=sQuery(id+"F1.wireOp",EDGE,"E555");
            var Q283;
            Q283=sQuery(id+"F1.wireOp",EDGE,"E563.filletArc");
            var Q284;
            Q284=sQuery(id+"F1.wireOp",EDGE,"E554");
            var Q285;
            Q285=sQuery(id+"F1.wireOp",EDGE,"E584.filletArc");
            var Q286;
            Q286=sQuery(id+"F1.wireOp",EDGE,"E1023");
            var Q287;
            Q287=sQuery(id+"F1.wireOp",EDGE,"E1031.filletArc");
            var Q288;
            Q288=sQuery(id+"F1.wireOp",EDGE,"E1022");
            var Q289;
            Q289=sQuery(id+"F1.wireOp",EDGE,"E1030.filletArc");
            var Q290;
            Q290=sQuery(id+"F1.wireOp",EDGE,"E1021");
            var Q291;
            Q291=sQuery(id+"F1.wireOp",EDGE,"E1029.filletArc");
            var Q292;
            Q292=sQuery(id+"F1.wireOp",EDGE,"E1020");
            var Q293;
            Q293=sQuery(id+"F1.wireOp",EDGE,"E1028.filletArc");
            var Q294;
            Q294=sQuery(id+"F1.wireOp",EDGE,"E1010");
            var Q295;
            Q295=sQuery(id+"F1.wireOp",EDGE,"E1019.filletArc");
            var Q296;
            Q296=sQuery(id+"F1.wireOp",EDGE,"E552");
            var Q297;
            Q297=sQuery(id+"F1.wireOp",EDGE,"E560.filletArc");
            var Q298;
            Q298=sQuery(id+"F1.wireOp",EDGE,"E566");
            var Q299;
            Q299=sQuery(id+"F1.wireOp",EDGE,"E575.filletArc");
            var Q300;
            Q300=sQuery(id+"F1.wireOp",EDGE,"E408");
            var Q301;
            Q301=sQuery(id+"F1.wireOp",EDGE,"E416.filletArc");
            var Q302;
            Q302=sQuery(id+"F1.wireOp",EDGE,"E398");
            var Q303;
            Q303=sQuery(id+"F1.wireOp",EDGE,"E407.filletArc");
            var Q304;
            Q304=sQuery(id+"F1.wireOp",EDGE,"E144");
            var Q305;
            Q305=sQuery(id+"F1.wireOp",EDGE,"E152.filletArc");
            var Q306;
            Q306=sQuery(id+"F1.wireOp",EDGE,"E149");
            var Q307;
            Q307=sQuery(id+"F1.wireOp",EDGE,"E119.filletArc");
            var Q308;
            Q308=sQuery(id+"F1.wireOp",EDGE,"E36");
            var Q309;
            Q309=sQuery(id+"F1.wireOp",EDGE,"E114.filletArc");
            var Q310;
            Q310=sQuery(id+"F1.wireOp",EDGE,"E121");
            var Q311;
            Q311=sQuery(id+"F1.wireOp",EDGE,"E129.filletArc");
            var Q312;
            Q312=sQuery(id+"F1.wireOp",EDGE,"E120");
            var Q313;
            Q313=sQuery(id+"F1.wireOp",EDGE,"E378.filletArc");
            var Q314;
            Q314=sQuery(id+"F1.wireOp",EDGE,"E361");
            var Q315;
            Q315=sQuery(id+"F1.wireOp",EDGE,"E369.filletArc");
            var Q316;
            Q316=sQuery(id+"F1.wireOp",EDGE,"E507");
            var Q317;
            Q317=sQuery(id+"F1.wireOp",EDGE,"E510.filletArc");
            var Q318;
            Q318=sQuery(id+"F1.wireOp",EDGE,"E508");
            var Q319;
            Q319=sQuery(id+"F1.wireOp",EDGE,"E501.filletArc");
            var Q320;
            Q320=sQuery(id+"F1.wireOp",EDGE,"E492");
            var Q321;
            Q321=sQuery(id+"F1.wireOp",EDGE,"E990.filletArc");
            var Q322;
            Q322=sQuery(id+"F1.wireOp",EDGE,"E925");
            var Q323;
            Q323=sQuery(id+"F1.wireOp",EDGE,"E991.filletArc");
            var Q324;
            Q324=sQuery(id+"F1.wireOp",EDGE,"E989");
            var Q325;
            Q325=sQuery(id+"F1.wireOp",EDGE,"E992.filletArc");
            var Q326;
            Q326=sQuery(id+"F1.wireOp",EDGE,"E984");
            var Q327;
            Q327=sQuery(id+"F1.wireOp",EDGE,"E993.filletArc");
            var Q328;
            Q328=sQuery(id+"F1.wireOp",EDGE,"E1048");
            var Q329;
            Q329=sQuery(id+"F1.wireOp",EDGE,"E1050.filletArc");
            var Q330;
            Q330=sQuery(id+"F1.wireOp",EDGE,"E504");
            var Q331;
            Q331=sQuery(id+"F1.wireOp",EDGE,"E513.filletArc");
            var Q332;
            Q332=sQuery(id+"F1.wireOp",EDGE,"E505");
            var Q333;
            Q333=sQuery(id+"F1.wireOp",EDGE,"E522.filletArc");
            var Q334;
            Q334=sQuery(id+"F1.wireOp",EDGE,"E519");
            var Q335;
            Q335=sQuery(id+"F1.wireOp",EDGE,"E381.filletArc");
            var Q336;
            Q336=sQuery(id+"F1.wireOp",EDGE,"E373");
            var Q337;
            Q337=sQuery(id+"F1.wireOp",EDGE,"E390.filletArc");
            var Q338;
            Q338=sQuery(id+"F1.wireOp",EDGE,"E108");
            var Q339;
            Q339=sQuery(id+"F1.wireOp",EDGE,"E395.filletArc");
            var Q340;
            Q340=sQuery(id+"F1.wireOp",EDGE,"E386");
            var Q341;
            Q341=sQuery(id+"F1.wireOp",EDGE,"E404.filletArc");
            var Q342;
            Q342=sQuery(id+"F1.wireOp",EDGE,"E396");
            var Q343;
            Q343=sQuery(id+"F1.wireOp",EDGE,"E551.filletArc");
            var Q344;
            Q344=sQuery(id+"F1.wireOp",EDGE,"E569");
            var Q345;
            Q345=sQuery(id+"F1.wireOp",EDGE,"E572.filletArc");
            var Q346;
            Q346=sQuery(id+"F1.wireOp",EDGE,"E564");
            var Q347;
            Q347=sQuery(id+"F1.wireOp",EDGE,"E1007.filletArc");
            var Q348;
            Q348=sQuery(id+"F1.wireOp",EDGE,"E998");
            var Q349;
            Q349=sQuery(id+"F1.wireOp",EDGE,"E1006.filletArc");
            var Q350;
            Q350=sQuery(id+"F1.wireOp",EDGE,"E997");
            var Q351;
            Q351=sQuery(id+"F1.wireOp",EDGE,"E1005.filletArc");
            var Q352;
            Q352=sQuery(id+"F1.wireOp",EDGE,"E996");
            var Q353;
            Q353=sQuery(id+"F1.wireOp",EDGE,"E1004.filletArc");
            var Q354;
            Q354=sQuery(id+"F1.wireOp",EDGE,"E1001");
            var Q355;
            Q355=sQuery(id+"F1.wireOp",EDGE,"E1079.filletArc");
            var Q356;
            Q356=sQuery(id+"F1.wireOp",EDGE,"E1071");
            var Q357;
            Q357=sQuery(id+"F1.wireOp",EDGE,"E548.filletArc");
            var Q358;
            Q358=sQuery(id+"F1.wireOp",EDGE,"E530");
            var Q359;
            Q359=sQuery(id+"F1.wireOp",EDGE,"E539.filletArc");
            var Q360;
            Q360=sQuery(id+"F1.wireOp",EDGE,"E531");
            var Q361;
            Q361=sQuery(id+"F1.wireOp",EDGE,"E534.filletArc");
            var Q362;
            Q362=sQuery(id+"F1.wireOp",EDGE,"E517");
            var Q363;
            Q363=sQuery(id+"F1.wireOp",EDGE,"E525.filletArc");
            var Q364;
            Q364=sQuery(id+"F1.wireOp",EDGE,"E516");
            var Q365;
            Q365=sQuery(id+"F1.wireOp",EDGE,"E1062.filletArc");
            var Q366;
            Q366=sQuery(id+"F1.wireOp",EDGE,"E1045");
            var Q367;
            Q367=sQuery(id+"F1.wireOp",EDGE,"E1063.filletArc");
            var Q368;
            Q368=sQuery(id+"F1.wireOp",EDGE,"E1061");
            var Q369;
            Q369=sQuery(id+"F1.wireOp",EDGE,"E1064.filletArc");
            var Q370;
            Q370=sQuery(id+"F1.wireOp",EDGE,"E1056");
            var Q371;
            Q371=sQuery(id+"F1.wireOp",EDGE,"E1065.filletArc");
            var Q372;
            Q372=sQuery(id+"F1.wireOp",EDGE,"E1084");
            var Q373;
            Q373=sQuery(id+"F1.wireOp",EDGE,"E1086.filletArc");
            var Q374;
            Q374=sQuery(id+"F1.wireOp",EDGE,"E528");
            var Q375;
            Q375=sQuery(id+"F1.wireOp",EDGE,"E1091.filletArc");
            var Q376;
            Q376=sQuery(id+"F1.wireOp",EDGE,"E1082");
            var Q377;
            Q377=sQuery(id+"F1.wireOp",EDGE,"E1081");
            var Q378;
            Q378=sQuery(id+"F1.wireOp",EDGE,"E1090.filletArc");
            var Q379;
            Q379=sQuery(id+"F1.wireOp",EDGE,"E1089.filletArc");
            var Q380;
            Q380=sQuery(id+"F1.wireOp",EDGE,"E1080");
            var Q381;
            Q381=sQuery(id+"F1.wireOp",EDGE,"E1088.filletArc");
            var Q382;
            Q382=sQuery(id+"F1.wireOp",EDGE,"E1085");
            sweep(context, id + "F4", {"profiles" : qUnion([Q0]), "path" : qUnion([Q1, Q2, Q3, Q4, Q5, Q6, Q7, Q8, Q9, Q10, Q11, Q12, Q13, Q14, Q15, Q16, Q17, Q18, Q19, Q20, Q21, Q22, Q23, Q24, Q25, Q26, Q27, Q28, Q29, Q30, Q31, Q32, Q33, Q34, Q35, Q36, Q37, Q38, Q39, Q40, Q41, Q42, Q43, Q44, Q45, Q46, Q47, Q48, Q49, Q50, Q51, Q52, Q53, Q54, Q55, Q56, Q57, Q58, Q59, Q60, Q61, Q62, Q63, Q64, Q65, Q66, Q67, Q68, Q69, Q70, Q71, Q72, Q73, Q74, Q75, Q76, Q77, Q78, Q79, Q80, Q81, Q82, Q83, Q84, Q85, Q86, Q87, Q88, Q89, Q90, Q91, Q92, Q93, Q94, Q95, Q96, Q97, Q98, Q99, Q100, Q101, Q102, Q103, Q104, Q105, Q106, Q107, Q108, Q109, Q110, Q111, Q112, Q113, Q114, Q115, Q116, Q117, Q118, Q119, Q120, Q121, Q122, Q123, Q124, Q125, Q126, Q127, Q128, Q129, Q130, Q131, Q132, Q133, Q134, Q135, Q136, Q137, Q138, Q139, Q140, Q141, Q142, Q143, Q144, Q145, Q146, Q147, Q148, Q149, Q150, Q151, Q152, Q153, Q154, Q155, Q156, Q157, Q158, Q159, Q160, Q161, Q162, Q163, Q164, Q165, Q166, Q167, Q168, Q169, Q170, Q171, Q172, Q173, Q174, Q175, Q176, Q177, Q178, Q179, Q180, Q181, Q182, Q183, Q184, Q185, Q186, Q187, Q188, Q189, Q190, Q191, Q192, Q193, Q194, Q195, Q196, Q197, Q198, Q199, Q200, Q201, Q202, Q203, Q204, Q205, Q206, Q207, Q208, Q209, Q210, Q211, Q212, Q213, Q214, Q215, Q216, Q217, Q218, Q219, Q220, Q221, Q222, Q223, Q224, Q225, Q226, Q227, Q228, Q229, Q230, Q231, Q232, Q233, Q234, Q235, Q236, Q237, Q238, Q239, Q240, Q241, Q242, Q243, Q244, Q245, Q246, Q247, Q248, Q249, Q250, Q251, Q252, Q253, Q254, Q255, Q256, Q257, Q258, Q259, Q260, Q261, Q262, Q263, Q264, Q265, Q266, Q267, Q268, Q269, Q270, Q271, Q272, Q273, Q274, Q275, Q276, Q277, Q278, Q279, Q280, Q281, Q282, Q283, Q284, Q285, Q286, Q287, Q288, Q289, Q290, Q291, Q292, Q293, Q294, Q295, Q296, Q297, Q298, Q299, Q300, Q301, Q302, Q303, Q304, Q305, Q306, Q307, Q308, Q309, Q310, Q311, Q312, Q313, Q314, Q315, Q316, Q317, Q318, Q319, Q320, Q321, Q322, Q323, Q324, Q325, Q326, Q327, Q328, Q329, Q330, Q331, Q332, Q333, Q334, Q335, Q336, Q337, Q338, Q339, Q340, Q341, Q342, Q343, Q344, Q345, Q346, Q347, Q348, Q349, Q350, Q351, Q352, Q353, Q354, Q355, Q356, Q357, Q358, Q359, Q360, Q361, Q362, Q363, Q364, Q365, Q366, Q367, Q368, Q369, Q370, Q371, Q372, Q373, Q374, Q375, Q376, Q377, Q378, Q379, Q380, Q381, Q382])});
        }
        {
            var Q0;
            Q0=sQuery(id+"F1.wireOp",EDGE,"E1093");
            var Q1;
            Q1=sQuery(id+"F1.wireOp",VERTEX,"E1093.end");
            cPlane(context, id + "F5", {"entities" : qUnion([Q0, Q1]), "cplaneType" : CPlaneType.LINE_POINT, "offset" : 25 * mm, "width" : 150 * mm, "height" : 150 * mm});
        }
        {
            var Q0;
            Q0=qCreatedBy(id+"F5.planeOp",FACE);
            var sketch = newSketch(context, id + "F6", { "sketchPlane" : qUnion([Q0])});
            skCircle(sketch, "E1095", {"center": v(4.1, 0.21) * mm, "radius": 0.2 * mm});
            skSolve(sketch);
        }
        {
            var Q0;
            Q0 = qSketchRegion(id + "F6", true);
            var Q1;
            Q1=sQuery(id+"F1.wireOp",EDGE,"E1093");
            var Q2;
            Q2=sQuery(id+"F1.wireOp",EDGE,"E977");
            var Q3;
            Q3=sQuery(id+"F1.wireOp",EDGE,"E980.filletArc");
            var Q4;
            Q4=sQuery(id+"F1.wireOp",EDGE,"E972");
            var Q5;
            Q5=sQuery(id+"F1.wireOp",EDGE,"E981.filletArc");
            var Q6;
            Q6=sQuery(id+"F1.wireOp",EDGE,"E928");
            var Q7;
            Q7=sQuery(id+"F1.wireOp",EDGE,"E930.filletArc");
            var Q8;
            Q8=sQuery(id+"F1.wireOp",EDGE,"E927");
            var Q9;
            Q9=sQuery(id+"F1.wireOp",EDGE,"E935.filletArc");
            var Q10;
            Q10=sQuery(id+"F1.wireOp",EDGE,"E926");
            var Q11;
            Q11=sQuery(id+"F1.wireOp",EDGE,"E934.filletArc");
            var Q12;
            Q12=sQuery(id+"F1.wireOp",EDGE,"E925");
            var Q13;
            Q13=sQuery(id+"F1.wireOp",EDGE,"E991.filletArc");
            var Q14;
            Q14=sQuery(id+"F1.wireOp",EDGE,"E989");
            var Q15;
            Q15=sQuery(id+"F1.wireOp",EDGE,"E992.filletArc");
            var Q16;
            Q16=sQuery(id+"F1.wireOp",EDGE,"E984");
            var Q17;
            Q17=sQuery(id+"F1.wireOp",EDGE,"E993.filletArc");
            var Q18;
            Q18=sQuery(id+"F1.wireOp",EDGE,"E1048");
            var Q19;
            Q19=sQuery(id+"F1.wireOp",EDGE,"E504");
            var Q20;
            Q20=sQuery(id+"F1.wireOp",EDGE,"E1055.filletArc");
            var Q21;
            Q21=sQuery(id+"F1.wireOp",EDGE,"E521");
            var Q22;
            Q22=sQuery(id+"F1.wireOp",EDGE,"E1045");
            var Q23;
            Q23=sQuery(id+"F1.wireOp",EDGE,"E1054.filletArc");
            var Q24;
            Q24=sQuery(id+"F1.wireOp",EDGE,"E1063.filletArc");
            var Q25;
            Q25=sQuery(id+"F1.wireOp",EDGE,"E1061");
            var Q26;
            Q26=sQuery(id+"F1.wireOp",EDGE,"E1064.filletArc");
            var Q27;
            Q27=sQuery(id+"F1.wireOp",EDGE,"E1056");
            var Q28;
            Q28=sQuery(id+"F1.wireOp",EDGE,"E1065.filletArc");
            var Q29;
            Q29=sQuery(id+"F1.wireOp",EDGE,"E1084");
            var Q30;
            Q30=sQuery(id+"F1.wireOp",EDGE,"E1086.filletArc");
            var Q31;
            Q31=sQuery(id+"F1.wireOp",EDGE,"E528");
            var Q32;
            Q32=sQuery(id+"F1.wireOp",EDGE,"E1091.filletArc");
            var Q33;
            Q33=sQuery(id+"F1.wireOp",EDGE,"E1082");
            var Q34;
            Q34=sQuery(id+"F1.wireOp",EDGE,"E1076.filletArc");
            var Q35;
            Q35=sQuery(id+"F1.wireOp",EDGE,"E1068");
            var Q36;
            Q36=sQuery(id+"F1.wireOp",EDGE,"E1077.filletArc");
            var Q37;
            Q37=sQuery(id+"F1.wireOp",EDGE,"E1069");
            var Q38;
            Q38=sQuery(id+"F1.wireOp",EDGE,"E1078.filletArc");
            var Q39;
            Q39=sQuery(id+"F1.wireOp",EDGE,"E1001");
            var Q40;
            Q40=sQuery(id+"F1.wireOp",EDGE,"E1003.filletArc");
            var Q41;
            Q41=sQuery(id+"F1.wireOp",EDGE,"E1000");
            var Q42;
            Q42=sQuery(id+"F1.wireOp",EDGE,"E1007.filletArc");
            var Q43;
            Q43=sQuery(id+"F1.wireOp",EDGE,"E998");
            var Q44;
            Q44=sQuery(id+"F1.wireOp",EDGE,"E1016.filletArc");
            var Q45;
            Q45=sQuery(id+"F1.wireOp",EDGE,"E1008");
            var Q46;
            Q46=sQuery(id+"F1.wireOp",EDGE,"E1050.filletArc");
            var Q47;
            Q47=sQuery(id+"F1.wireOp",EDGE,"E1017.filletArc");
            var Q48;
            Q48=sQuery(id+"F1.wireOp",EDGE,"E1018.filletArc");
            var Q49;
            Q49=sQuery(id+"F1.wireOp",EDGE,"E1010");
            var Q50;
            Q50=sQuery(id+"F1.wireOp",EDGE,"E1027.filletArc");
            var Q51;
            Q51=sQuery(id+"F1.wireOp",EDGE,"E553");
            var Q52;
            Q52=sQuery(id+"F1.wireOp",EDGE,"E1026.filletArc");
            var Q53;
            Q53=sQuery(id+"F1.wireOp",EDGE,"E1023");
            var Q54;
            Q54=sQuery(id+"F1.wireOp",EDGE,"E1031.filletArc");
            var Q55;
            Q55=sQuery(id+"F1.wireOp",EDGE,"E1022");
            var Q56;
            Q56=sQuery(id+"F1.wireOp",EDGE,"E1040.filletArc");
            var Q57;
            Q57=sQuery(id+"F1.wireOp",EDGE,"E1032");
            var Q58;
            Q58=sQuery(id+"F1.wireOp",EDGE,"E1033");
            var Q59;
            Q59=sQuery(id+"F1.wireOp",EDGE,"E1041.filletArc");
            var Q60;
            Q60=sQuery(id+"F1.wireOp",EDGE,"E1042.filletArc");
            var Q61;
            Q61=sQuery(id+"F1.wireOp",EDGE,"E1034");
            var Q62;
            Q62=sQuery(id+"F1.wireOp",EDGE,"E1009");
            var Q63;
            Q63=sQuery(id+"F1.wireOp",EDGE,"E1043.filletArc");
            var Q64;
            Q64=sQuery(id+"F1.wireOp",EDGE,"E816");
            var Q65;
            Q65=sQuery(id+"F1.wireOp",EDGE,"E824.filletArc");
            var Q66;
            Q66=sQuery(id+"F1.wireOp",EDGE,"E578");
            var Q67;
            Q67=sQuery(id+"F1.wireOp",EDGE,"E587.filletArc");
            var Q68;
            Q68=sQuery(id+"F1.wireOp",EDGE,"E588");
            var Q69;
            Q69=sQuery(id+"F1.wireOp",EDGE,"E582.filletArc");
            var Q70;
            Q70=sQuery(id+"F1.wireOp",EDGE,"E580");
            var Q71;
            Q71=sQuery(id+"F1.wireOp",EDGE,"E429.filletArc");
            var Q72;
            Q72=sQuery(id+"F1.wireOp",EDGE,"E555");
            var Q73;
            Q73=sQuery(id+"F1.wireOp",EDGE,"E558.filletArc");
            var Q74;
            Q74=sQuery(id+"F1.wireOp",EDGE,"E556");
            var Q75;
            Q75=sQuery(id+"F1.wireOp",EDGE,"E564");
            var Q76;
            Q76=sQuery(id+"F1.wireOp",EDGE,"E568");
            var Q77;
            Q77=sQuery(id+"F1.wireOp",EDGE,"E570.filletArc");
            var Q78;
            Q78=sQuery(id+"F1.wireOp",EDGE,"E408");
            var Q79;
            Q79=sQuery(id+"F1.wireOp",EDGE,"E417.filletArc");
            var Q80;
            Q80=sQuery(id+"F1.wireOp",EDGE,"E1002.filletArc");
            var Q81;
            Q81=sQuery(id+"F1.wireOp",EDGE,"E405.filletArc");
            var Q82;
            Q82=sQuery(id+"F1.wireOp",EDGE,"E396");
            var Q83;
            Q83=sQuery(id+"F1.wireOp",EDGE,"E546.filletArc");
            var Q84;
            Q84=sQuery(id+"F1.wireOp",EDGE,"E385");
            var Q85;
            Q85=sQuery(id+"F1.wireOp",EDGE,"E393.filletArc");
            var Q86;
            Q86=sQuery(id+"F1.wireOp",EDGE,"E531");
            var Q87;
            Q87=sQuery(id+"F1.wireOp",EDGE,"E392.filletArc");
            var Q88;
            Q88=sQuery(id+"F1.wireOp",EDGE,"E518");
            var Q89;
            Q89=sQuery(id+"F1.wireOp",EDGE,"E527.filletArc");
            var Q90;
            Q90=sQuery(id+"F1.wireOp",EDGE,"E519");
            var Q91;
            Q91=sQuery(id+"F1.wireOp",EDGE,"E380.filletArc");
            var Q92;
            Q92=sQuery(id+"F1.wireOp",EDGE,"E506");
            var Q93;
            Q93=sQuery(id+"F1.wireOp",EDGE,"E515.filletArc");
            var Q94;
            Q94=sQuery(id+"F1.wireOp",EDGE,"E507");
            var Q95;
            Q95=sQuery(id+"F1.wireOp",EDGE,"E368.filletArc");
            var Q96;
            Q96=sQuery(id+"F1.wireOp",EDGE,"E494");
            var Q97;
            Q97=sQuery(id+"F1.wireOp",EDGE,"E503.filletArc");
            var Q98;
            Q98=sQuery(id+"F1.wireOp",EDGE,"E348");
            var Q99;
            Q99=sQuery(id+"F1.wireOp",EDGE,"E356.filletArc");
            var Q100;
            Q100=sQuery(id+"F1.wireOp",EDGE,"E468");
            var Q101;
            Q101=sQuery(id+"F1.wireOp",EDGE,"E491.filletArc");
            var Q102;
            Q102=sQuery(id+"F1.wireOp",EDGE,"E482");
            var Q103;
            Q103=sQuery(id+"F1.wireOp",EDGE,"E486.filletArc");
            var Q104;
            Q104=sQuery(id+"F1.wireOp",EDGE,"E733");
            var Q105;
            Q105=sQuery(id+"F1.wireOp",EDGE,"E741.filletArc");
            var Q106;
            Q106=sQuery(id+"F1.wireOp",EDGE,"E975");
            var Q107;
            Q107=sQuery(id+"F1.wireOp",EDGE,"E740.filletArc");
            var Q108;
            Q108=sQuery(id+"F1.wireOp",EDGE,"E739.filletArc");
            var Q109;
            Q109=sQuery(id+"F1.wireOp",EDGE,"E737");
            var Q110;
            Q110=sQuery(id+"F1.wireOp",EDGE,"E736");
            var Q111;
            Q111=sQuery(id+"F1.wireOp",EDGE,"E738.filletArc");
            var Q112;
            Q112=sQuery(id+"F1.wireOp",EDGE,"E735");
            var Q113;
            Q113=sQuery(id+"F1.wireOp",EDGE,"E753.filletArc");
            var Q114;
            Q114=sQuery(id+"F1.wireOp",EDGE,"E472");
            var Q115;
            Q115=sQuery(id+"F1.wireOp",EDGE,"E474.filletArc");
            var Q116;
            Q116=sQuery(id+"F1.wireOp",EDGE,"E479.filletArc");
            var Q117;
            Q117=sQuery(id+"F1.wireOp",EDGE,"E456");
            var Q118;
            Q118=sQuery(id+"F1.wireOp",EDGE,"E470");
            var Q119;
            Q119=sQuery(id+"F1.wireOp",EDGE,"E344.filletArc");
            var Q120;
            Q120=sQuery(id+"F1.wireOp",EDGE,"E336");
            var Q121;
            Q121=sQuery(id+"F1.wireOp",EDGE,"E359.filletArc");
            var Q122;
            Q122=sQuery(id+"F1.wireOp",EDGE,"E101");
            var Q123;
            Q123=sQuery(id+"F1.wireOp",EDGE,"E104.filletArc");
            var Q124;
            Q124=sQuery(id+"F1.wireOp",EDGE,"E363");
            var Q125;
            Q125=sQuery(id+"F1.wireOp",EDGE,"E371.filletArc");
            var Q126;
            Q126=sQuery(id+"F1.wireOp",EDGE,"E362");
            var Q127;
            Q127=sQuery(id+"F1.wireOp",EDGE,"E128.filletArc");
            var Q128;
            Q128=sQuery(id+"F1.wireOp",EDGE,"E120");
            var Q129;
            Q129=sQuery(id+"F1.wireOp",EDGE,"E383.filletArc");
            var Q130;
            Q130=sQuery(id+"F1.wireOp",EDGE,"E374");
            var Q131;
            Q131=sQuery(id+"F1.wireOp",EDGE,"E116.filletArc");
            var Q132;
            Q132=sQuery(id+"F1.wireOp",EDGE,"E108");
            var Q133;
            Q133=sQuery(id+"F1.wireOp",EDGE,"E117.filletArc");
            var Q134;
            Q134=sQuery(id+"F1.wireOp",EDGE,"E400");
            var Q135;
            Q135=sQuery(id+"F1.wireOp",EDGE,"E402.filletArc");
            var Q136;
            Q136=sQuery(id+"F1.wireOp",EDGE,"E144");
            var Q137;
            Q137=sQuery(id+"F1.wireOp",EDGE,"E153.filletArc");
            var Q138;
            Q138=sQuery(id+"F1.wireOp",EDGE,"E156");
            var Q139;
            Q139=sQuery(id+"F1.wireOp",EDGE,"E414.filletArc");
            var Q140;
            Q140=sQuery(id+"F1.wireOp",EDGE,"E412");
            var Q141;
            Q141=sQuery(id+"F1.wireOp",EDGE,"E165.filletArc");
            var Q142;
            Q142=sQuery(id+"F1.wireOp",EDGE,"E424");
            var Q143;
            Q143=sQuery(id+"F1.wireOp",EDGE,"E426.filletArc");
            var Q144;
            Q144=sQuery(id+"F1.wireOp",EDGE,"E423");
            var Q145;
            Q145=sQuery(id+"F1.wireOp",EDGE,"E237.filletArc");
            var Q146;
            Q146=sQuery(id+"F1.wireOp",EDGE,"E229");
            var Q147;
            Q147=sQuery(id+"F1.wireOp",EDGE,"E594.filletArc");
            var Q148;
            Q148=sQuery(id+"F1.wireOp",EDGE,"E600");
            var Q149;
            Q149=sQuery(id+"F1.wireOp",EDGE,"E599.filletArc");
            var Q150;
            Q150=sQuery(id+"F1.wireOp",EDGE,"E809");
            var Q151;
            Q151=sQuery(id+"F1.wireOp",EDGE,"E812.filletArc");
            var Q152;
            Q152=sQuery(id+"F1.wireOp",EDGE,"E804");
            var Q153;
            Q153=sQuery(id+"F1.wireOp",EDGE,"E813.filletArc");
            var Q154;
            Q154=sQuery(id+"F1.wireOp",EDGE,"E805");
            var Q155;
            Q155=sQuery(id+"F1.wireOp",EDGE,"E814.filletArc");
            var Q156;
            Q156=sQuery(id+"F1.wireOp",EDGE,"E806");
            var Q157;
            Q157=sQuery(id+"F1.wireOp",EDGE,"E815.filletArc");
            var Q158;
            Q158=sQuery(id+"F1.wireOp",EDGE,"E780");
            var Q159;
            Q159=sQuery(id+"F1.wireOp",EDGE,"E788.filletArc");
            var Q160;
            Q160=sQuery(id+"F1.wireOp",EDGE,"E602");
            var Q161;
            Q161=sQuery(id+"F1.wireOp",EDGE,"E611.filletArc");
            var Q162;
            Q162=sQuery(id+"F1.wireOp",EDGE,"E603");
            var Q163;
            Q163=sQuery(id+"F1.wireOp",EDGE,"E606.filletArc");
            var Q164;
            Q164=sQuery(id+"F1.wireOp",EDGE,"E604");
            var Q165;
            Q165=sQuery(id+"F1.wireOp",EDGE,"E249.filletArc");
            var Q166;
            Q166=sQuery(id+"F1.wireOp",EDGE,"E231");
            var Q167;
            Q167=sQuery(id+"F1.wireOp",EDGE,"E234.filletArc");
            var Q168;
            Q168=sQuery(id+"F1.wireOp",EDGE,"E141.filletArc");
            var Q169;
            Q169=sQuery(id+"F1.wireOp",EDGE,"E232");
            var Q170;
            Q170=sQuery(id+"F1.wireOp",EDGE,"E132");
            var Q171;
            Q171=sQuery(id+"F1.wireOp",EDGE,"E162.filletArc");
            var Q172;
            Q172=sQuery(id+"F1.wireOp",EDGE,"E49");
            var Q173;
            Q173=sQuery(id+"F1.wireOp",EDGE,"E57.filletArc");
            var Q174;
            Q174=sQuery(id+"F1.wireOp",EDGE,"E147");
            var Q175;
            Q175=sQuery(id+"F1.wireOp",EDGE,"E150.filletArc");
            var Q176;
            Q176=sQuery(id+"F1.wireOp",EDGE,"E37");
            var Q177;
            Q177=sQuery(id+"F1.wireOp",EDGE,"E45.filletArc");
            var Q178;
            Q178=sQuery(id+"F1.wireOp",EDGE,"E36");
            var Q179;
            Q179=sQuery(id+"F1.wireOp",EDGE,"E44.filletArc");
            var Q180;
            Q180=sQuery(id+"F1.wireOp",EDGE,"E122");
            var Q181;
            Q181=sQuery(id+"F1.wireOp",EDGE,"E131.filletArc");
            var Q182;
            Q182=sQuery(id+"F1.wireOp",EDGE,"E123");
            var Q183;
            Q183=sQuery(id+"F1.wireOp",EDGE,"E32.filletArc");
            var Q184;
            Q184=sQuery(id+"F1.wireOp",EDGE,"E98");
            var Q185;
            Q185=sQuery(id+"F1.wireOp",EDGE,"E107.filletArc");
            var Q186;
            Q186=sQuery(id+"F1.wireOp",EDGE,"E84");
            var Q187;
            Q187=sQuery(id+"F1.wireOp",EDGE,"E92.filletArc");
            var Q188;
            Q188=sQuery(id+"F1.wireOp",EDGE,"E89");
            var Q189;
            Q189=sQuery(id+"F1.wireOp",EDGE,"E347.filletArc");
            var Q190;
            Q190=sQuery(id+"F1.wireOp",EDGE,"E324");
            var Q191;
            Q191=sQuery(id+"F1.wireOp",EDGE,"E332.filletArc");
            var Q192;
            Q192=sQuery(id+"F1.wireOp",EDGE,"E458");
            var Q193;
            Q193=sQuery(id+"F1.wireOp",EDGE,"E467.filletArc");
            var Q194;
            Q194=sQuery(id+"F1.wireOp",EDGE,"E444");
            var Q195;
            Q195=sQuery(id+"F1.wireOp",EDGE,"E462.filletArc");
            var Q196;
            Q196=sQuery(id+"F1.wireOp",EDGE,"E460");
            var Q197;
            Q197=sQuery(id+"F1.wireOp",EDGE,"E765.filletArc");
            var Q198;
            Q198=sQuery(id+"F1.wireOp",EDGE,"E747");
            var Q199;
            Q199=sQuery(id+"F1.wireOp",EDGE,"E764.filletArc");
            var Q200;
            Q200=sQuery(id+"F1.wireOp",EDGE,"E761");
            var Q201;
            Q201=sQuery(id+"F1.wireOp",EDGE,"E763.filletArc");
            var Q202;
            Q202=sQuery(id+"F1.wireOp",EDGE,"E760");
            var Q203;
            Q203=sQuery(id+"F1.wireOp",EDGE,"E762.filletArc");
            var Q204;
            Q204=sQuery(id+"F1.wireOp",EDGE,"E768");
            var Q205;
            Q205=sQuery(id+"F1.wireOp",EDGE,"E777.filletArc");
            var Q206;
            Q206=sQuery(id+"F1.wireOp",EDGE,"E448");
            var Q207;
            Q207=sQuery(id+"F1.wireOp",EDGE,"E450.filletArc");
            var Q208;
            Q208=sQuery(id+"F1.wireOp",EDGE,"E696");
            var Q209;
            Q209=sQuery(id+"F1.wireOp",EDGE,"E455.filletArc");
            var Q210;
            Q210=sQuery(id+"F1.wireOp",EDGE,"E446");
            var Q211;
            Q211=sQuery(id+"F1.wireOp",EDGE,"E320.filletArc");
            var Q212;
            Q212=sQuery(id+"F1.wireOp",EDGE,"E312");
            var Q213;
            Q213=sQuery(id+"F1.wireOp",EDGE,"E335.filletArc");
            var Q214;
            Q214=sQuery(id+"F1.wireOp",EDGE,"E326");
            var Q215;
            Q215=sQuery(id+"F1.wireOp",EDGE,"E224.filletArc");
            var Q216;
            Q216=sQuery(id+"F1.wireOp",EDGE,"E216");
            var Q217;
            Q217=sQuery(id+"F1.wireOp",EDGE,"E95.filletArc");
            var Q218;
            Q218=sQuery(id+"F1.wireOp",EDGE,"E86");
            var Q219;
            Q219=sQuery(id+"F1.wireOp",EDGE,"E20.filletArc");
            var Q220;
            Q220=sQuery(id+"F1.wireOp",EDGE,"E27");
            var Q221;
            Q221=sQuery(id+"F1.wireOp",EDGE,"E26");
            var Q222;
            Q222=sQuery(id+"F1.wireOp",EDGE,"E35.filletArc");
            var Q223;
            Q223=sQuery(id+"F1.wireOp",EDGE,"E8.filletArc");
            var Q224;
            Q224=sQuery(id+"F1.wireOp",EDGE,"E39");
            var Q225;
            Q225=sQuery(id+"F1.wireOp",EDGE,"E9.filletArc");
            var Q226;
            Q226=sQuery(id+"F1.wireOp",EDGE,"E52");
            var Q227;
            Q227=sQuery(id+"F1.wireOp",EDGE,"E54.filletArc");
            var Q228;
            Q228=sQuery(id+"F1.wireOp",EDGE,"E60");
            var Q229;
            Q229=sQuery(id+"F1.wireOp",EDGE,"E69.filletArc");
            var Q230;
            Q230=sQuery(id+"F1.wireOp",EDGE,"E136");
            var Q231;
            Q231=sQuery(id+"F1.wireOp",EDGE,"E138.filletArc");
            var Q232;
            Q232=sQuery(id+"F1.wireOp",EDGE,"E168");
            var Q233;
            Q233=sQuery(id+"F1.wireOp",EDGE,"E177.filletArc");
            var Q234;
            Q234=sQuery(id+"F1.wireOp",EDGE,"E169");
            var Q235;
            Q235=sQuery(id+"F1.wireOp",EDGE,"E246.filletArc");
            var Q236;
            Q236=sQuery(id+"F1.wireOp",EDGE,"E252");
            var Q237;
            Q237=sQuery(id+"F1.wireOp",EDGE,"E261.filletArc");
            var Q238;
            Q238=sQuery(id+"F1.wireOp",EDGE,"E712");
            var Q239;
            Q239=sQuery(id+"F1.wireOp",EDGE,"E714.filletArc");
            var Q240;
            Q240=sQuery(id+"F1.wireOp",EDGE,"E720");
            var Q241;
            Q241=sQuery(id+"F1.wireOp",EDGE,"E729.filletArc");
            var Q242;
            Q242=sQuery(id+"F1.wireOp",EDGE,"E796");
            var Q243;
            Q243=sQuery(id+"F1.wireOp",EDGE,"E798.filletArc");
            var Q244;
            Q244=sQuery(id+"F1.wireOp",EDGE,"E828");
            var Q245;
            Q245=sQuery(id+"F1.wireOp",EDGE,"E837.filletArc");
            var Q246;
            Q246=sQuery(id+"F1.wireOp",EDGE,"E829");
            var Q247;
            Q247=sQuery(id+"F1.wireOp",EDGE,"E838.filletArc");
            var Q248;
            Q248=sQuery(id+"F1.wireOp",EDGE,"E830");
            var Q249;
            Q249=sQuery(id+"F1.wireOp",EDGE,"E839.filletArc");
            var Q250;
            Q250=sQuery(id+"F1.wireOp",EDGE,"E831");
            var Q251;
            Q251=sQuery(id+"F1.wireOp",EDGE,"E834.filletArc");
            var Q252;
            Q252=sQuery(id+"F1.wireOp",EDGE,"E832");
            var Q253;
            Q253=sQuery(id+"F1.wireOp",EDGE,"E849.filletArc");
            var Q254;
            Q254=sQuery(id+"F1.wireOp",EDGE,"E840");
            var Q255;
            Q255=sQuery(id+"F1.wireOp",EDGE,"E726.filletArc");
            var Q256;
            Q256=sQuery(id+"F1.wireOp",EDGE,"E724");
            var Q257;
            Q257=sQuery(id+"F1.wireOp",EDGE,"E633.filletArc");
            var Q258;
            Q258=sQuery(id+"F1.wireOp",EDGE,"E624");
            var Q259;
            Q259=sQuery(id+"F1.wireOp",EDGE,"E258.filletArc");
            var Q260;
            Q260=sQuery(id+"F1.wireOp",EDGE,"E265");
            var Q261;
            Q261=sQuery(id+"F1.wireOp",EDGE,"E273.filletArc");
            var Q262;
            Q262=sQuery(id+"F1.wireOp",EDGE,"E171");
            var Q263;
            Q263=sQuery(id+"F1.wireOp",EDGE,"E174.filletArc");
            var Q264;
            Q264=sQuery(id+"F1.wireOp",EDGE,"E172");
            var Q265;
            Q265=sQuery(id+"F1.wireOp",EDGE,"E201.filletArc");
            var Q266;
            Q266=sQuery(id+"F1.wireOp",EDGE,"E192");
            var Q267;
            Q267=sQuery(id+"F1.wireOp",EDGE,"E66.filletArc");
            var Q268;
            Q268=sQuery(id+"F1.wireOp",EDGE,"E73");
            var Q269;
            Q269=sQuery(id+"F1.wireOp",EDGE,"E81.filletArc");
            var Q270;
            Q270=sQuery(id+"F1.wireOp",EDGE,"E72");
            var Q271;
            Q271=sQuery(id+"F1.wireOp",EDGE,"E80.filletArc");
            var Q272;
            Q272=sQuery(id+"F1.wireOp",EDGE,"E77");
            var Q273;
            Q273=sQuery(id+"F1.wireOp",EDGE,"E23.filletArc");
            var Q274;
            Q274=sQuery(id+"F1.wireOp",EDGE,"E180");
            var Q275;
            Q275=sQuery(id+"F1.wireOp",EDGE,"E188.filletArc");
            var Q276;
            Q276=sQuery(id+"F1.wireOp",EDGE,"E218");
            var Q277;
            Q277=sQuery(id+"F1.wireOp",EDGE,"E227.filletArc");
            var Q278;
            Q278=sQuery(id+"F1.wireOp",EDGE,"E300");
            var Q279;
            Q279=sQuery(id+"F1.wireOp",EDGE,"E308.filletArc");
            var Q280;
            Q280=sQuery(id+"F1.wireOp",EDGE,"E314");
            var Q281;
            Q281=sQuery(id+"F1.wireOp",EDGE,"E323.filletArc");
            var Q282;
            Q282=sQuery(id+"F1.wireOp",EDGE,"E315");
            var Q283;
            Q283=sQuery(id+"F1.wireOp",EDGE,"E692.filletArc");
            var Q284;
            Q284=sQuery(id+"F1.wireOp",EDGE,"E698");
            var Q285;
            Q285=sQuery(id+"F1.wireOp",EDGE,"E707.filletArc");
            var Q286;
            Q286=sQuery(id+"F1.wireOp",EDGE,"E699");
            var Q287;
            Q287=sQuery(id+"F1.wireOp",EDGE,"E938");
            var Q288;
            Q288=sQuery(id+"F1.wireOp",EDGE,"E955.filletArc");
            var Q289;
            Q289=sQuery(id+"F1.wireOp",EDGE,"E952");
            var Q290;
            Q290=sQuery(id+"F1.wireOp",EDGE,"E954.filletArc");
            var Q291;
            Q291=sQuery(id+"F1.wireOp",EDGE,"E951");
            var Q292;
            Q292=sQuery(id+"F1.wireOp",EDGE,"E959.filletArc");
            var Q293;
            Q293=sQuery(id+"F1.wireOp",EDGE,"E950");
            var Q294;
            Q294=sQuery(id+"F1.wireOp",EDGE,"E920.filletArc");
            var Q295;
            Q295=sQuery(id+"F1.wireOp",EDGE,"E912");
            var Q296;
            Q296=sQuery(id+"F1.wireOp",EDGE,"E695.filletArc");
            var Q297;
            Q297=sQuery(id+"F1.wireOp",EDGE,"E686");
            var Q298;
            Q298=sQuery(id+"F1.wireOp",EDGE,"E680.filletArc");
            var Q299;
            Q299=sQuery(id+"F1.wireOp",EDGE,"E672");
            var Q300;
            Q300=sQuery(id+"F1.wireOp",EDGE,"E311.filletArc");
            var Q301;
            Q301=sQuery(id+"F1.wireOp",EDGE,"E293");
            var Q302;
            Q302=sQuery(id+"F1.wireOp",EDGE,"E296.filletArc");
            var Q303;
            Q303=sQuery(id+"F1.wireOp",EDGE,"E183");
            var Q304;
            Q304=sQuery(id+"F1.wireOp",EDGE,"E191.filletArc");
            var Q305;
            Q305=sQuery(id+"F1.wireOp",EDGE,"E182");
            var Q306;
            Q306=sQuery(id+"F1.wireOp",EDGE,"E212.filletArc");
            var Q307;
            Q307=sQuery(id+"F1.wireOp",EDGE,"E204");
            var Q308;
            Q308=sQuery(id+"F1.wireOp",EDGE,"E213.filletArc");
            var Q309;
            Q309=sQuery(id+"F1.wireOp",EDGE,"E196");
            var Q310;
            Q310=sQuery(id+"F1.wireOp",EDGE,"E198.filletArc");
            var Q311;
            Q311=sQuery(id+"F1.wireOp",EDGE,"E276");
            var Q312;
            Q312=sQuery(id+"F1.wireOp",EDGE,"E285.filletArc");
            var Q313;
            Q313=sQuery(id+"F1.wireOp",EDGE,"E270.filletArc");
            var Q314;
            Q314=sQuery(id+"F1.wireOp",EDGE,"E268");
            var Q315;
            Q315=sQuery(id+"F1.wireOp",EDGE,"E267");
            var Q316;
            Q316=sQuery(id+"F1.wireOp",EDGE,"E621.filletArc");
            var Q317;
            Q317=sQuery(id+"F1.wireOp",EDGE,"E613");
            var Q318;
            Q318=sQuery(id+"F1.wireOp",EDGE,"E630.filletArc");
            var Q319;
            Q319=sQuery(id+"F1.wireOp",EDGE,"E852");
            var Q320;
            Q320=sQuery(id+"F1.wireOp",EDGE,"E861.filletArc");
            var Q321;
            Q321=sQuery(id+"F1.wireOp",EDGE,"E844");
            var Q322;
            Q322=sQuery(id+"F1.wireOp",EDGE,"E862.filletArc");
            var Q323;
            Q323=sQuery(id+"F1.wireOp",EDGE,"E854");
            var Q324;
            Q324=sQuery(id+"F1.wireOp",EDGE,"E863.filletArc");
            var Q325;
            Q325=sQuery(id+"F1.wireOp",EDGE,"E855");
            var Q326;
            Q326=sQuery(id+"F1.wireOp",EDGE,"E858.filletArc");
            var Q327;
            Q327=sQuery(id+"F1.wireOp",EDGE,"E856");
            var Q328;
            Q328=sQuery(id+"F1.wireOp",EDGE,"E873.filletArc");
            var Q329;
            Q329=sQuery(id+"F1.wireOp",EDGE,"E864");
            var Q330;
            Q330=sQuery(id+"F1.wireOp",EDGE,"E618.filletArc");
            var Q331;
            Q331=sQuery(id+"F1.wireOp",EDGE,"E637");
            var Q332;
            Q332=sQuery(id+"F1.wireOp",EDGE,"E645.filletArc");
            var Q333;
            Q333=sQuery(id+"F1.wireOp",EDGE,"E636");
            var Q334;
            Q334=sQuery(id+"F1.wireOp",EDGE,"E282.filletArc");
            var Q335;
            Q335=sQuery(id+"F1.wireOp",EDGE,"E280");
            var Q336;
            Q336=sQuery(id+"F1.wireOp",EDGE,"E441.filletArc");
            var Q337;
            Q337=sQuery(id+"F1.wireOp",EDGE,"E432");
            var Q338;
            Q338=sQuery(id+"F1.wireOp",EDGE,"E440.filletArc");
            var Q339;
            Q339=sQuery(id+"F1.wireOp",EDGE,"E437");
            var Q340;
            Q340=sQuery(id+"F1.wireOp",EDGE,"E299.filletArc");
            var Q341;
            Q341=sQuery(id+"F1.wireOp",EDGE,"E291");
            var Q342;
            Q342=sQuery(id+"F1.wireOp",EDGE,"E668.filletArc");
            var Q343;
            Q343=sQuery(id+"F1.wireOp",EDGE,"E665");
            var Q344;
            Q344=sQuery(id+"F1.wireOp",EDGE,"E683.filletArc");
            var Q345;
            Q345=sQuery(id+"F1.wireOp",EDGE,"E960");
            var Q346;
            Q346=sQuery(id+"F1.wireOp",EDGE,"E965");
            var Q347;
            Q347=sQuery(id+"F1.wireOp",EDGE,"E968.filletArc");
            var Q348;
            Q348=sQuery(id+"F1.wireOp",EDGE,"E967.filletArc");
            var Q349;
            Q349=sQuery(id+"F1.wireOp",EDGE,"E964");
            var Q350;
            Q350=sQuery(id+"F1.wireOp",EDGE,"E966.filletArc");
            var Q351;
            Q351=sQuery(id+"F1.wireOp",EDGE,"E963");
            var Q352;
            Q352=sQuery(id+"F1.wireOp",EDGE,"E971.filletArc");
            var Q353;
            Q353=sQuery(id+"F1.wireOp",EDGE,"E893");
            var Q354;
            Q354=sQuery(id+"F1.wireOp",EDGE,"E896.filletArc");
            var Q355;
            Q355=sQuery(id+"F1.wireOp",EDGE,"E888");
            var Q356;
            Q356=sQuery(id+"F1.wireOp",EDGE,"E671.filletArc");
            var Q357;
            Q357=sQuery(id+"F1.wireOp",EDGE,"E653");
            var Q358;
            Q358=sQuery(id+"F1.wireOp",EDGE,"E656.filletArc");
            var Q359;
            Q359=sQuery(id+"F1.wireOp",EDGE,"E648");
            var Q360;
            Q360=sQuery(id+"F1.wireOp",EDGE,"E657.filletArc");
            var Q361;
            Q361=sQuery(id+"F1.wireOp",EDGE,"E640");
            var Q362;
            Q362=sQuery(id+"F1.wireOp",EDGE,"E642.filletArc");
            var Q363;
            Q363=sQuery(id+"F1.wireOp",EDGE,"E639");
            var Q364;
            Q364=sQuery(id+"F1.wireOp",EDGE,"E885.filletArc");
            var Q365;
            Q365=sQuery(id+"F1.wireOp",EDGE,"E877");
            var Q366;
            Q366=sQuery(id+"F1.wireOp",EDGE,"E886.filletArc");
            var Q367;
            Q367=sQuery(id+"F1.wireOp",EDGE,"E878");
            var Q368;
            Q368=sQuery(id+"F1.wireOp",EDGE,"E887.filletArc");
            var Q369;
            Q369=sQuery(id+"F1.wireOp",EDGE,"E879");
            var Q370;
            Q370=sQuery(id+"F1.wireOp",EDGE,"E882.filletArc");
            var Q371;
            Q371=sQuery(id+"F1.wireOp",EDGE,"E880");
            var Q372;
            Q372=sQuery(id+"F1.wireOp",EDGE,"E651");
            var Q373;
            Q373=sQuery(id+"F1.wireOp",EDGE,"E909.filletArc");
            var Q374;
            Q374=sQuery(id+"F1.wireOp",EDGE,"E908.filletArc");
            var Q375;
            Q375=sQuery(id+"F1.wireOp",EDGE,"E890");
            var Q376;
            Q376=sQuery(id+"F1.wireOp",EDGE,"E907.filletArc");
            var Q377;
            Q377=sQuery(id+"F1.wireOp",EDGE,"E904");
            var Q378;
            Q378=sQuery(id+"F1.wireOp",EDGE,"E906.filletArc");
            var Q379;
            Q379=sQuery(id+"F1.wireOp",EDGE,"E903");
            var Q380;
            Q380=sQuery(id+"F1.wireOp",EDGE,"E911.filletArc");
            var Q381;
            Q381=sQuery(id+"F1.wireOp",EDGE,"E902");
            var Q382;
            Q382=sQuery(id+"F1.wireOp",EDGE,"E956.filletArc");
            sweep(context, id + "F7", {"operationType" : NewBodyOperationType.ADD, "profiles" : qUnion([Q0]), "path" : qUnion([Q1, Q2, Q3, Q4, Q5, Q6, Q7, Q8, Q9, Q10, Q11, Q12, Q13, Q14, Q15, Q16, Q17, Q18, Q19, Q20, Q21, Q22, Q23, Q24, Q25, Q26, Q27, Q28, Q29, Q30, Q31, Q32, Q33, Q34, Q35, Q36, Q37, Q38, Q39, Q40, Q41, Q42, Q43, Q44, Q45, Q46, Q47, Q48, Q49, Q50, Q51, Q52, Q53, Q54, Q55, Q56, Q57, Q58, Q59, Q60, Q61, Q62, Q63, Q64, Q65, Q66, Q67, Q68, Q69, Q70, Q71, Q72, Q73, Q74, Q75, Q76, Q77, Q78, Q79, Q80, Q81, Q82, Q83, Q84, Q85, Q86, Q87, Q88, Q89, Q90, Q91, Q92, Q93, Q94, Q95, Q96, Q97, Q98, Q99, Q100, Q101, Q102, Q103, Q104, Q105, Q106, Q107, Q108, Q109, Q110, Q111, Q112, Q113, Q114, Q115, Q116, Q117, Q118, Q119, Q120, Q121, Q122, Q123, Q124, Q125, Q126, Q127, Q128, Q129, Q130, Q131, Q132, Q133, Q134, Q135, Q136, Q137, Q138, Q139, Q140, Q141, Q142, Q143, Q144, Q145, Q146, Q147, Q148, Q149, Q150, Q151, Q152, Q153, Q154, Q155, Q156, Q157, Q158, Q159, Q160, Q161, Q162, Q163, Q164, Q165, Q166, Q167, Q168, Q169, Q170, Q171, Q172, Q173, Q174, Q175, Q176, Q177, Q178, Q179, Q180, Q181, Q182, Q183, Q184, Q185, Q186, Q187, Q188, Q189, Q190, Q191, Q192, Q193, Q194, Q195, Q196, Q197, Q198, Q199, Q200, Q201, Q202, Q203, Q204, Q205, Q206, Q207, Q208, Q209, Q210, Q211, Q212, Q213, Q214, Q215, Q216, Q217, Q218, Q219, Q220, Q221, Q222, Q223, Q224, Q225, Q226, Q227, Q228, Q229, Q230, Q231, Q232, Q233, Q234, Q235, Q236, Q237, Q238, Q239, Q240, Q241, Q242, Q243, Q244, Q245, Q246, Q247, Q248, Q249, Q250, Q251, Q252, Q253, Q254, Q255, Q256, Q257, Q258, Q259, Q260, Q261, Q262, Q263, Q264, Q265, Q266, Q267, Q268, Q269, Q270, Q271, Q272, Q273, Q274, Q275, Q276, Q277, Q278, Q279, Q280, Q281, Q282, Q283, Q284, Q285, Q286, Q287, Q288, Q289, Q290, Q291, Q292, Q293, Q294, Q295, Q296, Q297, Q298, Q299, Q300, Q301, Q302, Q303, Q304, Q305, Q306, Q307, Q308, Q309, Q310, Q311, Q312, Q313, Q314, Q315, Q316, Q317, Q318, Q319, Q320, Q321, Q322, Q323, Q324, Q325, Q326, Q327, Q328, Q329, Q330, Q331, Q332, Q333, Q334, Q335, Q336, Q337, Q338, Q339, Q340, Q341, Q342, Q343, Q344, Q345, Q346, Q347, Q348, Q349, Q350, Q351, Q352, Q353, Q354, Q355, Q356, Q357, Q358, Q359, Q360, Q361, Q362, Q363, Q364, Q365, Q366, Q367, Q368, Q369, Q370, Q371, Q372, Q373, Q374, Q375, Q376, Q377, Q378, Q379, Q380, Q381, Q382])});
        }
        {
            var Q0;
            Q0=makeQuery(id+"F4.opSweep","CAP_FACE",FACE,{"disambiguationData":[OSD([sQuery(id+"F1.wireOp",VERTEX,"E1092.end"),sQuery(id+"F3.wireOp",EDGE,"E1094")])],"isStart":true});
            var Q1;
            Q1=sQuery(id+"F1.wireOp",EDGE,"E1092");
            var Q2;
            Q2=sQuery(id+"F1.wireOp",EDGE,"E830");
            var Q3;
            Q3=sQuery(id+"F1.wireOp",EDGE,"E839.filletArc");
            var Q4;
            Q4=sQuery(id+"F1.wireOp",EDGE,"E831");
            var Q5;
            Q5=sQuery(id+"F1.wireOp",EDGE,"E834.filletArc");
            var Q6;
            Q6=sQuery(id+"F1.wireOp",EDGE,"E832");
            var Q7;
            Q7=sQuery(id+"F1.wireOp",EDGE,"E835.filletArc");
            var Q8;
            Q8=sQuery(id+"F1.wireOp",EDGE,"E722");
            var Q9;
            Q9=sQuery(id+"F1.wireOp",EDGE,"E730.filletArc");
            var Q10;
            Q10=sQuery(id+"F1.wireOp",EDGE,"E796");
            var Q11;
            Q11=sQuery(id+"F1.wireOp",EDGE,"E799.filletArc");
            var Q12;
            Q12=sQuery(id+"F1.wireOp",EDGE,"E797");
            var Q13;
            Q13=sQuery(id+"F1.wireOp",EDGE,"E800.filletArc");
            var Q14;
            Q14=sQuery(id+"F1.wireOp",EDGE,"E783");
            var Q15;
            Q15=sQuery(id+"F1.wireOp",EDGE,"E791.filletArc");
            var Q16;
            Q16=sQuery(id+"F1.wireOp",EDGE,"E782");
            var Q17;
            Q17=sQuery(id+"F1.wireOp",EDGE,"E790.filletArc");
            var Q18;
            Q18=sQuery(id+"F1.wireOp",EDGE,"E781");
            var Q19;
            Q19=sQuery(id+"F1.wireOp",EDGE,"E789.filletArc");
            var Q20;
            Q20=sQuery(id+"F1.wireOp",EDGE,"E780");
            var Q21;
            Q21=sQuery(id+"F1.wireOp",EDGE,"E601");
            var Q22;
            Q22=sQuery(id+"F1.wireOp",EDGE,"E810.filletArc");
            var Q23;
            Q23=sQuery(id+"F1.wireOp",EDGE,"E811.filletArc");
            var Q24;
            Q24=sQuery(id+"F1.wireOp",EDGE,"E809");
            var Q25;
            Q25=sQuery(id+"F1.wireOp",EDGE,"E812.filletArc");
            var Q26;
            Q26=sQuery(id+"F1.wireOp",EDGE,"E804");
            var Q27;
            Q27=sQuery(id+"F1.wireOp",EDGE,"E827.filletArc");
            var Q28;
            Q28=sQuery(id+"F1.wireOp",EDGE,"E818");
            var Q29;
            Q29=sQuery(id+"F1.wireOp",EDGE,"E826.filletArc");
            var Q30;
            Q30=sQuery(id+"F1.wireOp",EDGE,"E817");
            var Q31;
            Q31=sQuery(id+"F1.wireOp",EDGE,"E825.filletArc");
            var Q32;
            Q32=sQuery(id+"F1.wireOp",EDGE,"E816");
            var Q33;
            Q33=sQuery(id+"F1.wireOp",EDGE,"E1038.filletArc");
            var Q34;
            Q34=sQuery(id+"F1.wireOp",EDGE,"E577");
            var Q35;
            Q35=sQuery(id+"F1.wireOp",EDGE,"E585.filletArc");
            var Q36;
            Q36=sQuery(id+"F1.wireOp",EDGE,"E553");
            var Q37;
            Q37=sQuery(id+"F1.wireOp",EDGE,"E1023");
            var Q38;
            Q38=sQuery(id+"F1.wireOp",EDGE,"E1026.filletArc");
            var Q39;
            Q39=sQuery(id+"F1.wireOp",EDGE,"E552");
            var Q40;
            Q40=sQuery(id+"F1.wireOp",EDGE,"E1014.filletArc");
            var Q41;
            Q41=sQuery(id+"F1.wireOp",EDGE,"E565");
            var Q42;
            Q42=sQuery(id+"F1.wireOp",EDGE,"E573.filletArc");
            var Q43;
            Q43=sQuery(id+"F1.wireOp",EDGE,"E564");
            var Q44;
            Q44=sQuery(id+"F1.wireOp",EDGE,"E1000");
            var Q45;
            Q45=sQuery(id+"F1.wireOp",EDGE,"E1002.filletArc");
            var Q46;
            Q46=sQuery(id+"F1.wireOp",EDGE,"E549.filletArc");
            var Q47;
            Q47=sQuery(id+"F1.wireOp",EDGE,"E1074.filletArc");
            var Q48;
            Q48=sQuery(id+"F1.wireOp",EDGE,"E1071");
            var Q49;
            Q49=sQuery(id+"F1.wireOp",EDGE,"E529");
            var Q50;
            Q50=sQuery(id+"F1.wireOp",EDGE,"E537.filletArc");
            var Q51;
            Q51=sQuery(id+"F1.wireOp",EDGE,"E528");
            var Q52;
            Q52=sQuery(id+"F1.wireOp",EDGE,"E536.filletArc");
            var Q53;
            Q53=sQuery(id+"F1.wireOp",EDGE,"E533");
            var Q54;
            Q54=sQuery(id+"F1.wireOp",EDGE,"E1067.filletArc");
            var Q55;
            Q55=sQuery(id+"F1.wireOp",EDGE,"E516");
            var Q56;
            Q56=sQuery(id+"F1.wireOp",EDGE,"E1062.filletArc");
            var Q57;
            Q57=sQuery(id+"F1.wireOp",EDGE,"E1045");
            var Q58;
            Q58=sQuery(id+"F1.wireOp",EDGE,"E1053.filletArc");
            var Q59;
            Q59=sQuery(id+"F1.wireOp",EDGE,"E1044");
            var Q60;
            Q60=sQuery(id+"F1.wireOp",EDGE,"E1052.filletArc");
            var Q61;
            Q61=sQuery(id+"F1.wireOp",EDGE,"E1049");
            var Q62;
            Q62=sQuery(id+"F1.wireOp",EDGE,"E1051.filletArc");
            var Q63;
            Q63=sQuery(id+"F1.wireOp",EDGE,"E1048");
            var Q64;
            Q64=sQuery(id+"F1.wireOp",EDGE,"E994.filletArc");
            var Q65;
            Q65=sQuery(id+"F1.wireOp",EDGE,"E986");
            var Q66;
            Q66=sQuery(id+"F1.wireOp",EDGE,"E995.filletArc");
            var Q67;
            Q67=sQuery(id+"F1.wireOp",EDGE,"E492");
            var Q68;
            Q68=sQuery(id+"F1.wireOp",EDGE,"E925");
            var Q69;
            Q69=sQuery(id+"F1.wireOp",EDGE,"E990.filletArc");
            var Q70;
            Q70=sQuery(id+"F1.wireOp",EDGE,"E933.filletArc");
            var Q71;
            Q71=sQuery(id+"F1.wireOp",EDGE,"E924");
            var Q72;
            Q72=sQuery(id+"F1.wireOp",EDGE,"E932.filletArc");
            var Q73;
            Q73=sQuery(id+"F1.wireOp",EDGE,"E929");
            var Q74;
            Q74=sQuery(id+"F1.wireOp",EDGE,"E931.filletArc");
            var Q75;
            Q75=sQuery(id+"F1.wireOp",EDGE,"E561.filletArc");
            var Q76;
            Q76=sQuery(id+"F1.wireOp",EDGE,"E928");
            var Q77;
            Q77=sQuery(id+"F1.wireOp",EDGE,"E982.filletArc");
            var Q78;
            Q78=sQuery(id+"F1.wireOp",EDGE,"E974");
            var Q79;
            Q79=sQuery(id+"F1.wireOp",EDGE,"E487.filletArc");
            var Q80;
            Q80=sQuery(id+"F1.wireOp",EDGE,"E733");
            var Q81;
            Q81=sQuery(id+"F1.wireOp",EDGE,"E742.filletArc");
            var Q82;
            Q82=sQuery(id+"F1.wireOp",EDGE,"E734");
            var Q83;
            Q83=sQuery(id+"F1.wireOp",EDGE,"E743.filletArc");
            var Q84;
            Q84=sQuery(id+"F1.wireOp",EDGE,"E735");
            var Q85;
            Q85=sQuery(id+"F1.wireOp",EDGE,"E749");
            var Q86;
            Q86=sQuery(id+"F1.wireOp",EDGE,"E752.filletArc");
            var Q87;
            Q87=sQuery(id+"F1.wireOp",EDGE,"E751.filletArc");
            var Q88;
            Q88=sQuery(id+"F1.wireOp",EDGE,"E750.filletArc");
            var Q89;
            Q89=sQuery(id+"F1.wireOp",EDGE,"E748");
            var Q90;
            Q90=sQuery(id+"F1.wireOp",EDGE,"E747");
            var Q91;
            Q91=sQuery(id+"F1.wireOp",EDGE,"E765.filletArc");
            var Q92;
            Q92=sQuery(id+"F1.wireOp",EDGE,"E460");
            var Q93;
            Q93=sQuery(id+"F1.wireOp",EDGE,"E766.filletArc");
            var Q94;
            Q94=sQuery(id+"F1.wireOp",EDGE,"E758");
            var Q95;
            Q95=sQuery(id+"F1.wireOp",EDGE,"E767.filletArc");
            var Q96;
            Q96=sQuery(id+"F1.wireOp",EDGE,"E768");
            var Q97;
            Q97=sQuery(id+"F1.wireOp",EDGE,"E776.filletArc");
            var Q98;
            Q98=sQuery(id+"F1.wireOp",EDGE,"E773");
            var Q99;
            Q99=sQuery(id+"F1.wireOp",EDGE,"E775.filletArc");
            var Q100;
            Q100=sQuery(id+"F1.wireOp",EDGE,"E772");
            var Q101;
            Q101=sQuery(id+"F1.wireOp",EDGE,"E774.filletArc");
            var Q102;
            Q102=sQuery(id+"F1.wireOp",EDGE,"E936");
            var Q103;
            Q103=sQuery(id+"F1.wireOp",EDGE,"E945.filletArc");
            var Q104;
            Q104=sQuery(id+"F1.wireOp",EDGE,"E700");
            var Q105;
            Q105=sQuery(id+"F1.wireOp",EDGE,"E702.filletArc");
            var Q106;
            Q106=sQuery(id+"F1.wireOp",EDGE,"E699");
            var Q107;
            Q107=sQuery(id+"F1.wireOp",EDGE,"E957.filletArc");
            var Q108;
            Q108=sQuery(id+"F1.wireOp",EDGE,"E688");
            var Q109;
            Q109=sQuery(id+"F1.wireOp",EDGE,"E690.filletArc");
            var Q110;
            Q110=sQuery(id+"F1.wireOp",EDGE,"E912");
            var Q111;
            Q111=sQuery(id+"F1.wireOp",EDGE,"E921.filletArc");
            var Q112;
            Q112=sQuery(id+"F1.wireOp",EDGE,"E676");
            var Q113;
            Q113=sQuery(id+"F1.wireOp",EDGE,"E678.filletArc");
            var Q114;
            Q114=sQuery(id+"F1.wireOp",EDGE,"E960");
            var Q115;
            Q115=sQuery(id+"F1.wireOp",EDGE,"E969.filletArc");
            var Q116;
            Q116=sQuery(id+"F1.wireOp",EDGE,"E664");
            var Q117;
            Q117=sQuery(id+"F1.wireOp",EDGE,"E666.filletArc");
            var Q118;
            Q118=sQuery(id+"F1.wireOp",EDGE,"E888");
            var Q119;
            Q119=sQuery(id+"F1.wireOp",EDGE,"E897.filletArc");
            var Q120;
            Q120=sQuery(id+"F1.wireOp",EDGE,"E652");
            var Q121;
            Q121=sQuery(id+"F1.wireOp",EDGE,"E651");
            var Q122;
            Q122=sQuery(id+"F1.wireOp",EDGE,"E654.filletArc");
            var Q123;
            Q123=sQuery(id+"F1.wireOp",EDGE,"E659.filletArc");
            var Q124;
            Q124=sQuery(id+"F1.wireOp",EDGE,"E650");
            var Q125;
            Q125=sQuery(id+"F1.wireOp",EDGE,"E884.filletArc");
            var Q126;
            Q126=sQuery(id+"F1.wireOp",EDGE,"E885.filletArc");
            var Q127;
            Q127=sQuery(id+"F1.wireOp",EDGE,"E639");
            var Q128;
            Q128=sQuery(id+"F1.wireOp",EDGE,"E877");
            var Q129;
            Q129=sQuery(id+"F1.wireOp",EDGE,"E870.filletArc");
            var Q130;
            Q130=sQuery(id+"F1.wireOp",EDGE,"E867");
            var Q131;
            Q131=sQuery(id+"F1.wireOp",EDGE,"E875.filletArc");
            var Q132;
            Q132=sQuery(id+"F1.wireOp",EDGE,"E866");
            var Q133;
            Q133=sQuery(id+"F1.wireOp",EDGE,"E874.filletArc");
            var Q134;
            Q134=sQuery(id+"F1.wireOp",EDGE,"E856");
            var Q135;
            Q135=sQuery(id+"F1.wireOp",EDGE,"E859.filletArc");
            var Q136;
            Q136=sQuery(id+"F1.wireOp",EDGE,"E857");
            var Q137;
            Q137=sQuery(id+"F1.wireOp",EDGE,"E860.filletArc");
            var Q138;
            Q138=sQuery(id+"F1.wireOp",EDGE,"E852");
            var Q139;
            Q139=sQuery(id+"F1.wireOp",EDGE,"E861.filletArc");
            var Q140;
            Q140=sQuery(id+"F1.wireOp",EDGE,"E844");
            var Q141;
            Q141=sQuery(id+"F1.wireOp",EDGE,"E846.filletArc");
            var Q142;
            Q142=sQuery(id+"F1.wireOp",EDGE,"E843");
            var Q143;
            Q143=sQuery(id+"F1.wireOp",EDGE,"E851.filletArc");
            var Q144;
            Q144=sQuery(id+"F1.wireOp",EDGE,"E842");
            var Q145;
            Q145=sQuery(id+"F1.wireOp",EDGE,"E659.filletArc");
            var Q146;
            Q146=sQuery(id+"F1.wireOp",EDGE,"E650");
            var Q147;
            Q147=sQuery(id+"F1.wireOp",EDGE,"E884.filletArc");
            var Q148;
            Q148=sQuery(id+"F1.wireOp",EDGE,"E639");
            var Q149;
            Q149=sQuery(id+"F1.wireOp",EDGE,"E885.filletArc");
            var Q150;
            Q150=sQuery(id+"F1.wireOp",EDGE,"E870.filletArc");
            var Q151;
            Q151=sQuery(id+"F1.wireOp",EDGE,"E877");
            var Q152;
            Q152=sQuery(id+"F1.wireOp",EDGE,"E867");
            var Q153;
            Q153=sQuery(id+"F1.wireOp",EDGE,"E875.filletArc");
            var Q154;
            Q154=sQuery(id+"F1.wireOp",EDGE,"E866");
            var Q155;
            Q155=sQuery(id+"F1.wireOp",EDGE,"E874.filletArc");
            var Q156;
            Q156=sQuery(id+"F1.wireOp",EDGE,"E856");
            var Q157;
            Q157=sQuery(id+"F1.wireOp",EDGE,"E859.filletArc");
            var Q158;
            Q158=sQuery(id+"F1.wireOp",EDGE,"E857");
            var Q159;
            Q159=sQuery(id+"F1.wireOp",EDGE,"E860.filletArc");
            var Q160;
            Q160=sQuery(id+"F1.wireOp",EDGE,"E852");
            var Q161;
            Q161=sQuery(id+"F1.wireOp",EDGE,"E861.filletArc");
            var Q162;
            Q162=sQuery(id+"F1.wireOp",EDGE,"E844");
            var Q163;
            Q163=sQuery(id+"F1.wireOp",EDGE,"E846.filletArc");
            var Q164;
            Q164=sQuery(id+"F1.wireOp",EDGE,"E843");
            var Q165;
            Q165=sQuery(id+"F1.wireOp",EDGE,"E851.filletArc");
            var Q166;
            Q166=sQuery(id+"F1.wireOp",EDGE,"E842");
            sweep(context, id + "F8", {"operationType" : NewBodyOperationType.ADD, "profiles" : qUnion([Q0]), "path" : qUnion([Q1, Q2, Q3, Q4, Q5, Q6, Q7, Q8, Q9, Q10, Q11, Q12, Q13, Q14, Q15, Q16, Q17, Q18, Q19, Q20, Q21, Q22, Q23, Q24, Q25, Q26, Q27, Q28, Q29, Q30, Q31, Q32, Q33, Q34, Q35, Q36, Q37, Q38, Q39, Q40, Q41, Q42, Q43, Q44, Q45, Q46, Q47, Q48, Q49, Q50, Q51, Q52, Q53, Q54, Q55, Q56, Q57, Q58, Q59, Q60, Q61, Q62, Q63, Q64, Q65, Q66, Q67, Q68, Q69, Q70, Q71, Q72, Q73, Q74, Q75, Q76, Q77, Q78, Q79, Q80, Q81, Q82, Q83, Q84, Q85, Q86, Q87, Q88, Q89, Q90, Q91, Q92, Q93, Q94, Q95, Q96, Q97, Q98, Q99, Q100, Q101, Q102, Q103, Q104, Q105, Q106, Q107, Q108, Q109, Q110, Q111, Q112, Q113, Q114, Q115, Q116, Q117, Q118, Q119, Q120, Q121, Q122, Q123, Q124, Q125, Q126, Q127, Q128, Q129, Q130, Q131, Q132, Q133, Q134, Q135, Q136, Q137, Q138, Q139, Q140, Q141, Q142, Q143, Q144, Q145, Q146, Q147, Q148, Q149, Q150, Q151, Q152, Q153, Q154, Q155, Q156, Q157, Q158, Q159, Q160, Q161, Q162, Q163, Q164, Q165, Q166])});
        }
        {
            var Q0;
            Q0=makeQuery(id+"F7.opSweep","CAP_FACE",FACE,{"disambiguationData":[OSD([sQuery(id+"F1.wireOp",VERTEX,"E1093.end"),sQuery(id+"F6.wireOp",EDGE,"E1095")])],"isStart":true});
            var Q1;
            Q1=sQuery(id+"F1.wireOp",EDGE,"E1093");
            var Q2;
            Q2=sQuery(id+"F1.wireOp",EDGE,"E977");
            var Q3;
            Q3=sQuery(id+"F1.wireOp",EDGE,"E980.filletArc");
            var Q4;
            Q4=sQuery(id+"F1.wireOp",EDGE,"E972");
            var Q5;
            Q5=sQuery(id+"F1.wireOp",EDGE,"E981.filletArc");
            var Q6;
            Q6=sQuery(id+"F1.wireOp",EDGE,"E928");
            var Q7;
            Q7=sQuery(id+"F1.wireOp",EDGE,"E930.filletArc");
            var Q8;
            Q8=sQuery(id+"F1.wireOp",EDGE,"E927");
            var Q9;
            Q9=sQuery(id+"F1.wireOp",EDGE,"E489.filletArc");
            var Q10;
            Q10=sQuery(id+"F1.wireOp",EDGE,"E481");
            var Q11;
            Q11=sQuery(id+"F1.wireOp",EDGE,"E490.filletArc");
            var Q12;
            Q12=sQuery(id+"F1.wireOp",EDGE,"E482");
            var Q13;
            Q13=sQuery(id+"F1.wireOp",EDGE,"E491.filletArc");
            var Q14;
            Q14=sQuery(id+"F1.wireOp",EDGE,"E468");
            var Q15;
            Q15=sQuery(id+"F1.wireOp",EDGE,"E486.filletArc");
            var Q16;
            Q16=sQuery(id+"F1.wireOp",EDGE,"E733");
            var Q17;
            Q17=sQuery(id+"F1.wireOp",EDGE,"E741.filletArc");
            var Q18;
            Q18=sQuery(id+"F1.wireOp",EDGE,"E975");
            var Q19;
            Q19=sQuery(id+"F1.wireOp",EDGE,"E978.filletArc");
            var Q20;
            Q20=sQuery(id+"F1.wireOp",EDGE,"E976");
            sweep(context, id + "F9", {"operationType" : NewBodyOperationType.ADD, "profiles" : qUnion([Q0]), "path" : qUnion([Q1, Q2, Q3, Q4, Q5, Q6, Q7, Q8, Q9, Q10, Q11, Q12, Q13, Q14, Q15, Q16, Q17, Q18, Q19, Q20])});
        }
    });
